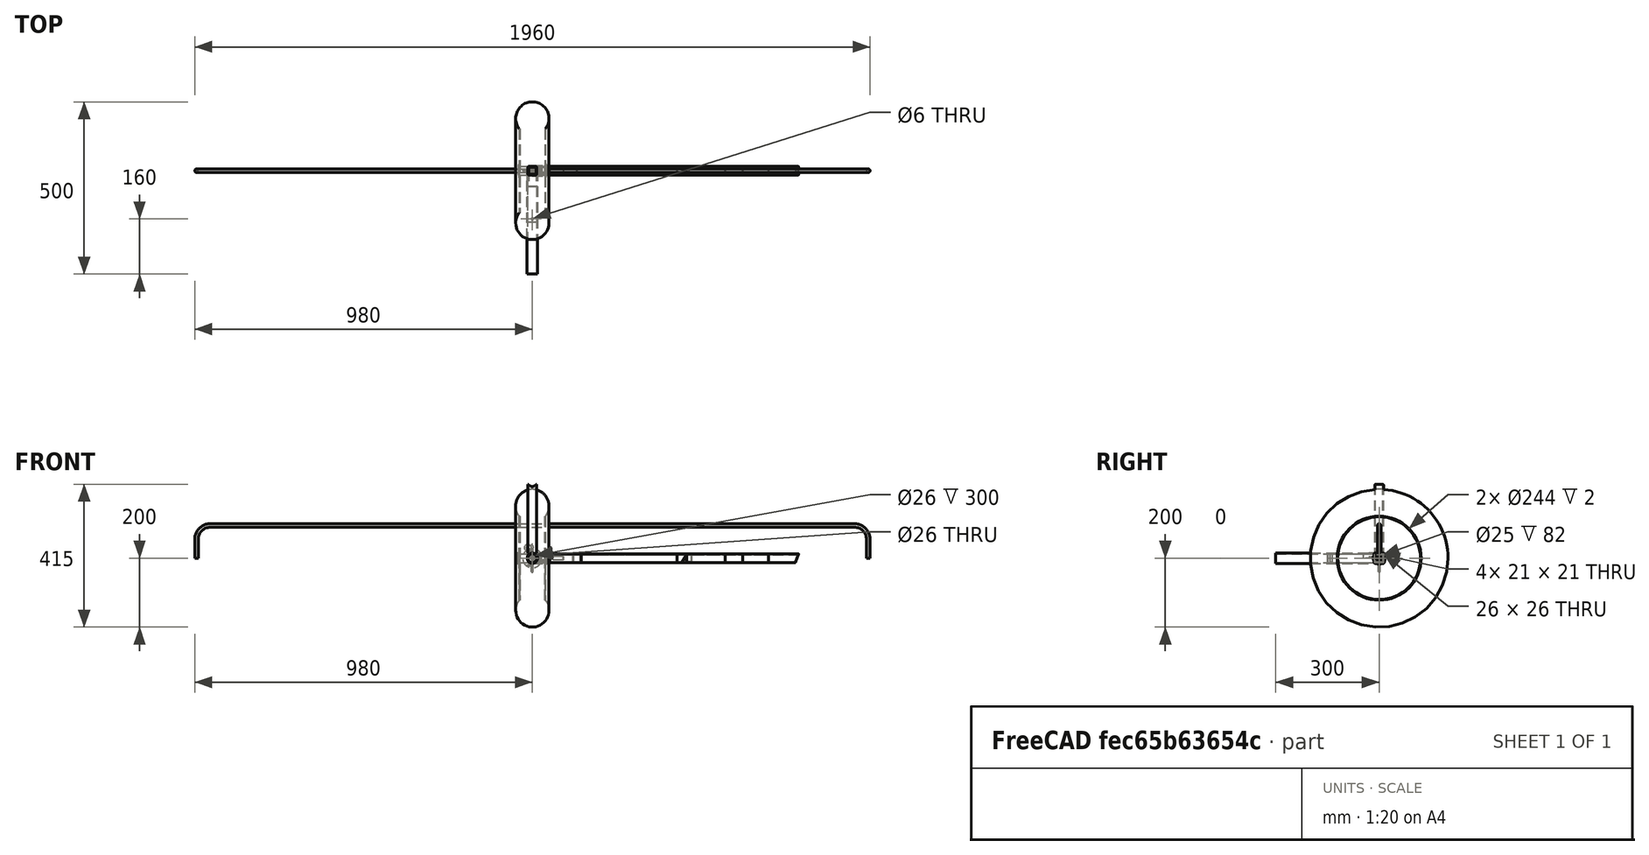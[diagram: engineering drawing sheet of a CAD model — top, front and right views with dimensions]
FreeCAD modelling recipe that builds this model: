
FCSTD DOCUMENT  (FreeCAD 1.0R39109 (Git))
Label: brouetteas4-am
License: Creative Commons Attribution-NonCommercial-ShareAlike
LicenseURL: http://creativecommons.org/licenses/by-nc-sa/4.0/
objects: TechDraw::DrawViewAnnotation×100, PartDesign::CoordinateSystem×62, App::Link×60, TechDraw::DrawProjGroupItem×58, TechDraw::DrawViewBalloon×56, TechDraw::DrawViewDimension×39, Sketcher::SketchObject×37, App::Part×25, PartDesign::Body×24, PartDesign::Pad×20, TechDraw::DrawSVGTemplate×16, TechDraw::DrawPage×16, TechDraw::DrawGeomHatch×14, TechDraw::DrawProjGroup×13, Spreadsheet::Sheet×12, TechDraw::DrawViewSpreadsheet×10, PartDesign::Groove×8, PartDesign::Plane×6, TechDraw::DrawViewDimExtent×3, TechDraw::DrawViewDetail×3, +7 more types
note: 342 computed .brp shape members not serialized (recipe doc carries the construction recipe); baked Part::Feature solids carry a one-line shape summary decoded from their .brp

FEATURE [PartDesign::CoordinateSystem] LCS_Origin
  AttacherType = Attacher::AttachEngine3D
  AttachmentSupport = -> [X_Axis]
  MapMode = 2
FEATURE [App::DocumentObjectGroup] Constraints
FEATURE [App::FeaturePython] Variables  # WARN: FeaturePython — macro-defined, semantics opaque (R4)
FEATURE [Sketcher::SketchObject] Sketch
  ArcFitTolerance = 0
  FullyConstrained = true
  MakeInternals = false
  MapMode = 5
  Placement = pos=(0,0,0) rot=(0.57735,0.57735,0.57735;2.0944rad)
  expr: Constraints[15] = .Constraints.hauteur * 0.1
  expr: Constraints[27] = .Constraints.epaisseur
  sketch-geometry (12):
    g0: LineSegment StartX=-10 StartY=12.5 StartZ=0 EndX=10 EndY=12.5 EndZ=0
    g1: LineSegment StartX=12.5 StartY=10 StartZ=0 EndX=12.5 EndY=-10 EndZ=0
    g2: LineSegment StartX=10 StartY=-12.5 StartZ=0 EndX=-10 EndY=-12.5 EndZ=0
    g3: LineSegment StartX=-12.5 StartY=-10 StartZ=0 EndX=-12.5 EndY=10 EndZ=0
    g4: ArcOfCircle CenterX=-10 CenterY=10 CenterZ=0 NormalX=0 NormalY=0 NormalZ=1 AngleXU=0 Radius=2.5 StartAngle=1.5708 EndAngle=3.14159
    g5: ArcOfCircle CenterX=10 CenterY=10 CenterZ=0 NormalX=0 NormalY=0 NormalZ=1 AngleXU=0 Radius=2.5 StartAngle=2e-16 EndAngle=1.5708
    g6: ArcOfCircle CenterX=10 CenterY=-10 CenterZ=0 NormalX=0 NormalY=0 NormalZ=1 AngleXU=0 Radius=2.5 StartAngle=4.71239 EndAngle=6.28319
    g7: ArcOfCircle CenterX=-10 CenterY=-10 CenterZ=0 NormalX=0 NormalY=0 NormalZ=1 AngleXU=0 Radius=2.5 StartAngle=3.14159 EndAngle=4.71239
    g8: LineSegment StartX=-10.5 StartY=10.5 StartZ=0 EndX=10.5 EndY=10.5 EndZ=0
    g9: LineSegment StartX=10.5 StartY=10.5 StartZ=0 EndX=10.5 EndY=-10.5 EndZ=0
    g10: LineSegment StartX=10.5 StartY=-10.5 StartZ=0 EndX=-10.5 EndY=-10.5 EndZ=0
    g11: LineSegment StartX=-10.5 StartY=-10.5 StartZ=0 EndX=-10.5 EndY=10.5 EndZ=0
  constraints (28):
    c: Horizontal(g2)
    c: Vertical(g3)
    c: Tangent(g0,g4) = 1.5708
    c: Tangent(g3,g4) = 1.5708
    c: Tangent(g0,g5) = 1.5708
    c: Tangent(g1,g5) = 1.5708
    c: Tangent(g1,g6) = 1.5708
    c: Tangent(g2,g6) = 1.5708
    c: Tangent(g2,g7) = 1.5708
    c: Tangent(g3,g7) = 1.5708
    c: Equal(g4,g5)
    c: DistanceY(g2,g0) = 25  'hauteur'
    c: DistanceX(g3,g1) = 25  'largeur'
    c: Equal(g5,g6)
    c: Equal(g6,g7)
    c: Radius(g7) = 2.5
    c: Symmetric(g1,g1,g-1)
    c: Symmetric(g0,g0,g-2)
    c: Coincident(g8,g9)
    c: Coincident(g9,g10)
    c: Coincident(g10,g11)
    c: Coincident(g11,g8)
    c: Horizontal(g10)
    c: Vertical(g11)
    c: Symmetric(g8,g9,g-1)
    c: Symmetric(g8,g8,g-2)
    c: DistanceX(g3,g8) = 2  'epaisseur'
    c: DistanceY(g2,g9) = 2
FEATURE [PartDesign::Pad] Pad
  Direction = (1,1e-16,-1e-16)
  Length = 2285
  Length2 = 100
  Placement = pos=(0,0,0) rot=(0.57735,0.57735,0.57735;2.0944rad)
  Profile = -> Sketch
  Suppressed = false
  Type = 0
  expr: Length = Spreadsheet.B4 - Spreadsheet.B2 + 300
FEATURE [PartDesign::CoordinateSystem] LCS_0  label="cote1"
  AttacherType = Attacher::AttachEngine3D
  AttachmentSupport = -> [X_Axis002]
  MapMode = 2
FEATURE [PartDesign::CoordinateSystem] LCS_0001  label="cote1A2"
  AttacherType = Attacher::AttachEngine3D
  AttachmentSupport = -> [X_Axis003]
  MapMode = 2
FEATURE [Sketcher::SketchObject] Sketch001
  ArcFitTolerance = 0
  FullyConstrained = true
  MakeInternals = false
  MapMode = 5
  Placement = pos=(0,0,0) rot=(0.57735,0.57735,0.57735;2.0944rad)
  expr: Constraints[15] = .Constraints.hauteur * 0.1
  expr: Constraints[27] = .Constraints.epaisseur
  sketch-geometry (12):
    g0: LineSegment StartX=-10 StartY=12.5 StartZ=0 EndX=10 EndY=12.5 EndZ=0
    g1: LineSegment StartX=12.5 StartY=10 StartZ=0 EndX=12.5 EndY=-10 EndZ=0
    g2: LineSegment StartX=10 StartY=-12.5 StartZ=0 EndX=-10 EndY=-12.5 EndZ=0
    g3: LineSegment StartX=-12.5 StartY=-10 StartZ=0 EndX=-12.5 EndY=10 EndZ=0
    g4: ArcOfCircle CenterX=-10 CenterY=10 CenterZ=0 NormalX=0 NormalY=0 NormalZ=1 AngleXU=0 Radius=2.5 StartAngle=1.5708 EndAngle=3.14159
    g5: ArcOfCircle CenterX=10 CenterY=10 CenterZ=0 NormalX=0 NormalY=0 NormalZ=1 AngleXU=0 Radius=2.5 StartAngle=2e-16 EndAngle=1.5708
    g6: ArcOfCircle CenterX=10 CenterY=-10 CenterZ=0 NormalX=0 NormalY=0 NormalZ=1 AngleXU=0 Radius=2.5 StartAngle=4.71239 EndAngle=6.28319
    g7: ArcOfCircle CenterX=-10 CenterY=-10 CenterZ=0 NormalX=0 NormalY=0 NormalZ=1 AngleXU=0 Radius=2.5 StartAngle=3.14159 EndAngle=4.71239
    g8: LineSegment StartX=-10.5 StartY=10.5 StartZ=0 EndX=10.5 EndY=10.5 EndZ=0
    g9: LineSegment StartX=10.5 StartY=10.5 StartZ=0 EndX=10.5 EndY=-10.5 EndZ=0
    g10: LineSegment StartX=10.5 StartY=-10.5 StartZ=0 EndX=-10.5 EndY=-10.5 EndZ=0
    g11: LineSegment StartX=-10.5 StartY=-10.5 StartZ=0 EndX=-10.5 EndY=10.5 EndZ=0
  constraints (28):
    c: Horizontal(g2)
    c: Vertical(g3)
    c: Tangent(g0,g4) = 1.5708
    c: Tangent(g3,g4) = 1.5708
    c: Tangent(g0,g5) = 1.5708
    c: Tangent(g1,g5) = 1.5708
    c: Tangent(g1,g6) = 1.5708
    c: Tangent(g2,g6) = 1.5708
    c: Tangent(g2,g7) = 1.5708
    c: Tangent(g3,g7) = 1.5708
    c: Equal(g4,g5)
    c: DistanceY(g2,g0) = 25  'hauteur'
    c: DistanceX(g3,g1) = 25  'largeur'
    c: Equal(g5,g6)
    c: Equal(g6,g7)
    c: Radius(g7) = 2.5
    c: Symmetric(g1,g1,g-1)
    c: Symmetric(g0,g0,g-2)
    c: Coincident(g8,g9)
    c: Coincident(g9,g10)
    c: Coincident(g10,g11)
    c: Coincident(g11,g8)
    c: Horizontal(g10)
    c: Vertical(g11)
    c: Symmetric(g8,g9,g-1)
    c: Symmetric(g8,g8,g-2)
    c: DistanceX(g3,g8) = 2  'epaisseur'
    c: DistanceY(g2,g9) = 2
FEATURE [PartDesign::Body] Body001
  AllowCompound = false
  Origin = -> Origin004
FEATURE [PartDesign::Pad] Pad001
  Direction = (1,1e-16,-1e-16)
  Length = 610
  Length2 = 100
  Placement = pos=(0,0,0) rot=(0.57735,0.57735,0.57735;2.0944rad)
  Profile = -> Sketch001
  Suppressed = false
  Type = 0
FEATURE [PartDesign::CoordinateSystem] LCS_0002
  AttacherType = Attacher::AttachEngine3D
  AttachmentOffset = pos=(0,5,0) rot=(0,0,1;0rad)
  AttachmentSupport = -> [X_Axis005]
  MapMode = 2
  Placement = pos=(0,5,0) rot=(0,0,1;0rad)
FEATURE [PartDesign::CoordinateSystem] LCS_0003
  AttacherType = Attacher::AttachEngine3D
  AttachmentOffset = pos=(0,5,0) rot=(0,0,1;0rad)
  AttachmentSupport = -> [X_Axis006]
  MapMode = 2
  Placement = pos=(0,5,0) rot=(0,0,1;0rad)
FEATURE [Sketcher::SketchObject] Sketch002
  ArcFitTolerance = 0
  AttachmentSupport = -> [XZ_Plane007]
  FullyConstrained = true
  MakeInternals = false
  MapMode = 5
  Placement = pos=(0,0,0) rot=(1,0,0;1.5708rad)
  expr: .Constraints.longueur = Spreadsheet.B4 - Spreadsheet.B2 * 2 - 10
  expr: Constraints[4] = Spreadsheet.B2
  sketch-geometry (7):
    g0: LineSegment StartX=-975 StartY=0 StartZ=0 EndX=-975 EndY=25 EndZ=0
    g1: LineSegment StartX=975 StartY=8e-16 StartZ=0 EndX=975 EndY=25 EndZ=0
    g2: LineSegment StartX=-975 StartY=25 StartZ=0 EndX=-975 EndY=55 EndZ=0
    g3: LineSegment StartX=-935 StartY=95 StartZ=0 EndX=935 EndY=95 EndZ=0
    g4: LineSegment StartX=975 StartY=55 StartZ=0 EndX=975 EndY=25 EndZ=0
    g5: ArcOfCircle CenterX=935 CenterY=55 CenterZ=0 NormalX=0 NormalY=0 NormalZ=1 AngleXU=0 Radius=40 StartAngle=0 EndAngle=1.5708
    g6: ArcOfCircle CenterX=-935 CenterY=55 CenterZ=0 NormalX=0 NormalY=0 NormalZ=1 AngleXU=0 Radius=40 StartAngle=1.5708 EndAngle=3.14159
  constraints (19):
    c: PointOnObject(g0,g-1)
    c: Vertical(g0)
    c: Vertical(g1)
    c: Symmetric(g0,g1,g-2)
    c: DistanceY(g0,g0) = 25
    c: DistanceX(g0,g1) = 1950  'longueur'
    c: Equal(g1,g0)
    c: Coincident(g0,g2)
    c: Vertical(g2)
    c: Horizontal(g3)
    c: Coincident(g4,g1)
    c: Vertical(g4)
    c: Tangent(g3,g5) = 1.5708
    c: Tangent(g4,g5) = 1.5708
    c: Tangent(g2,g6) = 1.5708
    c: Tangent(g3,g6) = 1.5708
    c: Equal(g6,g5)
    c: DistanceY(g0,g3) = 70
    c: Radius(g6) = 40
FEATURE [Sketcher::SketchObject] Sketch003
  ArcFitTolerance = 0
  AttachmentSupport = -> [XY_Plane007]
  ExternalGeometry = -> [Sketch002]
  FullyConstrained = true
  MakeInternals = false
  MapMode = 5
  sketch-geometry (1):
    g0: Circle CenterX=-975 CenterY=0 CenterZ=0 NormalX=0 NormalY=0 NormalZ=1 AngleXU=0 Radius=5
  constraints (2):
    c: Coincident(g0,g-3)
    c: Diameter(g0) = 10
FEATURE [PartDesign::AdditivePipe] AdditivePipe
  AuxilleryCurvelinear = true
  AuxillerySpineTangent = false
  Binormal = (0,0,0)
  Mode = 0
  Profile = -> Sketch003
  Spine = -> Sketch002
  SpineTangent = false
  Suppressed = false
  Transformation = 0
  Transition = 0
FEATURE [PartDesign::Body] Body002
  AllowCompound = false
  Group = -> [Sketch002,Sketch003,AdditivePipe]
  Origin = -> Origin007
  Tip = -> AdditivePipe
FEATURE [App::Part] A3
  Group = -> [LCS_0002,Body002]
  Nom_de_la_piece = A3
  Origin = -> Origin005
  Reference_AP = fer rond Ø10
  longueur = 2140
FEATURE [Sketcher::SketchObject] Sketch004
  ArcFitTolerance = 0
  AttachmentSupport = -> [YZ_Plane008]
  FullyConstrained = true
  MakeInternals = false
  MapMode = 5
  Placement = pos=(0,0,0) rot=(0.57735,0.57735,0.57735;2.0944rad)
  sketch-geometry (1):
    g0: Circle CenterX=0 CenterY=0 CenterZ=0 NormalX=0 NormalY=0 NormalZ=1 AngleXU=0 Radius=5
  constraints (2):
    c: Coincident(g0,g-1)
    c: Diameter(g0) = 10  'diametre'
FEATURE [PartDesign::Pad] Pad002
  Direction = (1,0,0)
  Length = 90
  Length2 = 100
  Placement = pos=(0,0,0) rot=(0.57735,0.57735,0.57735;2.0944rad)
  Profile = -> Sketch004
  Suppressed = false
  Type = 0
FEATURE [PartDesign::Body] Body003
  AllowCompound = false
  Group = -> [Sketch004,Pad002]
  Origin = -> Origin008
  Tip = -> Pad002
FEATURE [App::Part] A4
  Group = -> [LCS_0003,Body003]
  Nom_de_la_piece = 'A4
  Origin = -> Origin006
  Reference_AP = fer rond Ø10
  longueur = 90
FEATURE [PartDesign::CoordinateSystem] cote2A2
  AttacherType = Attacher::AttachEngine3D
  AttachmentSupport = -> [Pad001]
  MapMode = 5
  Placement = pos=(610,2.684e-13,0) rot=(0.57735,0.57735,0.57735;2.0944rad)
FEATURE [Spreadsheet::Sheet] Spreadsheet
  cells = A1='profile; A2='tube carré; B2=25; C2='mm; A4='taille utile du plateau; B4=2010; C4='X; D4=610; A5='hauteur plateau; B5=500; A6='hauteur de la roue; B6=400; A7='axe; B7=25; A8='epaisseur upn axe; B8=4; A9='espace des roues; B9=95; A10='ecart au sol; B10=75; A11='hauteur des mains; B11==D11 * 0.45; C11='taille de la personne; D11=1700; A12='hauteur du panneau finale; B12=610; A13='tube poigné; B13=30
FEATURE [PartDesign::CoordinateSystem] face1A2
  AttacherType = Attacher::AttachEngine3D
  AttachmentOffset = pos=(0,12.5,0) rot=(0,0,1;0rad)
  AttachmentSupport = -> [Pad001]
  MapMode = 5
  Placement = pos=(12.5,12.5,2.1e-15) rot=(0.57735,0.57735,0.57735;4.18879rad)
  expr: .AttachmentOffset.Base.y = Spreadsheet.B2 / 2
FEATURE [PartDesign::CoordinateSystem] face4A2
  AttacherType = Attacher::AttachEngine3D
  AttachmentOffset = pos=(0,597.5,0) rot=(0,0,1;0rad)
  AttachmentSupport = -> [Pad001]
  MapMode = 5
  Placement = pos=(597.5,12.5,2.1e-15) rot=(0.57735,0.57735,0.57735;4.18879rad)
  expr: .AttachmentOffset.Base.y = Spreadsheet.D4 - Spreadsheet.B2 / 2
FEATURE [PartDesign::CoordinateSystem] face2  label="face2A2"
  AttacherType = Attacher::AttachEngine3D
  AttachmentOffset = pos=(0,207.5,0) rot=(0,0,1;0rad)
  AttachmentSupport = -> [Pad001]
  MapMode = 5
  Placement = pos=(207.5,12.5,2.1e-15) rot=(0.57735,0.57735,0.57735;4.18879rad)
  expr: .AttachmentOffset.Base.y = (Spreadsheet.D4 - Spreadsheet.B2) * 1 / 3 + Spreadsheet.B2 / 2
FEATURE [PartDesign::CoordinateSystem] face3A2
  AttacherType = Attacher::AttachEngine3D
  AttachmentOffset = pos=(0,402.5,0) rot=(0,0,1;0rad)
  AttachmentSupport = -> [Pad001]
  MapMode = 5
  Placement = pos=(402.5,12.5,2.1e-15) rot=(0.57735,0.57735,0.57735;4.18879rad)
  expr: .AttachmentOffset.Base.y = (Spreadsheet.D4 - Spreadsheet.B2) * 2 / 3 + Spreadsheet.B2 / 2
FEATURE [PartDesign::CoordinateSystem] attach
  AttacherType = Attacher::AttachEngine3D
  AttachmentOffset = pos=(0,305,0) rot=(0,0,1;0rad)
  AttachmentSupport = -> [Pad001]
  MapMode = 5
  Placement = pos=(305,-12.5,-2.1e-15) rot=(0.57735,0.57735,-0.57735;2.0944rad)
  expr: .AttachmentOffset.Base.y = Spreadsheet.D4 / 2
FEATURE [App::Link] A2001
  AssemblyType = Asm4EE
  AttachedBy = #attach
  AttachedTo = Parent Assembly#LCS_Origin
  AttachmentOffset = pos=(0,0,0) rot=(0,-1,0;1.5708rad)
  LinkPlacement = pos=(12.5,-305,-2.84e-14) rot=(-0.707107,-0.707107,0;3.14159rad)
  LinkedObject = -> A2
  Placement = pos=(12.5,-305,-2.84e-14) rot=(-0.707107,-0.707107,0;3.14159rad)
  expr: Placement = LCS_Origin.Placement * AttachmentOffset * attach.Placement ^ -1
FEATURE [App::Link] A1001
  AssemblyType = Asm4EE
  AttachedBy = #LCS_0
  AttachedTo = A2001#face1A2
  AttachmentOffset = pos=(0,0,0) rot=(0,-1,0;1.5708rad)
  LinkPlacement = pos=(25,-292.5,-3.05e-14) rot=(0,0,1;0rad)
  LinkedObject = -> A1
  Placement = pos=(25,-292.5,-3.05e-14) rot=(0,0,1;0rad)
  expr: Placement = A2001.Placement * face1A2.Placement * AttachmentOffset * LCS_0.Placement ^ -1
FEATURE [App::Link] A1004
  AssemblyType = Asm4EE
  AttachedBy = #LCS_0
  AttachedTo = A2001#face4A2
  AttachmentOffset = pos=(0,0,0) rot=(0,-1,0;1.5708rad)
  LinkPlacement = pos=(25,292.5,1.54e-14) rot=(0,0,1;0rad)
  LinkedObject = -> A1
  Placement = pos=(25,292.5,1.54e-14) rot=(0,0,1;0rad)
  expr: Placement = A2001.Placement * face4A2.Placement * AttachmentOffset * LCS_0.Placement ^ -1
FEATURE [App::Link] A3001
  AssemblyType = Asm4EE
  AttachedBy = #LCS_0002
  AttachedTo = A1001#faceA1
  AttachmentOffset = pos=(0,0,0) rot=(0.57735,0.57735,-0.57735;4.18879rad)
  LinkPlacement = pos=(1005,-310,-12.5) rot=(0,0,1;0rad)
  LinkedObject = -> A3
  Placement = pos=(1005,-310,-12.5) rot=(0,0,1;0rad)
  expr: Placement = A1001.Placement * faceA1.Placement * AttachmentOffset * LCS_0002.Placement ^ -1
FEATURE [App::Link] A3002
  AssemblyType = Asm4EE
  AttachedBy = #LCS_0002
  AttachedTo = A1004#face2A1
  AttachmentOffset = pos=(0,0,0) rot=(-0.57735,0.57735,-0.57735;2.0944rad)
  LinkPlacement = pos=(1005,310,-12.5) rot=(0,0,1;3.14159rad)
  LinkedObject = -> A3
  Placement = pos=(1005,310,-12.5) rot=(0,0,1;3.14159rad)
  expr: Placement = A1004.Placement * face2A1.Placement * AttachmentOffset * LCS_0002.Placement ^ -1
FEATURE [App::Link] A4001
  AssemblyType = Asm4EE
  AttachedBy = #LCS_0003
  AttachedTo = A1001#faceA1
  AttachmentOffset = pos=(0,0,0) rot=(0,-0.707107,0.707107;3.14159rad)
  LinkPlacement = pos=(1005,-310,-12.5) rot=(0,-1,0;1.5708rad)
  LinkedObject = -> A4
  Placement = pos=(1005,-310,-12.5) rot=(0,-1,0;1.5708rad)
  expr: Placement = A1001.Placement * faceA1.Placement * AttachmentOffset * LCS_0003.Placement ^ -1
FEATURE [App::Link] A4002
  AssemblyType = Asm4EE
  AttachedBy = #LCS_0003
  AttachedTo = A1004#face2A1
  AttachmentOffset = pos=(0,0,0) rot=(1,0,0;4.71239rad)
  LinkPlacement = pos=(1005,310,-12.5) rot=(-0.707107,0,-0.707107;3.14159rad)
  LinkedObject = -> A4
  Placement = pos=(1005,310,-12.5) rot=(-0.707107,0,-0.707107;3.14159rad)
  expr: Placement = A1004.Placement * face2A1.Placement * AttachmentOffset * LCS_0003.Placement ^ -1
FEATURE [PartDesign::CoordinateSystem] basbord
  AttacherType = Attacher::AttachEngine3D
  AttachmentOffset = pos=(0,-12.5,0) rot=(0,0,1;0rad)
  AttachmentSupport = -> [Pad001]
  MapMode = 5
  Placement = pos=(610,2.684e-13,-12.5) rot=(0.57735,0.57735,0.57735;2.0944rad)
  expr: .AttachmentOffset.Base.y = -Spreadsheet.B2 / 2
FEATURE [App::Link] A2003
  AssemblyType = Asm4EE
  AttachedBy = #basbord
  AttachedTo = A1004#face2A1
  AttachmentOffset = pos=(0,0,0) rot=(0,0,1;1.5708rad)
  LinkPlacement = pos=(1005,-305,-25) rot=(0.707107,0.707107,0;3.14159rad)
  LinkedObject = -> A2
  Placement = pos=(1005,-305,-25) rot=(0.707107,0.707107,0;3.14159rad)
  expr: Placement = A1004.Placement * face2A1.Placement * AttachmentOffset * basbord.Placement ^ -1
FEATURE [PartDesign::CoordinateSystem] LCS_0004
  AttacherType = Attacher::AttachEngine3D
  AttachmentOffset = pos=(100,-12.5,0) rot=(0,0,1;0rad)
  AttachmentSupport = -> [X_Axis009]
  MapMode = 2
  Placement = pos=(100,-12.5,0) rot=(0,0,1;0rad)
FEATURE [Sketcher::SketchObject] Sketch005
  ArcFitTolerance = 0
  AttachmentSupport = -> [XY_Plane010]
  FullyConstrained = true
  MakeInternals = false
  MapMode = 5
  sketch-geometry (16):
    g0: LineSegment StartX=-41 StartY=12.5 StartZ=0 EndX=41 EndY=12.5 EndZ=0
    g1: LineSegment StartX=-41 StartY=12.5 StartZ=0 EndX=-41 EndY=17.5 EndZ=0
    g2: LineSegment StartX=-41 StartY=17.5 StartZ=0 EndX=-38 EndY=17.5 EndZ=0
    g3: LineSegment StartX=-38 StartY=17.5 StartZ=0 EndX=-38 EndY=120 EndZ=0
    g4: LineSegment StartX=-38 StartY=120 StartZ=0 EndX=-36 EndY=120 EndZ=0
    g5: LineSegment StartX=-36 StartY=120 StartZ=0 EndX=-36 EndY=122 EndZ=0
    g6: LineSegment StartX=-36 StartY=122 StartZ=0 EndX=-38 EndY=122 EndZ=0
    g7: LineSegment StartX=41 StartY=12.5 StartZ=0 EndX=41 EndY=17.5 EndZ=0
    g8: LineSegment StartX=41 StartY=17.5 StartZ=0 EndX=38 EndY=17.5 EndZ=0
    g9: LineSegment StartX=38 StartY=17.5 StartZ=0 EndX=38 EndY=120 EndZ=0
    g10: LineSegment StartX=38 StartY=120 StartZ=0 EndX=36 EndY=120 EndZ=0
    g11: LineSegment StartX=36 StartY=120 StartZ=0 EndX=36 EndY=122 EndZ=0
    g12: LineSegment StartX=36 StartY=122 StartZ=0 EndX=38 EndY=122 EndZ=0
    g13: GeomPoint [constr] X=-1e-15 Y=151.744 Z=0
    g14: GeomPoint [constr] X=0 Y=200 Z=0
    g15: ArcOfCircle CenterX=-1e-15 CenterY=151.744 CenterZ=0 NormalX=0 NormalY=0 NormalZ=1 AngleXU=0 Radius=48.2564 StartAngle=5.61907 EndAngle=10.0889
  constraints (42):
    c: Symmetric(g0,g0,g-2)
    c: Coincident(g0,g1)
    c: Vertical(g1)
    c: Coincident(g1,g2)
    c: Horizontal(g2)
    c: Coincident(g2,g3)
    c: Vertical(g3)
    c: Coincident(g3,g4)
    c: Horizontal(g4)
    c: Coincident(g4,g5)
    c: Coincident(g5,g6)
    c: Horizontal(g6)
    c: Vertical(g5)
    c: PointOnObject(g6,g3)
    c: DistanceX(g2,g2) = 3
    c: DistanceX(g4,g4) = 2
    c: DistanceY(g5,g5) = 2
    c: Vertical(g7)
    c: Coincident(g7,g8)
    c: Horizontal(g8)
    c: Coincident(g8,g9)
    c: Coincident(g9,g10)
    c: Horizontal(g10)
    c: Coincident(g10,g11)
    c: Coincident(g11,g12)
    c: Horizontal(g12)
    c: Vertical(g11)
    c: PointOnObject(g12,g9)
    c: Symmetric(g9,g3,g-2)
    c: Symmetric(g5,g11,g-2)
    c: DistanceX(g2,g8) = 76
    c: Coincident(g0,g7)
    c: DistanceY(g-1,g0) = 12.5
    c: DistanceY(g7,g7) = 5
    c: Symmetric(g2,g8,g-2)
    c: PointOnObject(g14,g-2)
    c: DistanceY(g-1,g9) = 120
    c: DistanceY(g-1,g14) = 200
    c: Coincident(g15,g13)
    c: Coincident(g15,g6)
    c: Coincident(g15,g12)
    c: PointOnObject(g14,g15)
FEATURE [PartDesign::Revolution] Revolution
  Angle = 360
  Angle2 = 60
  Axis = (1,0,0)
  Base = (0,0,0)
  Profile = -> Sketch005
  ReferenceAxis = -> Sketch005 [H_Axis]
  Suppressed = false
  Type = 0
FEATURE [PartDesign::Body] Body004
  AllowCompound = false
  Group = -> [Sketch005,Revolution]
  Origin = -> Origin010
  Tip = -> Revolution
FEATURE [App::Part] Roue_increvable___389___axe25_L_82
  Group = -> [LCS_0004,Body004]
  Nom_de_la_piece = roue
  Origin = -> Origin009
  Reference_AP = Roue increvable Ø389 Øaxe25 L 82
FEATURE [PartDesign::CoordinateSystem] LCS_0005
  AttacherType = Attacher::AttachEngine3D
  AttachmentSupport = -> [X_Axis011]
  MapMode = 2
FEATURE [PartDesign::Body] Body005
  AllowCompound = false
  Origin = -> Origin012
FEATURE [Sketcher::SketchObject] Sketch007
  ArcFitTolerance = 0
  FullyConstrained = true
  MakeInternals = false
  MapMode = 2
  Placement = pos=(0,0,0) rot=(0.57735,0.57735,0.57735;2.0944rad)
  expr: Constraints[15] = .Constraints.hauteur * 0.1
  expr: Constraints[27] = .Constraints.epaisseur
  sketch-geometry (12):
    g0: LineSegment StartX=-10 StartY=12.5 StartZ=0 EndX=10 EndY=12.5 EndZ=0
    g1: LineSegment StartX=12.5 StartY=10 StartZ=0 EndX=12.5 EndY=-10 EndZ=0
    g2: LineSegment StartX=10 StartY=-12.5 StartZ=0 EndX=-10 EndY=-12.5 EndZ=0
    g3: LineSegment StartX=-12.5 StartY=-10 StartZ=0 EndX=-12.5 EndY=10 EndZ=0
    g4: ArcOfCircle CenterX=-10 CenterY=10 CenterZ=0 NormalX=0 NormalY=0 NormalZ=1 AngleXU=0 Radius=2.5 StartAngle=1.5708 EndAngle=3.14159
    g5: ArcOfCircle CenterX=10 CenterY=10 CenterZ=0 NormalX=0 NormalY=0 NormalZ=1 AngleXU=0 Radius=2.5 StartAngle=2e-16 EndAngle=1.5708
    g6: ArcOfCircle CenterX=10 CenterY=-10 CenterZ=0 NormalX=0 NormalY=0 NormalZ=1 AngleXU=0 Radius=2.5 StartAngle=4.71239 EndAngle=6.28319
    g7: ArcOfCircle CenterX=-10 CenterY=-10 CenterZ=0 NormalX=0 NormalY=0 NormalZ=1 AngleXU=0 Radius=2.5 StartAngle=3.14159 EndAngle=4.71239
    g8: LineSegment StartX=-10.5 StartY=10.5 StartZ=0 EndX=10.5 EndY=10.5 EndZ=0
    g9: LineSegment StartX=10.5 StartY=10.5 StartZ=0 EndX=10.5 EndY=-10.5 EndZ=0
    g10: LineSegment StartX=10.5 StartY=-10.5 StartZ=0 EndX=-10.5 EndY=-10.5 EndZ=0
    g11: LineSegment StartX=-10.5 StartY=-10.5 StartZ=0 EndX=-10.5 EndY=10.5 EndZ=0
  constraints (28):
    c: Horizontal(g2)
    c: Vertical(g3)
    c: Tangent(g0,g4) = 1.5708
    c: Tangent(g3,g4) = 1.5708
    c: Tangent(g0,g5) = 1.5708
    c: Tangent(g1,g5) = 1.5708
    c: Tangent(g1,g6) = 1.5708
    c: Tangent(g2,g6) = 1.5708
    c: Tangent(g2,g7) = 1.5708
    c: Tangent(g3,g7) = 1.5708
    c: Equal(g4,g5)
    c: DistanceY(g2,g0) = 25  'hauteur'
    c: DistanceX(g3,g1) = 25  'largeur'
    c: Equal(g5,g6)
    c: Equal(g6,g7)
    c: Radius(g7) = 2.5
    c: Symmetric(g1,g1,g-1)
    c: Symmetric(g0,g0,g-2)
    c: Coincident(g8,g9)
    c: Coincident(g9,g10)
    c: Coincident(g10,g11)
    c: Coincident(g11,g8)
    c: Horizontal(g10)
    c: Vertical(g11)
    c: Symmetric(g8,g9,g-1)
    c: Symmetric(g8,g8,g-2)
    c: DistanceX(g3,g8) = 2  'epaisseur'
    c: DistanceY(g2,g9) = 2
FEATURE [PartDesign::Pad] Pad003
  Direction = (1,1e-16,-1e-16)
  Length = 258.5
  Length2 = 100
  Placement = pos=(0,0,0) rot=(0.57735,0.57735,0.57735;2.0944rad)
  Profile = -> Sketch007
  Suppressed = false
  Type = 0
  expr: Length = Spreadsheet.B5 - Spreadsheet.B6 / 2 - Spreadsheet.B7 / 2 - Spreadsheet.B8 - Spreadsheet.B2
FEATURE [PartDesign::CoordinateSystem] roue1
  AttacherType = Attacher::AttachEngine3D
  AttachmentOffset = pos=(0,82.5,0) rot=(0,0,1;0rad)
  AttachmentSupport = -> [Pad001]
  MapMode = 5
  Placement = pos=(82.5,1.56e-14,12.5) rot=(0,0,-1;1.5708rad)
  expr: .AttachmentOffset.Base.y = Spreadsheet.B9 - Spreadsheet.B2 / 2
FEATURE [PartDesign::CoordinateSystem] roue2
  AttacherType = Attacher::AttachEngine3D
  AttachmentOffset = pos=(0,527.5,0) rot=(0,0,1;0rad)
  AttachmentSupport = -> [Pad001]
  MapMode = 5
  Placement = pos=(527.5,1.144e-13,12.5) rot=(0,0,-1;1.5708rad)
  expr: .AttachmentOffset.Base.y = Spreadsheet.D4 - (Spreadsheet.B9 - Spreadsheet.B2 / 2)
FEATURE [App::Part] A2
  Group = -> [LCS_0001,Body001,Sketch001,Pad001,cote2A2,face1A2,face4A2,face2,face3A2,attach,basbord,roue1,roue2]
  Nom_de_la_piece = 'A2
  Origin = -> Origin003
  Reference_AP = Tube carré 25 x 2
  longueur = 610
FEATURE [App::Link] A5001
  AssemblyType = Asm4EE
  AttachedBy = #LCS_0005
  AttachedTo = A2003#roue1
  AttachmentOffset = pos=(0,0,0) rot=(-0.57735,-0.57735,-0.57735;2.0944rad)
  LinkPlacement = pos=(1005,-222.5,-37.5) rot=(-0.57735,0.57735,0.57735;2.0944rad)
  LinkedObject = -> A5
  Placement = pos=(1005,-222.5,-37.5) rot=(-0.57735,0.57735,0.57735;2.0944rad)
  expr: Placement = A2003.Placement * roue1.Placement * AttachmentOffset * LCS_0005.Placement ^ -1
FEATURE [App::Link] A5002
  AssemblyType = Asm4EE
  AttachedBy = #LCS_0005
  AttachedTo = A2003#roue2
  AttachmentOffset = pos=(0,0,0) rot=(0,1,0;4.71239rad)
  LinkPlacement = pos=(1005,222.5,-37.5) rot=(0,-1,0;4.71239rad)
  LinkedObject = -> A5
  Placement = pos=(1005,222.5,-37.5) rot=(0,-1,0;4.71239rad)
  expr: Placement = A2003.Placement * roue2.Placement * AttachmentOffset * LCS_0005.Placement ^ -1
FEATURE [PartDesign::CoordinateSystem] renfort
  AttacherType = Attacher::AttachEngine3D
  AttachmentOffset = pos=(0,246,0) rot=(0,0,1;0rad)
  AttachmentSupport = -> [Pad003]
  MapMode = 5
  Placement = pos=(246,5.19e-14,12.5) rot=(0,0,-1;1.5708rad)
  expr: .AttachmentOffset.Base.y = Pad003.Length - Spreadsheet.B2 * 1 mm / 2
FEATURE [PartDesign::CoordinateSystem] LCS_0006
  AttacherType = Attacher::AttachEngine3D
  AttachmentSupport = -> [X_Axis013]
  MapMode = 2
FEATURE [Sketcher::SketchObject] Sketch008
  ArcFitTolerance = 0
  FullyConstrained = true
  MakeInternals = false
  MapMode = 2
  Placement = pos=(0,0,0) rot=(0.57735,0.57735,0.57735;2.0944rad)
  expr: Constraints[15] = .Constraints.hauteur * 0.1
  expr: Constraints[27] = .Constraints.epaisseur
  sketch-geometry (12):
    g0: LineSegment StartX=-10 StartY=12.5 StartZ=0 EndX=10 EndY=12.5 EndZ=0
    g1: LineSegment StartX=12.5 StartY=10 StartZ=0 EndX=12.5 EndY=-10 EndZ=0
    g2: LineSegment StartX=10 StartY=-12.5 StartZ=0 EndX=-10 EndY=-12.5 EndZ=0
    g3: LineSegment StartX=-12.5 StartY=-10 StartZ=0 EndX=-12.5 EndY=10 EndZ=0
    g4: ArcOfCircle CenterX=-10 CenterY=10 CenterZ=0 NormalX=0 NormalY=0 NormalZ=1 AngleXU=0 Radius=2.5 StartAngle=1.5708 EndAngle=3.14159
    g5: ArcOfCircle CenterX=10 CenterY=10 CenterZ=0 NormalX=0 NormalY=0 NormalZ=1 AngleXU=0 Radius=2.5 StartAngle=2e-16 EndAngle=1.5708
    g6: ArcOfCircle CenterX=10 CenterY=-10 CenterZ=0 NormalX=0 NormalY=0 NormalZ=1 AngleXU=0 Radius=2.5 StartAngle=4.71239 EndAngle=6.28319
    g7: ArcOfCircle CenterX=-10 CenterY=-10 CenterZ=0 NormalX=0 NormalY=0 NormalZ=1 AngleXU=0 Radius=2.5 StartAngle=3.14159 EndAngle=4.71239
    g8: LineSegment StartX=-10.5 StartY=10.5 StartZ=0 EndX=10.5 EndY=10.5 EndZ=0
    g9: LineSegment StartX=10.5 StartY=10.5 StartZ=0 EndX=10.5 EndY=-10.5 EndZ=0
    g10: LineSegment StartX=10.5 StartY=-10.5 StartZ=0 EndX=-10.5 EndY=-10.5 EndZ=0
    g11: LineSegment StartX=-10.5 StartY=-10.5 StartZ=0 EndX=-10.5 EndY=10.5 EndZ=0
  constraints (28):
    c: Horizontal(g2)
    c: Vertical(g3)
    c: Tangent(g0,g4) = 1.5708
    c: Tangent(g3,g4) = 1.5708
    c: Tangent(g0,g5) = 1.5708
    c: Tangent(g1,g5) = 1.5708
    c: Tangent(g1,g6) = 1.5708
    c: Tangent(g2,g6) = 1.5708
    c: Tangent(g2,g7) = 1.5708
    c: Tangent(g3,g7) = 1.5708
    c: Equal(g4,g5)
    c: DistanceY(g2,g0) = 25  'hauteur'
    c: DistanceX(g3,g1) = 25  'largeur'
    c: Equal(g5,g6)
    c: Equal(g6,g7)
    c: Radius(g7) = 2.5
    c: Symmetric(g1,g1,g-1)
    c: Symmetric(g0,g0,g-2)
    c: Coincident(g8,g9)
    c: Coincident(g9,g10)
    c: Coincident(g10,g11)
    c: Coincident(g11,g8)
    c: Horizontal(g10)
    c: Vertical(g11)
    c: Symmetric(g8,g9,g-1)
    c: Symmetric(g8,g8,g-2)
    c: DistanceX(g3,g8) = 2  'epaisseur'
    c: DistanceY(g2,g9) = 2
FEATURE [PartDesign::Pad] Pad004
  Direction = (1,1e-16,-1e-16)
  Length = 420
  Length2 = 100
  Placement = pos=(0,0,0) rot=(0.57735,0.57735,0.57735;2.0944rad)
  Profile = -> Sketch008
  Suppressed = false
  Type = 0
  expr: Length = Spreadsheet.D4 - Spreadsheet.B9 * 2
FEATURE [PartDesign::Body] Body006
  AllowCompound = false
  Group = -> [Sketch008,Pad004]
  Origin = -> Origin014
  Tip = -> Pad004
FEATURE [App::Part] A6
  Group = -> [LCS_0006,Body006]
  Nom_de_la_piece = 'A6
  Origin = -> Origin013
  Reference_AP = Tube carré 25 x 2
  longueur = 420
FEATURE [App::Link] A6001
  AssemblyType = Asm4EE
  AttachedBy = #LCS_0006
  AttachedTo = A5001#renfort
  AttachmentOffset = pos=(0,0,0) rot=(0,1,0;4.71239rad)
  LinkPlacement = pos=(1005,-210,-283.5) rot=(0.57735,0.57735,-0.57735;4.18879rad)
  LinkedObject = -> A6
  Placement = pos=(1005,-210,-283.5) rot=(0.57735,0.57735,-0.57735;4.18879rad)
  expr: Placement = A5001.Placement * renfort.Placement * AttachmentOffset * LCS_0006.Placement ^ -1
FEATURE [PartDesign::Body] A1005
  AllowCompound = false
  Origin = -> Origin015
FEATURE [PartDesign::CoordinateSystem] LCS_0007
  AttacherType = Attacher::AttachEngine3D
  AttachmentSupport = -> [X_Axis002]
  MapMode = 2
FEATURE [PartDesign::CoordinateSystem] cote2
  AttacherType = Attacher::AttachEngine3D
  AttachmentSupport = -> [Pad]
  MapMode = 5
  Placement = pos=(2285,1.0054e-12,0) rot=(0.57735,0.57735,0.57735;2.0944rad)
FEATURE [PartDesign::CoordinateSystem] faceA1
  AttacherType = Attacher::AttachEngine3D
  AttachmentOffset = pos=(12.5,980,0) rot=(0,0,1;0rad)
  AttachmentSupport = -> [Pad]
  MapMode = 5
  Placement = pos=(980,-12.5,-12.5) rot=(0.57735,0.57735,-0.57735;2.0944rad)
  expr: .AttachmentOffset.Base.x = Spreadsheet.B2 / 2
  expr: .AttachmentOffset.Base.y = (Spreadsheet.B4 - Spreadsheet.B2 * 2) / 2
FEATURE [PartDesign::CoordinateSystem] face2A1
  AttacherType = Attacher::AttachEngine3D
  AttachmentOffset = pos=(-12.5,980,0) rot=(0,0,1;0rad)
  AttachmentSupport = -> [Pad]
  MapMode = 5
  Placement = pos=(980,12.5,-12.5) rot=(0.57735,0.57735,0.57735;4.18879rad)
  expr: .AttachmentOffset.Base.x = -Spreadsheet.B2 / 2
  expr: .AttachmentOffset.Base.y = (Spreadsheet.B4 - Spreadsheet.B2 * 2) / 2
FEATURE [App::Part] A1
  Group = -> [A1005,LCS_0007,faceA1,face2A1,Pad,Sketch,cote2,LCS_0]
  Nom_de_la_piece = 'A1
  Origin = -> Origin002
  Reference_AP = Tube carré 25 x 2
  longueur = 2285
FEATURE [PartDesign::CoordinateSystem] LCS_0008
  AttacherType = Attacher::AttachEngine3D
  AttachmentSupport = -> [X_Axis016]
  MapMode = 2
FEATURE [PartDesign::CoordinateSystem] LCS_0010
  AttacherType = Attacher::AttachEngine3D
  AttachmentSupport = -> [X_Axis018]
  MapMode = 2
FEATURE [PartDesign::Body] A7002
  AllowCompound = false
FEATURE [PartDesign::CoordinateSystem] LCS_0011  label="cote004"
  AttacherType = Attacher::AttachEngine3D
  AttachmentSupport = -> [X_Axis018]
  MapMode = 2
FEATURE [Sketcher::SketchObject] Sketch009
  ArcFitTolerance = 0
  FullyConstrained = true
  MakeInternals = false
  MapMode = 5
  Placement = pos=(0,0,0) rot=(0.57735,0.57735,0.57735;2.0944rad)
  expr: Constraints[15] = .Constraints.hauteur * 0.1
  expr: Constraints[27] = .Constraints.epaisseur
  sketch-geometry (12):
    g0: LineSegment StartX=-10 StartY=12.5 StartZ=0 EndX=10 EndY=12.5 EndZ=0
    g1: LineSegment StartX=12.5 StartY=10 StartZ=0 EndX=12.5 EndY=-10 EndZ=0
    g2: LineSegment StartX=10 StartY=-12.5 StartZ=0 EndX=-10 EndY=-12.5 EndZ=0
    g3: LineSegment StartX=-12.5 StartY=-10 StartZ=0 EndX=-12.5 EndY=10 EndZ=0
    g4: ArcOfCircle CenterX=-10 CenterY=10 CenterZ=0 NormalX=0 NormalY=0 NormalZ=1 AngleXU=0 Radius=2.5 StartAngle=1.5708 EndAngle=3.14159
    g5: ArcOfCircle CenterX=10 CenterY=10 CenterZ=0 NormalX=0 NormalY=0 NormalZ=1 AngleXU=0 Radius=2.5 StartAngle=2e-16 EndAngle=1.5708
    g6: ArcOfCircle CenterX=10 CenterY=-10 CenterZ=0 NormalX=0 NormalY=0 NormalZ=1 AngleXU=0 Radius=2.5 StartAngle=4.71239 EndAngle=6.28319
    g7: ArcOfCircle CenterX=-10 CenterY=-10 CenterZ=0 NormalX=0 NormalY=0 NormalZ=1 AngleXU=0 Radius=2.5 StartAngle=3.14159 EndAngle=4.71239
    g8: LineSegment StartX=-10.5 StartY=10.5 StartZ=0 EndX=10.5 EndY=10.5 EndZ=0
    g9: LineSegment StartX=10.5 StartY=10.5 StartZ=0 EndX=10.5 EndY=-10.5 EndZ=0
    g10: LineSegment StartX=10.5 StartY=-10.5 StartZ=0 EndX=-10.5 EndY=-10.5 EndZ=0
    g11: LineSegment StartX=-10.5 StartY=-10.5 StartZ=0 EndX=-10.5 EndY=10.5 EndZ=0
  constraints (28):
    c: Horizontal(g2)
    c: Vertical(g3)
    c: Tangent(g0,g4) = 1.5708
    c: Tangent(g3,g4) = 1.5708
    c: Tangent(g0,g5) = 1.5708
    c: Tangent(g1,g5) = 1.5708
    c: Tangent(g1,g6) = 1.5708
    c: Tangent(g2,g6) = 1.5708
    c: Tangent(g2,g7) = 1.5708
    c: Tangent(g3,g7) = 1.5708
    c: Equal(g4,g5)
    c: DistanceY(g2,g0) = 25  'hauteur'
    c: DistanceX(g3,g1) = 25  'largeur'
    c: Equal(g5,g6)
    c: Equal(g6,g7)
    c: Radius(g7) = 2.5
    c: Symmetric(g1,g1,g-1)
    c: Symmetric(g0,g0,g-2)
    c: Coincident(g8,g9)
    c: Coincident(g9,g10)
    c: Coincident(g10,g11)
    c: Coincident(g11,g8)
    c: Horizontal(g10)
    c: Vertical(g11)
    c: Symmetric(g8,g9,g-1)
    c: Symmetric(g8,g8,g-2)
    c: DistanceX(g3,g8) = 2  'epaisseur'
    c: DistanceY(g2,g9) = 2
FEATURE [PartDesign::Pad] Pad005
  Direction = (1,1e-16,-1e-16)
  Length = 1960
  Length2 = 100
  Placement = pos=(0,0,0) rot=(0.57735,0.57735,0.57735;2.0944rad)
  Profile = -> Sketch009
  Suppressed = false
  Type = 0
  expr: Length = Spreadsheet.B4 - Spreadsheet.B2 * 2
FEATURE [PartDesign::CoordinateSystem] cote003
  AttacherType = Attacher::AttachEngine3D
  AttachmentSupport = -> [Pad005]
  MapMode = 5
  Placement = pos=(1960,8.624e-13,0) rot=(0.57735,0.57735,0.57735;2.0944rad)
FEATURE [PartDesign::CoordinateSystem] faceA002
  AttacherType = Attacher::AttachEngine3D
  AttachmentOffset = pos=(12.5,980,0) rot=(0,0,1;0rad)
  AttachmentSupport = -> [Pad005]
  MapMode = 5
  Placement = pos=(980,-12.5,-12.5) rot=(0.57735,0.57735,-0.57735;2.0944rad)
  expr: .AttachmentOffset.Base.x = Spreadsheet.B2 / 2
  expr: .AttachmentOffset.Base.y = (Spreadsheet.B4 - Spreadsheet.B2 * 2) / 2
FEATURE [PartDesign::CoordinateSystem] face2A002
  AttacherType = Attacher::AttachEngine3D
  AttachmentOffset = pos=(-12.5,980,0) rot=(0,0,1;0rad)
  AttachmentSupport = -> [Pad005]
  MapMode = 5
  Placement = pos=(980,12.5,-12.5) rot=(0.57735,0.57735,0.57735;4.18879rad)
  expr: .AttachmentOffset.Base.x = -Spreadsheet.B2 / 2
  expr: .AttachmentOffset.Base.y = (Spreadsheet.B4 - Spreadsheet.B2 * 2) / 2
FEATURE [App::Part] A7
  Group = -> [LCS_0008,A7002,LCS_0011,LCS_0010,X_Axis018,faceA002,face2A002,Pad005,Sketch009,cote003]
  Nom_de_la_piece = 'A7
  Origin = -> Origin016
  Reference_AP = Tube carré 25 x 2
  longueur = 1960
FEATURE [App::Link] A7003
  AssemblyType = Asm4EE
  AttachedBy = #LCS_0011
  AttachedTo = A2001#face2
  AttachmentOffset = pos=(0,0,0) rot=(0,1,0;4.71239rad)
  LinkPlacement = pos=(25,-97.5,-1.52e-14) rot=(0,0,1;0rad)
  LinkedObject = -> A7
  Placement = pos=(25,-97.5,-1.52e-14) rot=(0,0,1;0rad)
  expr: Placement = A2001.Placement * face2.Placement * AttachmentOffset * LCS_0011.Placement ^ -1
FEATURE [App::Link] A7004
  AssemblyType = Asm4EE
  AttachedBy = #LCS_0011
  AttachedTo = A2001#face3A2
  AttachmentOffset = pos=(0,0,0) rot=(0,1,0;4.71239rad)
  LinkPlacement = pos=(25,97.5,1e-16) rot=(0,0,1;0rad)
  LinkedObject = -> A7
  Placement = pos=(25,97.5,1e-16) rot=(0,0,1;0rad)
  expr: Placement = A2001.Placement * face3A2.Placement * AttachmentOffset * LCS_0011.Placement ^ -1
FEATURE [PartDesign::CoordinateSystem] LCS_0012
  AttacherType = Attacher::AttachEngine3D
  AttachmentSupport = -> [X_Axis019]
  MapMode = 2
FEATURE [PartDesign::CoordinateSystem] LCS_0013
  AttacherType = Attacher::AttachEngine3D
  AttachmentSupport = -> [X_Axis020]
  MapMode = 2
FEATURE [PartDesign::Body] A8001
  AllowCompound = false
  Group = -> [LCS_0013]
  Origin = -> Origin018
FEATURE [Sketcher::SketchObject] Sketch010
  ArcFitTolerance = 0
  FullyConstrained = true
  MakeInternals = false
  MapMode = 5
  expr: Constraints[15] = .Constraints.hauteur * 0.1
  expr: Constraints[27] = .Constraints.epaisseur
  sketch-geometry (12):
    g0: LineSegment StartX=-10 StartY=12.5 StartZ=0 EndX=10 EndY=12.5 EndZ=0
    g1: LineSegment StartX=12.5 StartY=10 StartZ=0 EndX=12.5 EndY=-10 EndZ=0
    g2: LineSegment StartX=10 StartY=-12.5 StartZ=0 EndX=-10 EndY=-12.5 EndZ=0
    g3: LineSegment StartX=-12.5 StartY=-10 StartZ=0 EndX=-12.5 EndY=10 EndZ=0
    g4: ArcOfCircle CenterX=-10 CenterY=10 CenterZ=0 NormalX=0 NormalY=0 NormalZ=1 AngleXU=0 Radius=2.5 StartAngle=1.5708 EndAngle=3.14159
    g5: ArcOfCircle CenterX=10 CenterY=10 CenterZ=0 NormalX=0 NormalY=0 NormalZ=1 AngleXU=0 Radius=2.5 StartAngle=2e-16 EndAngle=1.5708
    g6: ArcOfCircle CenterX=10 CenterY=-10 CenterZ=0 NormalX=0 NormalY=0 NormalZ=1 AngleXU=0 Radius=2.5 StartAngle=4.71239 EndAngle=6.28319
    g7: ArcOfCircle CenterX=-10 CenterY=-10 CenterZ=0 NormalX=0 NormalY=0 NormalZ=1 AngleXU=0 Radius=2.5 StartAngle=3.14159 EndAngle=4.71239
    g8: LineSegment StartX=-10.5 StartY=10.5 StartZ=0 EndX=10.5 EndY=10.5 EndZ=0
    g9: LineSegment StartX=10.5 StartY=10.5 StartZ=0 EndX=10.5 EndY=-10.5 EndZ=0
    g10: LineSegment StartX=10.5 StartY=-10.5 StartZ=0 EndX=-10.5 EndY=-10.5 EndZ=0
    g11: LineSegment StartX=-10.5 StartY=-10.5 StartZ=0 EndX=-10.5 EndY=10.5 EndZ=0
  constraints (28):
    c: Horizontal(g2)
    c: Vertical(g3)
    c: Tangent(g0,g4) = 1.5708
    c: Tangent(g3,g4) = 1.5708
    c: Tangent(g0,g5) = 1.5708
    c: Tangent(g1,g5) = 1.5708
    c: Tangent(g1,g6) = 1.5708
    c: Tangent(g2,g6) = 1.5708
    c: Tangent(g2,g7) = 1.5708
    c: Tangent(g3,g7) = 1.5708
    c: Equal(g4,g5)
    c: DistanceY(g2,g0) = 25  'hauteur'
    c: DistanceX(g3,g1) = 25  'largeur'
    c: Equal(g5,g6)
    c: Equal(g6,g7)
    c: Radius(g7) = 2.5
    c: Symmetric(g1,g1,g-1)
    c: Symmetric(g0,g0,g-2)
    c: Coincident(g8,g9)
    c: Coincident(g9,g10)
    c: Coincident(g10,g11)
    c: Coincident(g11,g8)
    c: Horizontal(g10)
    c: Vertical(g11)
    c: Symmetric(g8,g9,g-1)
    c: Symmetric(g8,g8,g-2)
    c: DistanceX(g3,g8) = 2  'epaisseur'
    c: DistanceY(g2,g9) = 2
FEATURE [PartDesign::Pad] Pad006
  Direction = (0,0,1)
  Length = 560
  Length2 = 100
  Profile = -> Sketch010
  Suppressed = false
  Type = 0
  expr: Length = Spreadsheet.D4 - Spreadsheet.B2 * 2
FEATURE [PartDesign::CoordinateSystem] face2A8
  AttacherType = Attacher::AttachEngine3D
  AttachmentOffset = pos=(0,182.5,0) rot=(0,0,1;0rad)
  AttachmentSupport = -> [Pad006]
  MapMode = 5
  Placement = pos=(12.5,0,182.5) rot=(0.57735,0.57735,0.57735;2.0944rad)
  expr: .AttachmentOffset.Base.y = (Spreadsheet.D4 - Spreadsheet.B2) * 1 / 3 - Spreadsheet.B2 / 2
FEATURE [App::Link] A8002
  AssemblyType = Asm4EE
  AttachedBy = #face2A8
  AttachedTo = A7003#cote003
  AttachmentOffset = pos=(0,0,0) rot=(-0.707107,-0.707107,0;3.14159rad)
  LinkPlacement = pos=(1997.5,-280,4.322e-13) rot=(0,0.707107,0.707107;3.14159rad)
  LinkedObject = -> A8
  Placement = pos=(1997.5,-280,4.322e-13) rot=(0,0.707107,0.707107;3.14159rad)
  expr: Placement = A7003.Placement * cote003.Placement * AttachmentOffset * face2A8.Placement ^ -1
FEATURE [Sketcher::SketchObject] Sketch011
  ArcFitTolerance = 0
  FullyConstrained = true
  MakeInternals = false
  MapMode = 5
  expr: Constraints[15] = .Constraints.hauteur * 0.1
  expr: Constraints[27] = .Constraints.epaisseur
  sketch-geometry (12):
    g0: LineSegment StartX=-10 StartY=12.5 StartZ=0 EndX=10 EndY=12.5 EndZ=0
    g1: LineSegment StartX=12.5 StartY=10 StartZ=0 EndX=12.5 EndY=-10 EndZ=0
    g2: LineSegment StartX=10 StartY=-12.5 StartZ=0 EndX=-10 EndY=-12.5 EndZ=0
    g3: LineSegment StartX=-12.5 StartY=-10 StartZ=0 EndX=-12.5 EndY=10 EndZ=0
    g4: ArcOfCircle CenterX=-10 CenterY=10 CenterZ=0 NormalX=0 NormalY=0 NormalZ=1 AngleXU=0 Radius=2.5 StartAngle=1.5708 EndAngle=3.14159
    g5: ArcOfCircle CenterX=10 CenterY=10 CenterZ=0 NormalX=0 NormalY=0 NormalZ=1 AngleXU=0 Radius=2.5 StartAngle=2e-16 EndAngle=1.5708
    g6: ArcOfCircle CenterX=10 CenterY=-10 CenterZ=0 NormalX=0 NormalY=0 NormalZ=1 AngleXU=0 Radius=2.5 StartAngle=4.71239 EndAngle=6.28319
    g7: ArcOfCircle CenterX=-10 CenterY=-10 CenterZ=0 NormalX=0 NormalY=0 NormalZ=1 AngleXU=0 Radius=2.5 StartAngle=3.14159 EndAngle=4.71239
    g8: LineSegment StartX=-10.5 StartY=10.5 StartZ=0 EndX=10.5 EndY=10.5 EndZ=0
    g9: LineSegment StartX=10.5 StartY=10.5 StartZ=0 EndX=10.5 EndY=-10.5 EndZ=0
    g10: LineSegment StartX=10.5 StartY=-10.5 StartZ=0 EndX=-10.5 EndY=-10.5 EndZ=0
    g11: LineSegment StartX=-10.5 StartY=-10.5 StartZ=0 EndX=-10.5 EndY=10.5 EndZ=0
  constraints (28):
    c: Horizontal(g2)
    c: Vertical(g3)
    c: Tangent(g0,g4) = 1.5708
    c: Tangent(g3,g4) = 1.5708
    c: Tangent(g0,g5) = 1.5708
    c: Tangent(g1,g5) = 1.5708
    c: Tangent(g1,g6) = 1.5708
    c: Tangent(g2,g6) = 1.5708
    c: Tangent(g2,g7) = 1.5708
    c: Tangent(g3,g7) = 1.5708
    c: Equal(g4,g5)
    c: DistanceY(g2,g0) = 25  'hauteur'
    c: DistanceX(g3,g1) = 25  'largeur'
    c: Equal(g5,g6)
    c: Equal(g6,g7)
    c: Radius(g7) = 2.5
    c: Symmetric(g1,g1,g-1)
    c: Symmetric(g0,g0,g-2)
    c: Coincident(g8,g9)
    c: Coincident(g9,g10)
    c: Coincident(g10,g11)
    c: Coincident(g11,g8)
    c: Horizontal(g10)
    c: Vertical(g11)
    c: Symmetric(g8,g9,g-1)
    c: Symmetric(g8,g8,g-2)
    c: DistanceX(g3,g8) = 2  'epaisseur'
    c: DistanceY(g2,g9) = 2
FEATURE [PartDesign::Pad] Pad007
  Direction = (0,0,1)
  Length = 215
  Length2 = 100
  Profile = -> Sketch011
  Suppressed = false
  Type = 0
  expr: Length = Spreadsheet.B11 - Spreadsheet.B5 - Spreadsheet.B2 * 2
FEATURE [PartDesign::CoordinateSystem] LCS_0014
  AttacherType = Attacher::AttachEngine3D
  AttachmentSupport = -> [X_Axis021]
  MapMode = 2
FEATURE [PartDesign::CoordinateSystem] LCS_0015
  AttacherType = Attacher::AttachEngine3D
  AttachmentOffset = pos=(0,-12.5,0) rot=(0,0,1;0rad)
  AttachmentSupport = -> [X_Axis022]
  MapMode = 2
  Placement = pos=(0,-12.5,0) rot=(0,0,1;0rad)
  expr: .AttachmentOffset.Base.y = -Spreadsheet.B2 / 2
FEATURE [PartDesign::CoordinateSystem] cote2001
  AttacherType = Attacher::AttachEngine3D
  AttachmentOffset = pos=(0,12.5,8.29156) rot=(0,0,1;0rad)
  AttachmentSupport = -> [Pad007]
  MapMode = 5
  Placement = pos=(0,12.5,223.292) rot=(0,0,1;0rad)
  expr: .AttachmentOffset.Base.y = Spreadsheet.B2 / 2
  expr: .AttachmentOffset.Base.z = Sketch023.Constraints.deport
FEATURE [App::Link] A9  label="A8005"
  AssemblyType = Asm4EE
  AttachedBy = #LCS_0015
  AttachedTo = A1001#cote2
  AttachmentOffset = pos=(0,12.5,0) rot=(-1,0,0;1.5708rad)
  LinkPlacement = pos=(2297.5,-292.5,12.5) rot=(0,0,1;1.5708rad)
  LinkedObject = -> A8003
  Placement = pos=(2297.5,-292.5,12.5) rot=(0,0,1;1.5708rad)
  expr: .AttachmentOffset.Base.y = Spreadsheet.B2 / 2
  expr: Placement = A1001.Placement * cote2.Placement * AttachmentOffset * LCS_0015.Placement ^ -1
FEATURE [App::Link] A9001
  AssemblyType = Asm4EE
  AttachedBy = #LCS_0015
  AttachedTo = A1004#cote2
  AttachmentOffset = pos=(0,12.5,0) rot=(-1,0,0;1.5708rad)
  LinkPlacement = pos=(2297.5,292.5,12.5) rot=(0,0,1;1.5708rad)
  LinkedObject = -> A8003
  Placement = pos=(2297.5,292.5,12.5) rot=(0,0,1;1.5708rad)
  expr: .AttachmentOffset.Base.y = Spreadsheet.B2 / 2
  expr: Placement = A1004.Placement * cote2.Placement * AttachmentOffset * LCS_0015.Placement ^ -1
FEATURE [Sketcher::SketchObject] Sketch012
  ArcFitTolerance = 0
  AttachmentSupport = -> [XZ_Plane022]
  FullyConstrained = true
  MakeInternals = false
  MapMode = 5
  Placement = pos=(0,0,0) rot=(1,0,0;1.5708rad)
  sketch-geometry (1):
    g0: Circle CenterX=0 CenterY=0 CenterZ=0 NormalX=0 NormalY=0 NormalZ=1 AngleXU=0 Radius=12.5
  constraints (2):
    c: Coincident(g0,g-1)
    c: Diameter(g0) = 25  'diametre'
FEATURE [PartDesign::Pad] Pad008
  Direction = (0,-1,2e-16)
  Length = 150
  Length2 = 100
  Placement = pos=(0,0,0) rot=(1,0,0;1.5708rad)
  Profile = -> Sketch012
  Suppressed = false
  Type = 0
FEATURE [Sketcher::SketchObject] Sketch013
  ArcFitTolerance = 0
  AttachmentSupport = -> [XZ_Plane024]
  FullyConstrained = true
  MakeInternals = false
  MapMode = 5
  Placement = pos=(0,0,0) rot=(1,0,0;1.5708rad)
  expr: Constraints[22] = .Constraints.epaisseur
  expr: Constraints[24] = .Constraints.largeur * 20 / 100
  sketch-geometry (10):
    g0: LineSegment StartX=-15 StartY=15 StartZ=0 EndX=-15 EndY=0 EndZ=0
    g1: LineSegment StartX=-15 StartY=0 StartZ=0 EndX=15 EndY=0 EndZ=0
    g2: LineSegment StartX=15 StartY=0 StartZ=0 EndX=15 EndY=15 EndZ=0
    g3: LineSegment StartX=15 StartY=15 StartZ=0 EndX=14 EndY=15 EndZ=0
    g4: LineSegment StartX=11 StartY=12 StartZ=0 EndX=11 EndY=4 EndZ=0
    g5: LineSegment StartX=11 StartY=4 StartZ=0 EndX=-11 EndY=4 EndZ=0
    g6: LineSegment StartX=-11 StartY=4 StartZ=0 EndX=-11 EndY=12 EndZ=0
    g7: LineSegment StartX=-14 StartY=15 StartZ=0 EndX=-15 EndY=15 EndZ=0
    g8: ArcOfCircle CenterX=-14 CenterY=12 CenterZ=0 NormalX=0 NormalY=0 NormalZ=1 AngleXU=0 Radius=3 StartAngle=0 EndAngle=1.5708
    g9: ArcOfCircle CenterX=14 CenterY=12 CenterZ=0 NormalX=0 NormalY=0 NormalZ=1 AngleXU=0 Radius=3 StartAngle=1.5708 EndAngle=3.14159
  constraints (25):
    c: PointOnObject(g0,g-1)
    c: Vertical(g0)
    c: Coincident(g0,g1)
    c: Coincident(g1,g2)
    c: Coincident(g2,g3)
    c: Horizontal(g3)
    c: Vertical(g4)
    c: Coincident(g4,g5)
    c: Coincident(g5,g6)
    c: Coincident(g7,g0)
    c: Horizontal(g7)
    c: Symmetric(g1,g0,g-2)
    c: Symmetric(g5,g4,g-2)
    c: Tangent(g6,g8) = -1.5708
    c: Tangent(g7,g8) = -1.5708
    c: Tangent(g3,g9) = -1.5708
    c: Tangent(g4,g9) = -1.5708
    c: Equal(g8,g9)
    c: Symmetric(g0,g2,g-2)
    c: Vertical(g6)
    c: DistanceX(g1,g1) = 30  'largeur'
    c: DistanceY(g2,g2) = 15  'hauteur'
    c: DistanceY(g1,g4) = 4
    c: DistanceX(g4,g1) = 4  'epaisseur'
    c: Diameter(g8) = 6
FEATURE [PartDesign::Pad] Pad009
  Direction = (0,-1,2e-16)
  Length = 46
  Length2 = 100
  Placement = pos=(0,0,0) rot=(1,0,0;1.5708rad)
  Profile = -> Sketch013
  Suppressed = false
  Type = 0
FEATURE [PartDesign::Body] Body007
  AllowCompound = false
  Group = -> [Sketch013,Pad009]
  Origin = -> Origin024
  Tip = -> Pad009
FEATURE [Sketcher::SketchObject] Sketch014
  ArcFitTolerance = 0
  FullyConstrained = false
  MakeInternals = false
  Placement = pos=(0,-305,0) rot=(1,0,0;1.5708rad)
  expr: .Constraints.hpied = Spreadsheet.B5 - 100
  expr: Constraints[12] = .Constraints.lar / 2
  expr: Constraints[15] = Spreadsheet.B2
  expr: Constraints[33] = Pad003.Length
  expr: Constraints[5] = Spreadsheet.B2 / 2
  expr: Constraints[7] = Spreadsheet.B2
  sketch-geometry (14):
    g0: LineSegment StartX=25 StartY=-12.5 StartZ=0 EndX=25 EndY=-412.5 EndZ=0
    g1: LineSegment StartX=25 StartY=-412.5 StartZ=0 EndX=273.106 EndY=-37.5 EndZ=0
    g2: LineSegment StartX=1736.89 StartY=-37.5 StartZ=0 EndX=1985 EndY=-412.5 EndZ=0
    g3: LineSegment StartX=1985 StartY=-412.5 StartZ=0 EndX=1985 EndY=-12.5 EndZ=0
    g4: LineSegment [constr] StartX=-267.829 StartY=-37.5 StartZ=0 EndX=2303.14 EndY=-37.5 EndZ=0
    g5: LineSegment [constr] StartX=1005 StartY=302.788 StartZ=0 EndX=1005 EndY=-538.691 EndZ=0
    g6: LineSegment StartX=1017.5 StartY=-269.453 StartZ=0 EndX=1736.89 EndY=-12.5 EndZ=0
    g7: LineSegment StartX=992.5 StartY=-269.453 StartZ=0 EndX=273.106 EndY=-12.5 EndZ=0
    g8: LineSegment StartX=1985 StartY=-412.5 StartZ=0 EndX=2216.18 EndY=-12.5 EndZ=0
    g9: LineSegment [constr] StartX=1736.89 StartY=-37.5 StartZ=0 EndX=1736.89 EndY=33.5143 EndZ=0
    g10: LineSegment [constr] StartX=1017.5 StartY=-296 StartZ=0 EndX=1200.58 EndY=-230.607 EndZ=0
    g11: LineSegment [constr] StartX=1017.5 StartY=-269.453 StartZ=0 EndX=1017.5 EndY=-296 EndZ=0
    g12: GeomPoint [constr] X=248.106 Y=-12.5 Z=0
    g13: LineSegment [constr] StartX=1017.5 StartY=-269.453 StartZ=0 EndX=1025.91 EndY=-292.996 EndZ=0
  constraints (40):
    c: Vertical(g0)
    c: Coincident(g0,g1)
    c: Coincident(g2,g3)
    c: Vertical(g3)
    c: Equal(g0,g3)
    c: DistanceY(g0,g-1) = 12.5
    c: DistanceX(g0,g2) = 1960  'lar'
    c: DistanceX(g-1,g0) = 25
    c: DistanceY(g0,g0) = 400  'hpied'
    c: Horizontal(g4)
    c: PointOnObject(g1,g4)
    c: PointOnObject(g2,g4)
    c: DistanceX(g0,g5) = 980
    c: Symmetric(g1,g2,g5)
    c: Symmetric(g7,g6,g5)
    c: DistanceX(g7,g6) = 25
    c: Distance(g1) = 449.646  'lpied'
    c: Distance(g6) = 763.906  'ldiag'
    c: Angle(g3,g2) = 0.584499  'angle'
    c: Angle(g5,g7) = 1.22774  'anglerou'
    c: DistanceX(g-1,g2) = 1736.89  'b2'
    c: Coincident(g8,g2)
    c: Angle(g8,g3) = 0.524048  'angle2'
    c: Distance(g8) = 462  'l2pied'
    c: Symmetric(g7,g6,g5)
    c: Vertical(g9)
    c: PointOnObject(g6,g9)
    c: Coincident(g9,g2)
    c: Parallel(g6,g10)
    c: Distance(g10,g6) = 25
    c: Coincident(g11,g6)
    c: Coincident(g11,g10)
    c: Vertical(g11)
    c: Distance(g10,g4) = 258.5
    c: Distance(g12,g7) = 25
    c: Distance(g12,g-2) = 248.106  'b1'
    c: Coincident(g13,g6)
    c: PointOnObject(g13,g10)
    c: Perpendicular(g13,g10)
    c: Distance(g10,g13) = 8.92951  'rajoueroue'
FEATURE [PartDesign::Body] Body008
  AllowCompound = false
  Origin = -> Origin028
FEATURE [Sketcher::SketchObject] Sketch015
  ArcFitTolerance = 0
  FullyConstrained = true
  MakeInternals = false
  MapMode = 5
  Placement = pos=(0,0,0) rot=(0.57735,0.57735,0.57735;2.0944rad)
  expr: Constraints[15] = .Constraints.hauteur * 0.1
  expr: Constraints[27] = .Constraints.epaisseur
  sketch-geometry (12):
    g0: LineSegment StartX=-10 StartY=12.5 StartZ=0 EndX=10 EndY=12.5 EndZ=0
    g1: LineSegment StartX=12.5 StartY=10 StartZ=0 EndX=12.5 EndY=-10 EndZ=0
    g2: LineSegment StartX=10 StartY=-12.5 StartZ=0 EndX=-10 EndY=-12.5 EndZ=0
    g3: LineSegment StartX=-12.5 StartY=-10 StartZ=0 EndX=-12.5 EndY=10 EndZ=0
    g4: ArcOfCircle CenterX=-10 CenterY=10 CenterZ=0 NormalX=0 NormalY=0 NormalZ=1 AngleXU=0 Radius=2.5 StartAngle=1.5708 EndAngle=3.14159
    g5: ArcOfCircle CenterX=10 CenterY=10 CenterZ=0 NormalX=0 NormalY=0 NormalZ=1 AngleXU=0 Radius=2.5 StartAngle=2e-16 EndAngle=1.5708
    g6: ArcOfCircle CenterX=10 CenterY=-10 CenterZ=0 NormalX=0 NormalY=0 NormalZ=1 AngleXU=0 Radius=2.5 StartAngle=4.71239 EndAngle=6.28319
    g7: ArcOfCircle CenterX=-10 CenterY=-10 CenterZ=0 NormalX=0 NormalY=0 NormalZ=1 AngleXU=0 Radius=2.5 StartAngle=3.14159 EndAngle=4.71239
    g8: LineSegment StartX=-10.5 StartY=10.5 StartZ=0 EndX=10.5 EndY=10.5 EndZ=0
    g9: LineSegment StartX=10.5 StartY=10.5 StartZ=0 EndX=10.5 EndY=-10.5 EndZ=0
    g10: LineSegment StartX=10.5 StartY=-10.5 StartZ=0 EndX=-10.5 EndY=-10.5 EndZ=0
    g11: LineSegment StartX=-10.5 StartY=-10.5 StartZ=0 EndX=-10.5 EndY=10.5 EndZ=0
  constraints (28):
    c: Horizontal(g2)
    c: Vertical(g3)
    c: Tangent(g0,g4) = 1.5708
    c: Tangent(g3,g4) = 1.5708
    c: Tangent(g0,g5) = 1.5708
    c: Tangent(g1,g5) = 1.5708
    c: Tangent(g1,g6) = 1.5708
    c: Tangent(g2,g6) = 1.5708
    c: Tangent(g2,g7) = 1.5708
    c: Tangent(g3,g7) = 1.5708
    c: Equal(g4,g5)
    c: DistanceY(g2,g0) = 25  'hauteur'
    c: DistanceX(g3,g1) = 25  'largeur'
    c: Equal(g5,g6)
    c: Equal(g6,g7)
    c: Radius(g7) = 2.5
    c: Symmetric(g1,g1,g-1)
    c: Symmetric(g0,g0,g-2)
    c: Coincident(g8,g9)
    c: Coincident(g9,g10)
    c: Coincident(g10,g11)
    c: Coincident(g11,g8)
    c: Horizontal(g10)
    c: Vertical(g11)
    c: Symmetric(g8,g9,g-1)
    c: Symmetric(g8,g8,g-2)
    c: DistanceX(g3,g8) = 2  'epaisseur'
    c: DistanceY(g2,g9) = 2
FEATURE [PartDesign::Pad] Pad010
  Direction = (1,1e-16,-1e-16)
  Length = 400
  Length2 = 100
  Placement = pos=(0,0,0) rot=(0.57735,0.57735,0.57735;2.0944rad)
  Profile = -> Sketch015
  Suppressed = false
  Type = 0
  expr: Length = Sketch014.Constraints.hpied
FEATURE [Sketcher::SketchObject] Sketch016
  ArcFitTolerance = 0
  FullyConstrained = true
  MakeInternals = false
  MapMode = 5
  Placement = pos=(0,0,0) rot=(0.57735,0.57735,0.57735;2.0944rad)
  expr: Constraints[15] = .Constraints.hauteur * 0.1
  expr: Constraints[27] = .Constraints.epaisseur
  sketch-geometry (12):
    g0: LineSegment StartX=-10 StartY=12.5 StartZ=0 EndX=10 EndY=12.5 EndZ=0
    g1: LineSegment StartX=12.5 StartY=10 StartZ=0 EndX=12.5 EndY=-10 EndZ=0
    g2: LineSegment StartX=10 StartY=-12.5 StartZ=0 EndX=-10 EndY=-12.5 EndZ=0
    g3: LineSegment StartX=-12.5 StartY=-10 StartZ=0 EndX=-12.5 EndY=10 EndZ=0
    g4: ArcOfCircle CenterX=-10 CenterY=10 CenterZ=0 NormalX=0 NormalY=0 NormalZ=1 AngleXU=0 Radius=2.5 StartAngle=1.5708 EndAngle=3.14159
    g5: ArcOfCircle CenterX=10 CenterY=10 CenterZ=0 NormalX=0 NormalY=0 NormalZ=1 AngleXU=0 Radius=2.5 StartAngle=2e-16 EndAngle=1.5708
    g6: ArcOfCircle CenterX=10 CenterY=-10 CenterZ=0 NormalX=0 NormalY=0 NormalZ=1 AngleXU=0 Radius=2.5 StartAngle=4.71239 EndAngle=6.28319
    g7: ArcOfCircle CenterX=-10 CenterY=-10 CenterZ=0 NormalX=0 NormalY=0 NormalZ=1 AngleXU=0 Radius=2.5 StartAngle=3.14159 EndAngle=4.71239
    g8: LineSegment StartX=-10.5 StartY=10.5 StartZ=0 EndX=10.5 EndY=10.5 EndZ=0
    g9: LineSegment StartX=10.5 StartY=10.5 StartZ=0 EndX=10.5 EndY=-10.5 EndZ=0
    g10: LineSegment StartX=10.5 StartY=-10.5 StartZ=0 EndX=-10.5 EndY=-10.5 EndZ=0
    g11: LineSegment StartX=-10.5 StartY=-10.5 StartZ=0 EndX=-10.5 EndY=10.5 EndZ=0
  constraints (28):
    c: Horizontal(g2)
    c: Vertical(g3)
    c: Tangent(g0,g4) = 1.5708
    c: Tangent(g3,g4) = 1.5708
    c: Tangent(g0,g5) = 1.5708
    c: Tangent(g1,g5) = 1.5708
    c: Tangent(g1,g6) = 1.5708
    c: Tangent(g2,g6) = 1.5708
    c: Tangent(g2,g7) = 1.5708
    c: Tangent(g3,g7) = 1.5708
    c: Equal(g4,g5)
    c: DistanceY(g2,g0) = 25  'hauteur'
    c: DistanceX(g3,g1) = 25  'largeur'
    c: Equal(g5,g6)
    c: Equal(g6,g7)
    c: Radius(g7) = 2.5
    c: Symmetric(g1,g1,g-1)
    c: Symmetric(g0,g0,g-2)
    c: Coincident(g8,g9)
    c: Coincident(g9,g10)
    c: Coincident(g10,g11)
    c: Coincident(g11,g8)
    c: Horizontal(g10)
    c: Vertical(g11)
    c: Symmetric(g8,g9,g-1)
    c: Symmetric(g8,g8,g-2)
    c: DistanceX(g3,g8) = 2  'epaisseur'
    c: DistanceY(g2,g9) = 2
FEATURE [PartDesign::Pad] Pad011
  Direction = (1,1e-16,-1e-16)
  Length = 449.646
  Length2 = 100
  Placement = pos=(0,0,0) rot=(0.57735,0.57735,0.57735;2.0944rad)
  Profile = -> Sketch016
  Suppressed = false
  Type = 0
  expr: Length = Sketch014.Constraints.lpied
FEATURE [Sketcher::SketchObject] Sketch017
  ArcFitTolerance = 0
  FullyConstrained = true
  MakeInternals = false
  MapMode = 5
  Placement = pos=(0,0,0) rot=(0.57735,0.57735,0.57735;2.0944rad)
  expr: Constraints[15] = .Constraints.hauteur * 0.1
  expr: Constraints[27] = .Constraints.epaisseur
  sketch-geometry (12):
    g0: LineSegment StartX=-10 StartY=12.5 StartZ=0 EndX=10 EndY=12.5 EndZ=0
    g1: LineSegment StartX=12.5 StartY=10 StartZ=0 EndX=12.5 EndY=-10 EndZ=0
    g2: LineSegment StartX=10 StartY=-12.5 StartZ=0 EndX=-10 EndY=-12.5 EndZ=0
    g3: LineSegment StartX=-12.5 StartY=-10 StartZ=0 EndX=-12.5 EndY=10 EndZ=0
    g4: ArcOfCircle CenterX=-10 CenterY=10 CenterZ=0 NormalX=0 NormalY=0 NormalZ=1 AngleXU=0 Radius=2.5 StartAngle=1.5708 EndAngle=3.14159
    g5: ArcOfCircle CenterX=10 CenterY=10 CenterZ=0 NormalX=0 NormalY=0 NormalZ=1 AngleXU=0 Radius=2.5 StartAngle=2e-16 EndAngle=1.5708
    g6: ArcOfCircle CenterX=10 CenterY=-10 CenterZ=0 NormalX=0 NormalY=0 NormalZ=1 AngleXU=0 Radius=2.5 StartAngle=4.71239 EndAngle=6.28319
    g7: ArcOfCircle CenterX=-10 CenterY=-10 CenterZ=0 NormalX=0 NormalY=0 NormalZ=1 AngleXU=0 Radius=2.5 StartAngle=3.14159 EndAngle=4.71239
    g8: LineSegment StartX=-10.5 StartY=10.5 StartZ=0 EndX=10.5 EndY=10.5 EndZ=0
    g9: LineSegment StartX=10.5 StartY=10.5 StartZ=0 EndX=10.5 EndY=-10.5 EndZ=0
    g10: LineSegment StartX=10.5 StartY=-10.5 StartZ=0 EndX=-10.5 EndY=-10.5 EndZ=0
    g11: LineSegment StartX=-10.5 StartY=-10.5 StartZ=0 EndX=-10.5 EndY=10.5 EndZ=0
  constraints (28):
    c: Horizontal(g2)
    c: Vertical(g3)
    c: Tangent(g0,g4) = 1.5708
    c: Tangent(g3,g4) = 1.5708
    c: Tangent(g0,g5) = 1.5708
    c: Tangent(g1,g5) = 1.5708
    c: Tangent(g1,g6) = 1.5708
    c: Tangent(g2,g6) = 1.5708
    c: Tangent(g2,g7) = 1.5708
    c: Tangent(g3,g7) = 1.5708
    c: Equal(g4,g5)
    c: DistanceY(g2,g0) = 25  'hauteur'
    c: DistanceX(g3,g1) = 25  'largeur'
    c: Equal(g5,g6)
    c: Equal(g6,g7)
    c: Radius(g7) = 2.5
    c: Symmetric(g1,g1,g-1)
    c: Symmetric(g0,g0,g-2)
    c: Coincident(g8,g9)
    c: Coincident(g9,g10)
    c: Coincident(g10,g11)
    c: Coincident(g11,g8)
    c: Horizontal(g10)
    c: Vertical(g11)
    c: Symmetric(g8,g9,g-1)
    c: Symmetric(g8,g8,g-2)
    c: DistanceX(g3,g8) = 2  'epaisseur'
    c: DistanceY(g2,g9) = 2
FEATURE [PartDesign::Pad] Pad012
  Direction = (1,1e-16,-1e-16)
  Length = 772.835
  Length2 = 100
  Placement = pos=(0,0,0) rot=(0.57735,0.57735,0.57735;2.0944rad)
  Profile = -> Sketch017
  ReferenceAxis = -> Sketch017 [N_Axis]
  Suppressed = false
  Type = 0
  expr: Length = Sketch014.Constraints.ldiag + Sketch014.Constraints.rajoueroue
FEATURE [PartDesign::CoordinateSystem] B1
  AttacherType = Attacher::AttachEngine3D
  AttachmentSupport = -> [Pad010]
  MapMode = 5
  Placement = pos=(400,1.76e-13,0) rot=(0.57735,0.57735,0.57735;2.0944rad)
FEATURE [PartDesign::CoordinateSystem] B2
  AttacherType = Attacher::AttachEngine3D
  AttachmentSupport = -> [Pad010]
  MapMode = 5
  Placement = pos=(0,0,0) rot=(0.57735,0.57735,-0.57735;4.18879rad)
FEATURE [PartDesign::CoordinateSystem] B1001
  AttacherType = Attacher::AttachEngine3D
  AttachmentOffset = pos=(0,-12.5,0) rot=(0,0,1;0rad)
  AttachmentSupport = -> [Pad011]
  MapMode = 5
  Placement = pos=(0,0,12.5) rot=(0.57735,0.57735,-0.57735;4.18879rad)
  expr: .AttachmentOffset.Base.y = -12.5
FEATURE [PartDesign::CoordinateSystem] B2001
  AttacherType = Attacher::AttachEngine3D
  AttachmentOffset = pos=(0,12.5,0) rot=(0,0,1;0rad)
  AttachmentSupport = -> [Pad011]
  MapMode = 5
  Placement = pos=(449.646,1.978e-13,12.5) rot=(0.57735,0.57735,0.57735;2.0944rad)
FEATURE [PartDesign::CoordinateSystem] B1002
  AttacherType = Attacher::AttachEngine3D
  AttachmentSupport = -> [Pad012]
  MapMode = 5
  Placement = pos=(0,0,0) rot=(0.57735,0.57735,-0.57735;4.18879rad)
FEATURE [PartDesign::CoordinateSystem] B2002
  AttacherType = Attacher::AttachEngine3D
  AttachmentSupport = -> [Pad012]
  MapMode = 5
  Placement = pos=(772.835,3.4e-13,0) rot=(0.57735,0.57735,0.57735;2.0944rad)
FEATURE [App::Link] A12  label="A9002"
  AssemblyType = Asm4EE
  AttachedBy = #B1
  AttachedTo = A2001#LCS_0001
  AttachmentOffset = pos=(12.5,0,12.5) rot=(0,1,0;3.14159rad)
  LinkPlacement = pos=(12.5,-292.5,-412.5) rot=(-0.707107,0,-0.707107;3.14159rad)
  LinkedObject = -> Part002
  Placement = pos=(12.5,-292.5,-412.5) rot=(-0.707107,0,-0.707107;3.14159rad)
  expr: .AttachmentOffset.Base.x = Spreadsheet.B2 / 2
  expr: .AttachmentOffset.Base.z = Spreadsheet.B2 / 2
  expr: Placement = A2001.Placement * LCS_0001.Placement * AttachmentOffset * B1.Placement ^ -1
FEATURE [App::Link] A12001
  AssemblyType = Asm4EE
  AttachedBy = #B1
  AttachedTo = A2001#cote2A2
  AttachmentOffset = pos=(0,12.5,-12.5) rot=(-0.57735,-0.57735,0.57735;4.18879rad)
  LinkPlacement = pos=(12.5,292.5,-412.5) rot=(0.707107,0,0.707107;3.14159rad)
  LinkedObject = -> Part002
  Placement = pos=(12.5,292.5,-412.5) rot=(0.707107,0,0.707107;3.14159rad)
  expr: .AttachmentOffset.Base.y = Spreadsheet.B2 / 2
  expr: .AttachmentOffset.Base.z = -Spreadsheet.B2 / 2
  expr: Placement = A2001.Placement * cote2A2.Placement * AttachmentOffset * B1.Placement ^ -1
FEATURE [App::Link] A12002  label="A12004"
  AssemblyType = Asm4EE
  AttachedBy = #B1
  AttachedTo = A8002#LCS_0012
  AttachmentOffset = pos=(0,-12.5,-12.5) rot=(-1,0,0;1.5708rad)
  LinkPlacement = pos=(1997.5,-292.5,-412.5) rot=(0.57735,-0.57735,0.57735;2.0944rad)
  LinkedObject = -> Part002
  Placement = pos=(1997.5,-292.5,-412.5) rot=(0.57735,-0.57735,0.57735;2.0944rad)
  expr: .AttachmentOffset.Base.y = -Spreadsheet.B2 / 2
  expr: .AttachmentOffset.Base.z = -Spreadsheet.B2 / 2
  expr: Placement = A8002.Placement * LCS_0012.Placement * AttachmentOffset * B1.Placement ^ -1
FEATURE [PartDesign::CoordinateSystem] cote2002
  AttacherType = Attacher::AttachEngine3D
  AttachmentSupport = -> [Pad006]
  MapMode = 5
  Placement = pos=(0,0,560) rot=(0,0,1;0rad)
FEATURE [App::Part] A8
  Group = -> [LCS_0012,A8001,Pad006,cote2002,Sketch010,face2A8]
  Nom_de_la_piece = 'A8
  Origin = -> Origin017
  Reference_AP = Tube carré 25 x 2
  longueur = 560
FEATURE [App::Link] A12003  label="A12005"
  AssemblyType = Asm4EE
  AttachedBy = #B1
  AttachedTo = A8002#cote2002
  AttachmentOffset = pos=(0,-12.5,12.5) rot=(-1,0,0;1.5708rad)
  LinkPlacement = pos=(1997.5,292.5,-412.5) rot=(0.57735,-0.57735,0.57735;2.0944rad)
  LinkedObject = -> Part002
  Placement = pos=(1997.5,292.5,-412.5) rot=(0.57735,-0.57735,0.57735;2.0944rad)
  expr: .AttachmentOffset.Base.y = -Spreadsheet.B2 / 2
  expr: .AttachmentOffset.Base.z = Spreadsheet.B2 / 2
  expr: Placement = A8002.Placement * cote2002.Placement * AttachmentOffset * B1.Placement ^ -1
FEATURE [App::Link] A13001
  AssemblyType = Asm4EE
  AttachedBy = #B1001
  AttachedTo = A12002#B2
  AttachmentOffset = pos=(12.5,0,0) rot=(-0.276846,-0.276846,0.92017;1.6539rad)
  LinkPlacement = pos=(1995.42,-292.5,-405.603) rot=(0,1,0;4.12789rad)
  LinkedObject = -> Part003
  Placement = pos=(1995.42,-292.5,-405.603) rot=(0,1,0;4.12789rad)
  expr: .AttachmentOffset.Rotation.Roll = -Sketch014.Constraints.angle
  expr: Placement = A12002.Placement * B2.Placement * AttachmentOffset * B1001.Placement ^ -1
FEATURE [App::Link] A14001
  AssemblyType = Asm4EE
  AttachedBy = #B1002
  AttachedTo = A6001#LCS_0006
  AttachmentOffset = pos=(-12.5,0.72,-8.3) rot=(-1,0,0;0.343057rad)
  LinkPlacement = pos=(1013.3,-222.5,-284.22) rot=(0,1,0;5.94013rad)
  LinkedObject = -> Part004
  Placement = pos=(1013.3,-222.5,-284.22) rot=(0,1,0;5.94013rad)
  expr: .AttachmentOffset.Base.x = -Spreadsheet.B2 / 2
  expr: .AttachmentOffset.Rotation.Roll = -(90 ° - Sketch014.Constraints.anglerou)
  expr: Placement = A6001.Placement * LCS_0006.Placement * AttachmentOffset * B1002.Placement ^ -1
FEATURE [App::Link] A2004
  AssemblyType = Asm4EE
  AttachedBy = #LCS_0001
  AttachedTo = A1001#LCS_0
  AttachmentOffset = pos=(235.606,-12.5,-25) rot=(0,0,1;1.5708rad)
  LinkPlacement = pos=(260.606,-305,-25) rot=(0,0,1;1.5708rad)
  LinkedObject = -> A2
  Placement = pos=(260.606,-305,-25) rot=(0,0,1;1.5708rad)
  expr: .AttachmentOffset.Base.x = Sketch014.Constraints.b1 - 1 mm * Spreadsheet.B2 / 2
  expr: .AttachmentOffset.Base.y = -Spreadsheet.B2 / 2
  expr: .AttachmentOffset.Base.z = -Spreadsheet.B2
  expr: Placement = A1001.Placement * LCS_0.Placement * AttachmentOffset * LCS_0001.Placement ^ -1
FEATURE [App::Link] A2005
  AssemblyType = Asm4EE
  AttachedBy = #LCS_0001
  AttachedTo = A2001#LCS_0001
  AttachmentOffset = pos=(0,1736.89,25) rot=(0,0,1;0rad)
  LinkPlacement = pos=(1749.39,-305,-25) rot=(-0.707107,-0.707107,0;3.14159rad)
  LinkedObject = -> A2
  Placement = pos=(1749.39,-305,-25) rot=(-0.707107,-0.707107,0;3.14159rad)
  expr: .AttachmentOffset.Base.y = Sketch014.Constraints.b2
  expr: .AttachmentOffset.Base.z = Spreadsheet.B2
  expr: Placement = A2001.Placement * LCS_0001.Placement * AttachmentOffset * LCS_0001.Placement ^ -1
FEATURE [PartDesign::CoordinateSystem] cote2003
  AttacherType = Attacher::AttachEngine3D
  AttachmentSupport = -> [Pad003]
  MapMode = 5
  Placement = pos=(258.5,1.137e-13,0) rot=(0.57735,0.57735,0.57735;2.0944rad)
FEATURE [App::Part] A5
  Group = -> [LCS_0005,Body005,renfort,Pad003,Sketch007,cote2003]
  Nom_de_la_piece = 'A5
  Origin = -> Origin011
  Reference_AP = Tube carré 25 x 2
  longueur = 258.5
FEATURE [App::Link] A14002  label="A14003"
  AssemblyType = Asm4EE
  AttachedBy = #B1002
  AttachedTo = A5001#cote2003
  AttachmentOffset = pos=(8.295,0,-11.77) rot=(0.499145,-0.499145,-0.708314;1.90902rad)
  LinkPlacement = pos=(996.705,-222.5,-284.23) rot=(-0.170689,0,-0.985325;3.14159rad)
  LinkedObject = -> Part004
  Placement = pos=(996.705,-222.5,-284.23) rot=(-0.170689,0,-0.985325;3.14159rad)
  expr: .AttachmentOffset.Rotation.Roll = Sketch014.Constraints.anglerou
  expr: Placement = A5001.Placement * cote2003.Placement * AttachmentOffset * B1002.Placement ^ -1
FEATURE [App::Link] A14003  label="A14004"
  AssemblyType = Asm4EE
  AttachedBy = #B1002
  AttachedTo = A5002#cote2003
  AttachmentOffset = pos=(0,8.29,-11.77) rot=(1,0,0;1.22774rad)
  LinkPlacement = pos=(1013.29,222.5,-284.23) rot=(0,-1,0;0.343057rad)
  LinkedObject = -> Part004
  Placement = pos=(1013.29,222.5,-284.23) rot=(0,-1,0;0.343057rad)
  expr: .AttachmentOffset.Rotation.Roll = Sketch014.Constraints.anglerou
  expr: Placement = A5002.Placement * cote2003.Placement * AttachmentOffset * B1002.Placement ^ -1
FEATURE [App::Link] A14004  label="A14005"
  AssemblyType = Asm4EE
  AttachedBy = #B2002
  AttachedTo = A5002#cote2003
  AttachmentOffset = pos=(0,-8.3,-11.77) rot=(0,0.576035,0.817425;3.14159rad)
  LinkPlacement = pos=(268.897,222.5,-24.2733) rot=(-0.985325,0,0.170689;3.14159rad)
  LinkedObject = -> Part004
  Placement = pos=(268.897,222.5,-24.2733) rot=(-0.985325,0,0.170689;3.14159rad)
  expr: .AttachmentOffset.Rotation.Roll = Sketch014.Constraints.anglerou
  expr: Placement = A5002.Placement * cote2003.Placement * AttachmentOffset * B2002.Placement ^ -1
FEATURE [PartDesign::CoordinateSystem] dessus
  AttacherType = Attacher::AttachEngine3D
  AttachmentOffset = pos=(0,-10.5,0) rot=(0,0,1;0rad)
  AttachmentSupport = -> [Pad009]
  MapMode = 45
  Placement = pos=(-3e-16,-33.5,1.01e-14) rot=(0,1,0;3.14159rad)
FEATURE [PartDesign::CoordinateSystem] dessous
  AttacherType = Attacher::AttachEngine3D
  AttachmentSupport = -> [Pad009]
  MapMode = 5
  Placement = pos=(0,1.8e-15,4) rot=(0,0,1;3.14159rad)
FEATURE [App::Part] Part001  label="A11"
  Group = -> [Body007,dessus,dessous]
  Nom_de_la_piece = 'A11
  Origin = -> Origin023
  Reference_AP = fer U 30 x 15 x 4
  longueur = 46
FEATURE [PartDesign::CoordinateSystem] axe
  AttacherType = Attacher::AttachEngine3D
  AttachmentOffset = pos=(0,-12.5,0) rot=(0,0,1;0rad)
  AttachmentSupport = -> [Pad008]
  MapMode = 5
  Placement = pos=(0,-2.8e-15,12.5) rot=(0,0.707107,-0.707107;3.14159rad)
FEATURE [App::Link] A11  label="A14006"
  AssemblyType = Asm4EE
  AttachedBy = #dessus
  AttachedTo = A5002#cote2003
  AttachmentOffset = pos=(0,0,0) rot=(0.707107,-0.707107,0;3.14159rad)
  LinkPlacement = pos=(1005,189,-296) rot=(1,0,0;3.14159rad)
  LinkedObject = -> Part001
  Placement = pos=(1005,189,-296) rot=(1,0,0;3.14159rad)
  expr: Placement = A5002.Placement * cote2003.Placement * AttachmentOffset * dessus.Placement ^ -1
FEATURE [App::Link] A11001
  AssemblyType = Asm4EE
  AttachedBy = #dessus
  AttachedTo = A5001#cote2003
  AttachmentOffset = pos=(0,0,0) rot=(0,-1,0;3.14159rad)
  LinkPlacement = pos=(1005,-189,-296) rot=(0,-1,0;3.14159rad)
  LinkedObject = -> Part001
  Placement = pos=(1005,-189,-296) rot=(0,-1,0;3.14159rad)
  expr: Placement = A5001.Placement * cote2003.Placement * AttachmentOffset * dessus.Placement ^ -1
FEATURE [App::Link] A10  label="A14007"
  AssemblyType = Asm4EE
  AttachedBy = #axe
  AttachedTo = A11001#dessous
  AttachmentOffset = pos=(0,5,0) rot=(0,0.707107,0.707107;3.14159rad)
  LinkPlacement = pos=(1005,-194,-312.5) rot=(0,0,1;0rad)
  LinkedObject = -> Part
  Placement = pos=(1005,-194,-312.5) rot=(0,0,1;0rad)
  expr: Placement = A11001.Placement * dessous.Placement * AttachmentOffset * axe.Placement ^ -1
FEATURE [App::Link] A10006
  AssemblyType = Asm4EE
  AttachedBy = #axe
  AttachedTo = A11#dessous
  AttachmentOffset = pos=(0,5,0) rot=(0,0.707107,0.707107;3.14159rad)
  LinkPlacement = pos=(1005,194,-312.5) rot=(0,0,1;3.14159rad)
  LinkedObject = -> Part
  Placement = pos=(1005,194,-312.5) rot=(0,0,1;3.14159rad)
  expr: Placement = A11.Placement * dessous.Placement * AttachmentOffset * axe.Placement ^ -1
FEATURE [App::Link] Roue_increvable___389___axe25_L_82001
  AssemblyType = Asm4EE
  AttachedBy = #LCS_0004
  AttachedTo = A10006#axe
  AttachmentOffset = pos=(0,0,-6) rot=(0,1,0;1.5708rad)
  LinkPlacement = pos=(1005,288,-312.5) rot=(-0.57735,0.57735,-0.57735;2.0944rad)
  LinkedObject = -> Roue_increvable___389___axe25_L_82
  Placement = pos=(1005,288,-312.5) rot=(-0.57735,0.57735,-0.57735;2.0944rad)
  expr: Placement = A10006.Placement * axe.Placement * AttachmentOffset * LCS_0004.Placement ^ -1
FEATURE [App::Link] Roue_increvable___389___axe25_L_82002
  AssemblyType = Asm4EE
  AttachedBy = #LCS_0004
  AttachedTo = A10#axe
  AttachmentOffset = pos=(0,0,-6) rot=(0,-1,0;4.71239rad)
  LinkPlacement = pos=(1005,-288,-312.5) rot=(-0.57735,-0.57735,0.57735;2.0944rad)
  LinkedObject = -> Roue_increvable___389___axe25_L_82
  Placement = pos=(1005,-288,-312.5) rot=(-0.57735,-0.57735,0.57735;2.0944rad)
  expr: Placement = A10.Placement * axe.Placement * AttachmentOffset * LCS_0004.Placement ^ -1
FEATURE [Sketcher::SketchObject] Sketch018
  ArcFitTolerance = 0
  FullyConstrained = true
  MakeInternals = false
  MapMode = 5
  Placement = pos=(0,0,0) rot=(0.57735,0.57735,0.57735;2.0944rad)
  expr: Constraints[15] = .Constraints.hauteur * 0.1
  expr: Constraints[27] = .Constraints.epaisseur
  sketch-geometry (12):
    g0: LineSegment StartX=-10 StartY=12.5 StartZ=0 EndX=10 EndY=12.5 EndZ=0
    g1: LineSegment StartX=12.5 StartY=10 StartZ=0 EndX=12.5 EndY=-10 EndZ=0
    g2: LineSegment StartX=10 StartY=-12.5 StartZ=0 EndX=-10 EndY=-12.5 EndZ=0
    g3: LineSegment StartX=-12.5 StartY=-10 StartZ=0 EndX=-12.5 EndY=10 EndZ=0
    g4: ArcOfCircle CenterX=-10 CenterY=10 CenterZ=0 NormalX=0 NormalY=0 NormalZ=1 AngleXU=0 Radius=2.5 StartAngle=1.5708 EndAngle=3.14159
    g5: ArcOfCircle CenterX=10 CenterY=10 CenterZ=0 NormalX=0 NormalY=0 NormalZ=1 AngleXU=0 Radius=2.5 StartAngle=2e-16 EndAngle=1.5708
    g6: ArcOfCircle CenterX=10 CenterY=-10 CenterZ=0 NormalX=0 NormalY=0 NormalZ=1 AngleXU=0 Radius=2.5 StartAngle=4.71239 EndAngle=6.28319
    g7: ArcOfCircle CenterX=-10 CenterY=-10 CenterZ=0 NormalX=0 NormalY=0 NormalZ=1 AngleXU=0 Radius=2.5 StartAngle=3.14159 EndAngle=4.71239
    g8: LineSegment StartX=-10.5 StartY=10.5 StartZ=0 EndX=10.5 EndY=10.5 EndZ=0
    g9: LineSegment StartX=10.5 StartY=10.5 StartZ=0 EndX=10.5 EndY=-10.5 EndZ=0
    g10: LineSegment StartX=10.5 StartY=-10.5 StartZ=0 EndX=-10.5 EndY=-10.5 EndZ=0
    g11: LineSegment StartX=-10.5 StartY=-10.5 StartZ=0 EndX=-10.5 EndY=10.5 EndZ=0
  constraints (28):
    c: Horizontal(g2)
    c: Vertical(g3)
    c: Tangent(g0,g4) = 1.5708
    c: Tangent(g3,g4) = 1.5708
    c: Tangent(g0,g5) = 1.5708
    c: Tangent(g1,g5) = 1.5708
    c: Tangent(g1,g6) = 1.5708
    c: Tangent(g2,g6) = 1.5708
    c: Tangent(g2,g7) = 1.5708
    c: Tangent(g3,g7) = 1.5708
    c: Equal(g4,g5)
    c: DistanceY(g2,g0) = 25  'hauteur'
    c: DistanceX(g3,g1) = 25  'largeur'
    c: Equal(g5,g6)
    c: Equal(g6,g7)
    c: Radius(g7) = 2.5
    c: Symmetric(g1,g1,g-1)
    c: Symmetric(g0,g0,g-2)
    c: Coincident(g8,g9)
    c: Coincident(g9,g10)
    c: Coincident(g10,g11)
    c: Coincident(g11,g8)
    c: Horizontal(g10)
    c: Vertical(g11)
    c: Symmetric(g8,g9,g-1)
    c: Symmetric(g8,g8,g-2)
    c: DistanceX(g3,g8) = 2  'epaisseur'
    c: DistanceY(g2,g9) = 2
FEATURE [PartDesign::Pad] Pad013
  Direction = (1,1e-16,-1e-16)
  Length = 462
  Length2 = 100
  Placement = pos=(0,0,0) rot=(0.57735,0.57735,0.57735;2.0944rad)
  Profile = -> Sketch018
  Suppressed = false
  Type = 0
  expr: Length = Sketch014.Constraints.l2pied
FEATURE [PartDesign::CoordinateSystem] cote1  label="cote2004"
  AttacherType = Attacher::AttachEngine3D
  AttachmentSupport = -> [Pad013]
  MapMode = 5
  Placement = pos=(0,0,0) rot=(0.57735,0.57735,-0.57735;4.18879rad)
FEATURE [App::Link] A15  label="A14008"
  AssemblyType = Asm4EE
  AttachedBy = #cote1
  AttachedTo = A12001#B2
  AttachmentOffset = pos=(1.67796,0,-6.25567) rot=(0,-1,0;0.524048rad)
  LinkPlacement = pos=(12.5,290.822,-406.244) rot=(-0.694725,0.186318,-0.694725;2.77318rad)
  LinkedObject = -> Part005
  Placement = pos=(12.5,290.822,-406.244) rot=(-0.694725,0.186318,-0.694725;2.77318rad)
  expr: .AttachmentOffset.Rotation.Pitch = -Sketch014.Constraints.angle2
  expr: Placement = A12001.Placement * B2.Placement * AttachmentOffset * cote1.Placement ^ -1
FEATURE [App::Link] A14008  label="A14009"
  AssemblyType = Asm4EE
  AttachedBy = #cote1
  AttachedTo = A12#B2
  AttachmentOffset = pos=(-1.68,0,-6.25) rot=(0.259036,0,0.965868;3.14159rad)
  LinkPlacement = pos=(12.5,-290.82,-406.25) rot=(-0.250759,-0.935008,0.250759;1.63795rad)
  LinkedObject = -> Part005
  Placement = pos=(12.5,-290.82,-406.25) rot=(-0.250759,-0.935008,0.250759;1.63795rad)
  expr: .AttachmentOffset.Rotation.Pitch = -Sketch014.Constraints.angle2
  expr: Placement = A12.Placement * B2.Placement * AttachmentOffset * cote1.Placement ^ -1
FEATURE [App::Link] A15001
  AssemblyType = Asm4EE
  AttachedBy = #cote1
  AttachedTo = A12002#B2
  AttachmentOffset = pos=(0,1.68,-6.25) rot=(0.250759,-0.250759,0.935008;1.63795rad)
  LinkPlacement = pos=(1997.5,-290.82,-406.25) rot=(0.250759,0.935008,-0.250759;4.64524rad)
  LinkedObject = -> Part005
  Placement = pos=(1997.5,-290.82,-406.25) rot=(0.250759,0.935008,-0.250759;4.64524rad)
  expr: .AttachmentOffset.Rotation.Pitch = -Sketch014.Constraints.angle2
  expr: Placement = A12002.Placement * B2.Placement * AttachmentOffset * cote1.Placement ^ -1
FEATURE [App::Link] A15002
  AssemblyType = Asm4EE
  AttachedBy = #cote1
  AttachedTo = A12003#B2
  AttachmentOffset = pos=(0,-1.68,-6.25) rot=(-0.250759,-0.250759,-0.935008;1.63795rad)
  LinkPlacement = pos=(1997.5,290.82,-406.25) rot=(-0.694725,0.186318,-0.694725;2.77318rad)
  LinkedObject = -> Part005
  Placement = pos=(1997.5,290.82,-406.25) rot=(-0.694725,0.186318,-0.694725;2.77318rad)
  expr: .AttachmentOffset.Rotation.Pitch = -Sketch014.Constraints.angle2
  expr: Placement = A12003.Placement * B2.Placement * AttachmentOffset * cote1.Placement ^ -1
FEATURE [Sketcher::SketchObject] Sketch019
  ArcFitTolerance = 0
  FullyConstrained = true
  MakeInternals = false
  MapMode = 5
  Placement = pos=(0,0,0) rot=(0.57735,0.57735,0.57735;2.0944rad)
  expr: Constraints[15] = .Constraints.hauteur * 0.1
  expr: Constraints[27] = .Constraints.epaisseur
  sketch-geometry (12):
    g0: LineSegment StartX=-10 StartY=12.5 StartZ=0 EndX=10 EndY=12.5 EndZ=0
    g1: LineSegment StartX=12.5 StartY=10 StartZ=0 EndX=12.5 EndY=-10 EndZ=0
    g2: LineSegment StartX=10 StartY=-12.5 StartZ=0 EndX=-10 EndY=-12.5 EndZ=0
    g3: LineSegment StartX=-12.5 StartY=-10 StartZ=0 EndX=-12.5 EndY=10 EndZ=0
    g4: ArcOfCircle CenterX=-10 CenterY=10 CenterZ=0 NormalX=0 NormalY=0 NormalZ=1 AngleXU=0 Radius=2.5 StartAngle=1.5708 EndAngle=3.14159
    g5: ArcOfCircle CenterX=10 CenterY=10 CenterZ=0 NormalX=0 NormalY=0 NormalZ=1 AngleXU=0 Radius=2.5 StartAngle=2e-16 EndAngle=1.5708
    g6: ArcOfCircle CenterX=10 CenterY=-10 CenterZ=0 NormalX=0 NormalY=0 NormalZ=1 AngleXU=0 Radius=2.5 StartAngle=4.71239 EndAngle=6.28319
    g7: ArcOfCircle CenterX=-10 CenterY=-10 CenterZ=0 NormalX=0 NormalY=0 NormalZ=1 AngleXU=0 Radius=2.5 StartAngle=3.14159 EndAngle=4.71239
    g8: LineSegment StartX=-10.5 StartY=10.5 StartZ=0 EndX=10.5 EndY=10.5 EndZ=0
    g9: LineSegment StartX=10.5 StartY=10.5 StartZ=0 EndX=10.5 EndY=-10.5 EndZ=0
    g10: LineSegment StartX=10.5 StartY=-10.5 StartZ=0 EndX=-10.5 EndY=-10.5 EndZ=0
    g11: LineSegment StartX=-10.5 StartY=-10.5 StartZ=0 EndX=-10.5 EndY=10.5 EndZ=0
  constraints (28):
    c: Horizontal(g2)
    c: Vertical(g3)
    c: Tangent(g0,g4) = 1.5708
    c: Tangent(g3,g4) = 1.5708
    c: Tangent(g0,g5) = 1.5708
    c: Tangent(g1,g5) = 1.5708
    c: Tangent(g1,g6) = 1.5708
    c: Tangent(g2,g6) = 1.5708
    c: Tangent(g2,g7) = 1.5708
    c: Tangent(g3,g7) = 1.5708
    c: Equal(g4,g5)
    c: DistanceY(g2,g0) = 25  'hauteur'
    c: DistanceX(g3,g1) = 25  'largeur'
    c: Equal(g5,g6)
    c: Equal(g6,g7)
    c: Radius(g7) = 2.5
    c: Symmetric(g1,g1,g-1)
    c: Symmetric(g0,g0,g-2)
    c: Coincident(g8,g9)
    c: Coincident(g9,g10)
    c: Coincident(g10,g11)
    c: Coincident(g11,g8)
    c: Horizontal(g10)
    c: Vertical(g11)
    c: Symmetric(g8,g9,g-1)
    c: Symmetric(g8,g8,g-2)
    c: DistanceX(g3,g8) = 2  'epaisseur'
    c: DistanceY(g2,g9) = 2
FEATURE [PartDesign::Pad] Pad014
  Direction = (1,1e-16,-1e-16)
  Length = 685
  Length2 = 100
  Placement = pos=(0,0,0) rot=(0.57735,0.57735,0.57735;2.0944rad)
  Profile = -> Sketch019
  Suppressed = false
  Type = 0
  expr: Length = Spreadsheet.B12 + Spreadsheet.B2 * 3
FEATURE [PartDesign::Body] Body012
  AllowCompound = false
  Group = -> [Sketch019,Pad014]
  Origin = -> Origin034
  Tip = -> Pad014
FEATURE [Sketcher::SketchObject] Sketch020
  ArcFitTolerance = 0
  FullyConstrained = true
  MakeInternals = false
  MapMode = 5
  Placement = pos=(0,0,0) rot=(0.57735,0.57735,0.57735;2.0944rad)
  expr: Constraints[15] = .Constraints.hauteur * 0.1
  expr: Constraints[27] = .Constraints.epaisseur
  sketch-geometry (12):
    g0: LineSegment StartX=-10 StartY=12.5 StartZ=0 EndX=10 EndY=12.5 EndZ=0
    g1: LineSegment StartX=12.5 StartY=10 StartZ=0 EndX=12.5 EndY=-10 EndZ=0
    g2: LineSegment StartX=10 StartY=-12.5 StartZ=0 EndX=-10 EndY=-12.5 EndZ=0
    g3: LineSegment StartX=-12.5 StartY=-10 StartZ=0 EndX=-12.5 EndY=10 EndZ=0
    g4: ArcOfCircle CenterX=-10 CenterY=10 CenterZ=0 NormalX=0 NormalY=0 NormalZ=1 AngleXU=0 Radius=2.5 StartAngle=1.5708 EndAngle=3.14159
    g5: ArcOfCircle CenterX=10 CenterY=10 CenterZ=0 NormalX=0 NormalY=0 NormalZ=1 AngleXU=0 Radius=2.5 StartAngle=2e-16 EndAngle=1.5708
    g6: ArcOfCircle CenterX=10 CenterY=-10 CenterZ=0 NormalX=0 NormalY=0 NormalZ=1 AngleXU=0 Radius=2.5 StartAngle=4.71239 EndAngle=6.28319
    g7: ArcOfCircle CenterX=-10 CenterY=-10 CenterZ=0 NormalX=0 NormalY=0 NormalZ=1 AngleXU=0 Radius=2.5 StartAngle=3.14159 EndAngle=4.71239
    g8: LineSegment StartX=-10.5 StartY=10.5 StartZ=0 EndX=10.5 EndY=10.5 EndZ=0
    g9: LineSegment StartX=10.5 StartY=10.5 StartZ=0 EndX=10.5 EndY=-10.5 EndZ=0
    g10: LineSegment StartX=10.5 StartY=-10.5 StartZ=0 EndX=-10.5 EndY=-10.5 EndZ=0
    g11: LineSegment StartX=-10.5 StartY=-10.5 StartZ=0 EndX=-10.5 EndY=10.5 EndZ=0
  constraints (28):
    c: Horizontal(g2)
    c: Vertical(g3)
    c: Tangent(g0,g4) = 1.5708
    c: Tangent(g3,g4) = 1.5708
    c: Tangent(g0,g5) = 1.5708
    c: Tangent(g1,g5) = 1.5708
    c: Tangent(g1,g6) = 1.5708
    c: Tangent(g2,g6) = 1.5708
    c: Tangent(g2,g7) = 1.5708
    c: Tangent(g3,g7) = 1.5708
    c: Equal(g4,g5)
    c: DistanceY(g2,g0) = 25  'hauteur'
    c: DistanceX(g3,g1) = 25  'largeur'
    c: Equal(g5,g6)
    c: Equal(g6,g7)
    c: Radius(g7) = 2.5
    c: Symmetric(g1,g1,g-1)
    c: Symmetric(g0,g0,g-2)
    c: Coincident(g8,g9)
    c: Coincident(g9,g10)
    c: Coincident(g10,g11)
    c: Coincident(g11,g8)
    c: Horizontal(g10)
    c: Vertical(g11)
    c: Symmetric(g8,g9,g-1)
    c: Symmetric(g8,g8,g-2)
    c: DistanceX(g3,g8) = 2  'epaisseur'
    c: DistanceY(g2,g9) = 2
FEATURE [PartDesign::Pad] Pad015
  Direction = (1,1e-16,-1e-16)
  Length = 560
  Length2 = 100
  Placement = pos=(0,0,0) rot=(0.57735,0.57735,0.57735;2.0944rad)
  Profile = -> Sketch020
  Suppressed = false
  Type = 0
  expr: Length = Spreadsheet.B12 - Spreadsheet.B2 * 2
FEATURE [PartDesign::Body] Body013
  AllowCompound = false
  Group = -> [Sketch020,Pad015]
  Origin = -> Origin036
  Tip = -> Pad015
FEATURE [Sketcher::SketchObject] Sketch021
  ArcFitTolerance = 0
  FullyConstrained = true
  MakeInternals = false
  MapMode = 5
  Placement = pos=(0,0,0) rot=(0.57735,0.57735,0.57735;2.0944rad)
  expr: Constraints[15] = .Constraints.hauteur * 0.1
  expr: Constraints[27] = .Constraints.epaisseur
  sketch-geometry (12):
    g0: LineSegment StartX=-10 StartY=12.5 StartZ=0 EndX=10 EndY=12.5 EndZ=0
    g1: LineSegment StartX=12.5 StartY=10 StartZ=0 EndX=12.5 EndY=-10 EndZ=0
    g2: LineSegment StartX=10 StartY=-12.5 StartZ=0 EndX=-10 EndY=-12.5 EndZ=0
    g3: LineSegment StartX=-12.5 StartY=-10 StartZ=0 EndX=-12.5 EndY=10 EndZ=0
    g4: ArcOfCircle CenterX=-10 CenterY=10 CenterZ=0 NormalX=0 NormalY=0 NormalZ=1 AngleXU=0 Radius=2.5 StartAngle=1.5708 EndAngle=3.14159
    g5: ArcOfCircle CenterX=10 CenterY=10 CenterZ=0 NormalX=0 NormalY=0 NormalZ=1 AngleXU=0 Radius=2.5 StartAngle=2e-16 EndAngle=1.5708
    g6: ArcOfCircle CenterX=10 CenterY=-10 CenterZ=0 NormalX=0 NormalY=0 NormalZ=1 AngleXU=0 Radius=2.5 StartAngle=4.71239 EndAngle=6.28319
    g7: ArcOfCircle CenterX=-10 CenterY=-10 CenterZ=0 NormalX=0 NormalY=0 NormalZ=1 AngleXU=0 Radius=2.5 StartAngle=3.14159 EndAngle=4.71239
    g8: LineSegment StartX=-10.5 StartY=10.5 StartZ=0 EndX=10.5 EndY=10.5 EndZ=0
    g9: LineSegment StartX=10.5 StartY=10.5 StartZ=0 EndX=10.5 EndY=-10.5 EndZ=0
    g10: LineSegment StartX=10.5 StartY=-10.5 StartZ=0 EndX=-10.5 EndY=-10.5 EndZ=0
    g11: LineSegment StartX=-10.5 StartY=-10.5 StartZ=0 EndX=-10.5 EndY=10.5 EndZ=0
  constraints (28):
    c: Horizontal(g2)
    c: Vertical(g3)
    c: Tangent(g0,g4) = 1.5708
    c: Tangent(g3,g4) = 1.5708
    c: Tangent(g0,g5) = 1.5708
    c: Tangent(g1,g5) = 1.5708
    c: Tangent(g1,g6) = 1.5708
    c: Tangent(g2,g6) = 1.5708
    c: Tangent(g2,g7) = 1.5708
    c: Tangent(g3,g7) = 1.5708
    c: Equal(g4,g5)
    c: DistanceY(g2,g0) = 25  'hauteur'
    c: DistanceX(g3,g1) = 25  'largeur'
    c: Equal(g5,g6)
    c: Equal(g6,g7)
    c: Radius(g7) = 2.5
    c: Symmetric(g1,g1,g-1)
    c: Symmetric(g0,g0,g-2)
    c: Coincident(g8,g9)
    c: Coincident(g9,g10)
    c: Coincident(g10,g11)
    c: Coincident(g11,g8)
    c: Horizontal(g10)
    c: Vertical(g11)
    c: Symmetric(g8,g9,g-1)
    c: Symmetric(g8,g8,g-2)
    c: DistanceX(g3,g8) = 2  'epaisseur'
    c: DistanceY(g2,g9) = 2
FEATURE [PartDesign::Pad] Pad016
  Direction = (1,1e-16,-1e-16)
  Length = 610
  Length2 = 100
  Placement = pos=(0,0,0) rot=(0.57735,0.57735,0.57735;2.0944rad)
  Profile = -> Sketch021
  Suppressed = false
  Type = 0
  expr: Length = Spreadsheet.D4
FEATURE [PartDesign::Body] Body014
  AllowCompound = false
  Group = -> [Sketch021,Pad016]
  Origin = -> Origin038
  Tip = -> Pad016
FEATURE [Sketcher::SketchObject] Sketch022
  ArcFitTolerance = 0
  FullyConstrained = true
  MakeInternals = false
  MapMode = 5
  Placement = pos=(0,0,0) rot=(0.57735,0.57735,0.57735;2.0944rad)
  expr: Constraints[15] = .Constraints.hauteur * 0.1
  expr: Constraints[27] = .Constraints.epaisseur
  sketch-geometry (12):
    g0: LineSegment StartX=-12 StartY=15 StartZ=0 EndX=12 EndY=15 EndZ=0
    g1: LineSegment StartX=15 StartY=12 StartZ=0 EndX=15 EndY=-12 EndZ=0
    g2: LineSegment StartX=12 StartY=-15 StartZ=0 EndX=-12 EndY=-15 EndZ=0
    g3: LineSegment StartX=-15 StartY=-12 StartZ=0 EndX=-15 EndY=12 EndZ=0
    g4: ArcOfCircle CenterX=-12 CenterY=12 CenterZ=0 NormalX=0 NormalY=0 NormalZ=1 AngleXU=0 Radius=3 StartAngle=1.5708 EndAngle=3.14159
    g5: ArcOfCircle CenterX=12 CenterY=12 CenterZ=0 NormalX=0 NormalY=0 NormalZ=1 AngleXU=0 Radius=3 StartAngle=1e-16 EndAngle=1.5708
    g6: ArcOfCircle CenterX=12 CenterY=-12 CenterZ=0 NormalX=0 NormalY=0 NormalZ=1 AngleXU=0 Radius=3 StartAngle=4.71239 EndAngle=6.28319
    g7: ArcOfCircle CenterX=-12 CenterY=-12 CenterZ=0 NormalX=0 NormalY=0 NormalZ=1 AngleXU=0 Radius=3 StartAngle=3.14159 EndAngle=4.71239
    g8: LineSegment StartX=-13 StartY=13 StartZ=0 EndX=13 EndY=13 EndZ=0
    g9: LineSegment StartX=13 StartY=13 StartZ=0 EndX=13 EndY=-13 EndZ=0
    g10: LineSegment StartX=13 StartY=-13 StartZ=0 EndX=-13 EndY=-13 EndZ=0
    g11: LineSegment StartX=-13 StartY=-13 StartZ=0 EndX=-13 EndY=13 EndZ=0
  constraints (28):
    c: Horizontal(g2)
    c: Vertical(g3)
    c: Tangent(g0,g4) = 1.5708
    c: Tangent(g3,g4) = 1.5708
    c: Tangent(g0,g5) = 1.5708
    c: Tangent(g1,g5) = 1.5708
    c: Tangent(g1,g6) = 1.5708
    c: Tangent(g2,g6) = 1.5708
    c: Tangent(g2,g7) = 1.5708
    c: Tangent(g3,g7) = 1.5708
    c: Equal(g4,g5)
    c: DistanceY(g2,g0) = 30  'hauteur'
    c: DistanceX(g3,g1) = 30  'largeur'
    c: Equal(g5,g6)
    c: Equal(g6,g7)
    c: Radius(g7) = 3
    c: Symmetric(g1,g1,g-1)
    c: Symmetric(g0,g0,g-2)
    c: Coincident(g8,g9)
    c: Coincident(g9,g10)
    c: Coincident(g10,g11)
    c: Coincident(g11,g8)
    c: Horizontal(g10)
    c: Vertical(g11)
    c: Symmetric(g8,g9,g-1)
    c: Symmetric(g8,g8,g-2)
    c: DistanceX(g3,g8) = 2  'epaisseur'
    c: DistanceY(g2,g9) = 2
FEATURE [PartDesign::Pad] Pad017
  Direction = (1,1e-16,-1e-16)
  Length = 50
  Length2 = 100
  Placement = pos=(0,0,0) rot=(0.57735,0.57735,0.57735;2.0944rad)
  Profile = -> Sketch022
  Suppressed = false
  Type = 0
  expr: Length = 2 * Spreadsheet.B2
FEATURE [PartDesign::Body] Body015
  AllowCompound = false
  Group = -> [Sketch022,Pad017]
  Origin = -> Origin040
  Tip = -> Pad017
FEATURE [PartDesign::CoordinateSystem] face1
  AttacherType = Attacher::AttachEngine3D
  AttachmentSupport = -> [Pad017]
  MapMode = 5
  Placement = pos=(-1.7e-15,15,-9e-16) rot=(0.57735,0.57735,0.57735;4.18879rad)
FEATURE [PartDesign::CoordinateSystem] cote2004  label="cote2005"
  AttacherType = Attacher::AttachEngine3D
  AttachmentSupport = -> [Pad015]
  MapMode = 5
  Placement = pos=(560,2.464e-13,0) rot=(0.57735,0.57735,0.57735;2.0944rad)
FEATURE [PartDesign::CoordinateSystem] cote1001
  AttacherType = Attacher::AttachEngine3D
  AttachmentSupport = -> [Pad015]
  MapMode = 5
  Placement = pos=(0,0,0) rot=(0.57735,0.57735,-0.57735;4.18879rad)
FEATURE [App::Part] Part007  label="BB2"
  Group = -> [Body013,cote2004,cote1001]
  Nom_de_la_piece = 'BB2
  Origin = -> Origin035
  Reference_AP = Tube carré 25 x 2
  longueur = 560
FEATURE [PartDesign::CoordinateSystem] cote1002
  AttacherType = Attacher::AttachEngine3D
  AttachmentSupport = -> [Pad014]
  MapMode = 5
  Placement = pos=(0,0,0) rot=(0.57735,0.57735,-0.57735;4.18879rad)
FEATURE [PartDesign::CoordinateSystem] cote2005  label="cote2006"
  AttacherType = Attacher::AttachEngine3D
  AttachmentSupport = -> [Pad014]
  MapMode = 5
  Placement = pos=(685,3.014e-13,0) rot=(0.57735,0.57735,0.57735;2.0944rad)
FEATURE [App::Part] Part006  label="BB1"
  Group = -> [Body012,cote1002,cote2005]
  Nom_de_la_piece = 'BB1
  Origin = -> Origin033
  Reference_AP = Tube carré 25 x 2
  longueur = 685
FEATURE [PartDesign::CoordinateSystem] cote1003
  AttacherType = Attacher::AttachEngine3D
  AttachmentSupport = -> [Pad016]
  MapMode = 5
  Placement = pos=(610,2.684e-13,0) rot=(0.57735,0.57735,0.57735;2.0944rad)
FEATURE [PartDesign::CoordinateSystem] cote2006  label="cote2007"
  AttacherType = Attacher::AttachEngine3D
  AttachmentSupport = -> [Pad016]
  MapMode = 5
  Placement = pos=(0,0,0) rot=(0.57735,0.57735,-0.57735;4.18879rad)
FEATURE [App::Part] Part008  label="BB3"
  Group = -> [Body014,cote1003,cote2006]
  Nom_de_la_piece = 'BB3
  Origin = -> Origin037
  Reference_AP = Tube carré 25 x 2
  longueur = 610
FEATURE [PartDesign::CoordinateSystem] centre
  AttacherType = Attacher::AttachEngine3D
  AttachmentSupport = -> [Pad017]
  MapMode = 5
  Placement = pos=(0,0,0) rot=(0.57735,0.57735,-0.57735;4.18879rad)
FEATURE [App::Part] Part009  label="A16"
  Group = -> [Body015,face1,centre]
  Nom_de_la_piece = 'A16
  Origin = -> Origin039
  Reference_AP = Tube carré 30 x 2
  longueur = 50
FEATURE [App::Link] A16  label="A15003"
  AssemblyType = Asm4EE
  AttachedBy = #face1
  AttachedTo = A2001#cote2A2
  AttachmentOffset = pos=(-12.5,-12.5,-12.5) rot=(0,1,0;1.5708rad)
  LinkPlacement = pos=(-15,292.5,12.5) rot=(0.57735,0.57735,-0.57735;2.0944rad)
  LinkedObject = -> Part009
  Placement = pos=(-15,292.5,12.5) rot=(0.57735,0.57735,-0.57735;2.0944rad)
  expr: .AttachmentOffset.Base.x = -Spreadsheet.B2 / 2
  expr: .AttachmentOffset.Base.y = -Spreadsheet.B2 / 2
  expr: .AttachmentOffset.Base.z = -Spreadsheet.B2 / 2
  expr: Placement = A2001.Placement * cote2A2.Placement * AttachmentOffset * face1.Placement ^ -1
FEATURE [App::Link] A16001
  AssemblyType = Asm4EE
  AttachedBy = #face1
  AttachedTo = A2001#LCS_0001
  AttachmentOffset = pos=(12.5,-12.5,-12.5) rot=(0,-0.707107,-0.707107;3.14159rad)
  LinkPlacement = pos=(-15,-292.5,12.5) rot=(-0.57735,-0.57735,0.57735;4.18879rad)
  LinkedObject = -> Part009
  Placement = pos=(-15,-292.5,12.5) rot=(-0.57735,-0.57735,0.57735;4.18879rad)
  expr: .AttachmentOffset.Base.x = Spreadsheet.B2 / 2
  expr: .AttachmentOffset.Base.y = -Spreadsheet.B2 / 2
  expr: .AttachmentOffset.Base.z = -Spreadsheet.B2 / 2
  expr: Placement = A2001.Placement * LCS_0001.Placement * AttachmentOffset * face1.Placement ^ -1
FEATURE [App::Link] BB1  label="BB004"
  AssemblyType = Asm4EE
  AttachedBy = #cote1002
  AttachedTo = A16001#centre
  AttachmentOffset = pos=(0,0,-75) rot=(0,1,0;3.14159rad)
  LinkPlacement = pos=(-15,-292.5,-62.5) rot=(-0.57735,0.57735,-0.57735;4.18879rad)
  LinkedObject = -> Part006
  Placement = pos=(-15,-292.5,-62.5) rot=(-0.57735,0.57735,-0.57735;4.18879rad)
  expr: .AttachmentOffset.Base.z = -Spreadsheet.B2 * 3
  expr: Placement = A16001.Placement * centre.Placement * AttachmentOffset * cote1002.Placement ^ -1
FEATURE [App::Link] BB1001
  AssemblyType = Asm4EE
  AttachedBy = #cote1002
  AttachedTo = A16#centre
  AttachmentOffset = pos=(0,0,-75) rot=(1,0,0;3.14159rad)
  LinkPlacement = pos=(-15,292.5,-62.5) rot=(-0.57735,-0.57735,-0.57735;2.0944rad)
  LinkedObject = -> Part006
  Placement = pos=(-15,292.5,-62.5) rot=(-0.57735,-0.57735,-0.57735;2.0944rad)
  expr: .AttachmentOffset.Base.z = -Spreadsheet.B2 * 3
  expr: Placement = A16.Placement * centre.Placement * AttachmentOffset * cote1002.Placement ^ -1
FEATURE [App::Link] BB3  label="BB1002"
  AssemblyType = Asm4EE
  AttachedBy = #cote1003
  AttachedTo = BB1001#cote2005
  AttachmentOffset = pos=(0,37.5,-12.5) rot=(-1,0,0;1.5708rad)
  LinkPlacement = pos=(-15,-280,610) rot=(-0.707107,-0.707107,0;3.14159rad)
  LinkedObject = -> Part007
  Placement = pos=(-15,-280,610) rot=(-0.707107,-0.707107,0;3.14159rad)
  expr: .AttachmentOffset.Base.y = Spreadsheet.B2 * 1.5
  expr: .AttachmentOffset.Base.z = -Spreadsheet.B2 / 2
  expr: Placement = BB1001.Placement * cote2005.Placement * AttachmentOffset * cote1003.Placement ^ -1
FEATURE [App::Link] BB2  label="BB1003"
  AssemblyType = Asm4EE
  AttachedBy = #cote1001
  AttachedTo = BB1001#cote1002
  AttachmentOffset = pos=(0,12.5,-87.5) rot=(1,0,0;1.5708rad)
  LinkPlacement = pos=(-15,280,25) rot=(0,0,1;4.71239rad)
  LinkedObject = -> Part007
  Placement = pos=(-15,280,25) rot=(0,0,1;4.71239rad)
  expr: .AttachmentOffset.Base.y = Spreadsheet.B2 / 2
  expr: .AttachmentOffset.Base.z = -Spreadsheet.B2 * 3.5
  expr: Placement = BB1001.Placement * cote1002.Placement * AttachmentOffset * cote1001.Placement ^ -1
FEATURE [App::Link] BB1003  label="BB1004"
  AssemblyType = Asm4EE
  AttachedBy = #cote2004
  AttachedTo = BB3#cote1003
  AttachmentOffset = pos=(0,12.5,-232.5) rot=(1,0,0;1.5708rad)
  LinkPlacement = pos=(-15,97.5,37.5) rot=(-0.57735,-0.57735,-0.57735;2.0944rad)
  LinkedObject = -> Part007
  Placement = pos=(-15,97.5,37.5) rot=(-0.57735,-0.57735,-0.57735;2.0944rad)
  expr: .AttachmentOffset.Base.y = Spreadsheet.B2 / 2
  expr: .AttachmentOffset.Base.z = -(Spreadsheet.D4 - Spreadsheet.B2) / 3 - Spreadsheet.B2 * 1.5
  expr: Placement = BB3.Placement * cote1003.Placement * AttachmentOffset * cote2004.Placement ^ -1
FEATURE [App::Link] BB1004  label="BB1005"
  AssemblyType = Asm4EE
  AttachedBy = #cote1001
  AttachedTo = BB3#cote2006
  AttachmentOffset = pos=(0,-12.5,-182.5) rot=(-1,0,0;1.5708rad)
  LinkPlacement = pos=(-15,-97.5,597.5) rot=(0.57735,0.57735,-0.57735;2.0944rad)
  LinkedObject = -> Part007
  Placement = pos=(-15,-97.5,597.5) rot=(0.57735,0.57735,-0.57735;2.0944rad)
  expr: .AttachmentOffset.Base.y = -Spreadsheet.B2 / 2
  expr: .AttachmentOffset.Base.z = -(Spreadsheet.D4 - Spreadsheet.B2) / 3 + Spreadsheet.B2 / 2
  expr: Placement = BB3.Placement * cote2006.Placement * AttachmentOffset * cote1001.Placement ^ -1
FEATURE [Sketcher::SketchObject] Sketch023
  ArcFitTolerance = 0
  AttachmentSupport = -> [Pad007]
  ExternalGeometry = -> [Pad007]
  FullyConstrained = true
  MakeInternals = false
  MapMode = 5
  Placement = pos=(0,-12.5,0) rot=(1,0,0;1.5708rad)
  expr: Constraints[0] = Spreadsheet.B13
  sketch-geometry (1):
    g0: Circle CenterX=0 CenterY=223.292 CenterZ=0 NormalX=0 NormalY=0 NormalZ=1 AngleXU=0 Radius=15
  constraints (4):
    c: Diameter(g0) = 30
    c: PointOnObject(g0,g-2)
    c: PointOnObject(g-4,g0)
    c: DistanceY(g-4,g0) = 8.29156  'deport'
FEATURE [PartDesign::Pocket] Pocket
  BaseFeature = -> Pad007
  Direction = (0,1,-2e-16)
  Length = 5
  Length2 = 100
  Profile = -> Sketch023
  Suppressed = false
  Type = 1
FEATURE [PartDesign::Body] A8004
  AllowCompound = false
  Group = -> [LCS_0014,Pad007,Sketch011,Sketch023,Pocket]
  Origin = -> Origin020
  Tip = -> Pocket
FEATURE [Sketcher::SketchObject] Sketch024
  ArcFitTolerance = 0
  AttachmentSupport = -> [XZ_Plane042]
  FullyConstrained = true
  MakeInternals = false
  MapMode = 5
  Placement = pos=(0,0,0) rot=(1,0,0;1.5708rad)
  expr: .Constraints.diametre = Spreadsheet.B13
  sketch-geometry (4):
    g0: Circle CenterX=0 CenterY=0 CenterZ=0 NormalX=0 NormalY=0 NormalZ=1 AngleXU=0 Radius=13
    g1: Circle CenterX=0 CenterY=0 CenterZ=0 NormalX=0 NormalY=0 NormalZ=1 AngleXU=0 Radius=15
    g2: GeomPoint [constr] X=-15 Y=0 Z=0
    g3: GeomPoint [constr] X=-13 Y=0 Z=0
  constraints (8):
    c: Coincident(g1,g0)
    c: PointOnObject(g2,g1)
    c: PointOnObject(g3,g0)
    c: Coincident(g0,g-1)
    c: PointOnObject(g3,g-1)
    c: PointOnObject(g2,g-1)
    c: DistanceX(g2,g3) = 2  'epaisseur'
    c: Diameter(g1) = 30  'diametre'
FEATURE [PartDesign::Pad] Pad018
  Direction = (0,-1,2e-16)
  Length = 300
  Length2 = 100
  Placement = pos=(0,0,0) rot=(1,0,0;1.5708rad)
  Profile = -> Sketch024
  Suppressed = false
  Type = 0
FEATURE [PartDesign::Body] Body016
  AllowCompound = false
  Group = -> [Sketch024,Pad018]
  Origin = -> Origin042
  Tip = -> Pad018
FEATURE [PartDesign::CoordinateSystem] centre001
  AttacherType = Attacher::AttachEngine3D
  AttachmentSupport = -> [Pad018]
  MapMode = 5
  Placement = pos=(0,-300,0) rot=(1,0,0;1.5708rad)
FEATURE [App::Part] Part010  label="A17"
  Group = -> [Body016,centre001]
  Nom_de_la_piece = 'A17
  Origin = -> Origin041
  Reference_AP = Tube rond 30 x 2
  longueur = 300
FEATURE [App::Link] A17  label="A16002"
  AssemblyType = Asm4EE
  AttachedBy = #centre001
  AttachedTo = A9#cote2001
  AttachmentOffset = pos=(0,0,0) rot=(1,0,0;4.71239rad)
  LinkPlacement = pos=(2585,-292.5,235.792) rot=(0.707107,0.707107,0;3.14159rad)
  LinkedObject = -> Part010
  Placement = pos=(2585,-292.5,235.792) rot=(0.707107,0.707107,0;3.14159rad)
  expr: Placement = A9.Placement * cote2001.Placement * AttachmentOffset * centre001.Placement ^ -1
FEATURE [App::Link] A17001
  AssemblyType = Asm4EE
  AttachedBy = #centre001
  AttachedTo = A9001#cote2001
  AttachmentOffset = pos=(0,0,0) rot=(1,0,0;4.71239rad)
  LinkPlacement = pos=(2585,292.5,235.792) rot=(0.707107,0.707107,0;3.14159rad)
  LinkedObject = -> Part010
  Placement = pos=(2585,292.5,235.792) rot=(0.707107,0.707107,0;3.14159rad)
  expr: Placement = A9001.Placement * cote2001.Placement * AttachmentOffset * centre001.Placement ^ -1
FEATURE [Sketcher::SketchObject] Sketch025
  ArcFitTolerance = 0
  FullyConstrained = true
  MakeInternals = false
  MapMode = 5
  Placement = pos=(0,0,0) rot=(0.57735,0.57735,0.57735;2.0944rad)
  expr: Constraints[15] = .Constraints.hauteur * 0.1
  expr: Constraints[27] = .Constraints.epaisseur
  sketch-geometry (12):
    g0: LineSegment StartX=-10 StartY=12.5 StartZ=0 EndX=10 EndY=12.5 EndZ=0
    g1: LineSegment StartX=12.5 StartY=10 StartZ=0 EndX=12.5 EndY=-10 EndZ=0
    g2: LineSegment StartX=10 StartY=-12.5 StartZ=0 EndX=-10 EndY=-12.5 EndZ=0
    g3: LineSegment StartX=-12.5 StartY=-10 StartZ=0 EndX=-12.5 EndY=10 EndZ=0
    g4: ArcOfCircle CenterX=-10 CenterY=10 CenterZ=0 NormalX=0 NormalY=0 NormalZ=1 AngleXU=0 Radius=2.5 StartAngle=1.5708 EndAngle=3.14159
    g5: ArcOfCircle CenterX=10 CenterY=10 CenterZ=0 NormalX=0 NormalY=0 NormalZ=1 AngleXU=0 Radius=2.5 StartAngle=2e-16 EndAngle=1.5708
    g6: ArcOfCircle CenterX=10 CenterY=-10 CenterZ=0 NormalX=0 NormalY=0 NormalZ=1 AngleXU=0 Radius=2.5 StartAngle=4.71239 EndAngle=6.28319
    g7: ArcOfCircle CenterX=-10 CenterY=-10 CenterZ=0 NormalX=0 NormalY=0 NormalZ=1 AngleXU=0 Radius=2.5 StartAngle=3.14159 EndAngle=4.71239
    g8: LineSegment StartX=-10.5 StartY=10.5 StartZ=0 EndX=10.5 EndY=10.5 EndZ=0
    g9: LineSegment StartX=10.5 StartY=10.5 StartZ=0 EndX=10.5 EndY=-10.5 EndZ=0
    g10: LineSegment StartX=10.5 StartY=-10.5 StartZ=0 EndX=-10.5 EndY=-10.5 EndZ=0
    g11: LineSegment StartX=-10.5 StartY=-10.5 StartZ=0 EndX=-10.5 EndY=10.5 EndZ=0
  constraints (28):
    c: Horizontal(g2)
    c: Vertical(g3)
    c: Tangent(g0,g4) = 1.5708
    c: Tangent(g3,g4) = 1.5708
    c: Tangent(g0,g5) = 1.5708
    c: Tangent(g1,g5) = 1.5708
    c: Tangent(g1,g6) = 1.5708
    c: Tangent(g2,g6) = 1.5708
    c: Tangent(g2,g7) = 1.5708
    c: Tangent(g3,g7) = 1.5708
    c: Equal(g4,g5)
    c: DistanceY(g2,g0) = 25  'hauteur'
    c: DistanceX(g3,g1) = 25  'largeur'
    c: Equal(g5,g6)
    c: Equal(g6,g7)
    c: Radius(g7) = 2.5
    c: Symmetric(g1,g1,g-1)
    c: Symmetric(g0,g0,g-2)
    c: Coincident(g8,g9)
    c: Coincident(g9,g10)
    c: Coincident(g10,g11)
    c: Coincident(g11,g8)
    c: Horizontal(g10)
    c: Vertical(g11)
    c: Symmetric(g8,g9,g-1)
    c: Symmetric(g8,g8,g-2)
    c: DistanceX(g3,g8) = 2  'epaisseur'
    c: DistanceY(g2,g9) = 2
FEATURE [PartDesign::Pad] Pad019
  Direction = (1,1e-16,-1e-16)
  Length = 142
  Length2 = 100
  Placement = pos=(0,0,0) rot=(0.57735,0.57735,0.57735;2.0944rad)
  Profile = -> Sketch025
  Suppressed = false
  Type = 0
FEATURE [PartDesign::CoordinateSystem] b1
  AttacherType = Attacher::AttachEngine3D
  AttachmentSupport = -> [Pad019]
  MapMode = 5
  Placement = pos=(1.4e-15,-12.5,-2.1e-15) rot=(0.57735,0.57735,-0.57735;2.0944rad)
FEATURE [PartDesign::CoordinateSystem] renf
  AttacherType = Attacher::AttachEngine3D
  AttachmentOffset = pos=(0,100.409,-25) rot=(0,0,1;0rad)
  AttachmentSupport = -> [Pocket]
  MapMode = 5
  Placement = pos=(0,12.5,100.409) rot=(1,0,0;1.5708rad)
  expr: .AttachmentOffset.Base.y = 142 / sqrt(2)
  expr: .AttachmentOffset.Base.z = -Spreadsheet.B2
FEATURE [App::Part] A8003  label="A9"
  Group = -> [LCS_0015,A8004,cote2001,renf]
  Nom_de_la_piece = 'A9
  Origin = -> Origin019
  Reference_AP = Tube carré 25 x 2
  longueur = 215
FEATURE [PartDesign::CoordinateSystem] renf001
  AttacherType = Attacher::AttachEngine3D
  AttachmentOffset = pos=(0,299.591,0) rot=(0,0,1;0rad)
  AttachmentSupport = -> [Pad010]
  MapMode = 5
  Placement = pos=(299.591,-12.5,-2.1e-15) rot=(0.57735,0.57735,-0.57735;2.0944rad)
  expr: .AttachmentOffset.Base.y = Pad010.Length - 142 mm / sqrt(2)
FEATURE [App::Part] Part002  label="A12"
  Group = -> [Body008,Sketch015,Pad010,B1,B2,renf001]
  Nom_de_la_piece = 'A12
  Origin = -> Origin025
  Reference_AP = Tube carré 25 x 2
  longueur = 400
FEATURE [App::Link] A18  label="A17002"
  AssemblyType = Asm4EE
  AttachedBy = #b1
  AttachedTo = A9#renf
  AttachmentOffset = pos=(0,0,0) rot=(-1,0,0;2.35619rad)
  LinkPlacement = pos=(2293.84,-292.5,104.07) rot=(-0.281085,-0.678598,0.678598;3.68962rad)
  LinkedObject = -> Part011
  Placement = pos=(2293.84,-292.5,104.07) rot=(-0.281085,-0.678598,0.678598;3.68962rad)
  expr: Placement = A9.Placement * renf.Placement * AttachmentOffset * b1.Placement ^ -1
FEATURE [App::Link] A18001
  AssemblyType = Asm4EE
  AttachedBy = #b1
  AttachedTo = A9001#renf
  AttachmentOffset = pos=(0,0,0) rot=(-1,0,0;2.35619rad)
  LinkPlacement = pos=(2293.84,292.5,104.07) rot=(-0.281085,-0.678598,0.678598;3.68962rad)
  LinkedObject = -> Part011
  Placement = pos=(2293.84,292.5,104.07) rot=(-0.281085,-0.678598,0.678598;3.68962rad)
  expr: Placement = A9001.Placement * renf.Placement * AttachmentOffset * b1.Placement ^ -1
FEATURE [App::Link] A18002
  AssemblyType = Asm4EE
  AttachedBy = #b1
  AttachedTo = A12002#renf001
  AttachmentOffset = pos=(0,0,0) rot=(1,0,0;0.785398rad)
  LinkPlacement = pos=(2001.16,-292.5,-104.07) rot=(0.862856,-0.357407,0.357407;1.71777rad)
  LinkedObject = -> Part011
  Placement = pos=(2001.16,-292.5,-104.07) rot=(0.862856,-0.357407,0.357407;1.71777rad)
  expr: Placement = A12002.Placement * renf001.Placement * AttachmentOffset * b1.Placement ^ -1
FEATURE [App::Link] A18003
  AssemblyType = Asm4EE
  AttachedBy = #b1
  AttachedTo = A12003#renf001
  AttachmentOffset = pos=(0,0,0) rot=(1,0,0;0.785398rad)
  LinkPlacement = pos=(2001.16,292.5,-104.07) rot=(0.862856,-0.357407,0.357407;1.71777rad)
  LinkedObject = -> Part011
  Placement = pos=(2001.16,292.5,-104.07) rot=(0.862856,-0.357407,0.357407;1.71777rad)
  expr: Placement = A12003.Placement * renf001.Placement * AttachmentOffset * b1.Placement ^ -1
FEATURE [Spreadsheet::Sheet] BOM
  cells = A1='Qté; B1='Nom_de_la_piece; C1='Reference_AP; D1='Angle1; E1='Angle2; F1='percage; G1='longueur; A2=4; B2='A2; C2='Tube carré 25 x 2; G2=610; A3=2; B3='A1; C3='Tube carré 25 x 2; G3=2285; A4=2; B4='A3; C4='fer rond Ø10; G4=2140; A5=2; B5='A4; C5='fer rond Ø10; G5=90; A6=2; B6='A5; C6='Tube carré 25 x 2; G6=258.5; A7=1; B7='A6; C7='Tube carré 25 x 2; G7=420; A8=2; B8='A7; C8='Tube carré 25 x 2; G8=1960; A9=1; B9='A8; C9='Tube carré 25 x 2; G9=560; A10=2; B10='A9; C10='Tube carré 25 x 2; G10=215; A11=4; B11='A12; C11='Tube carré 25 x 2; G11=400; A12=4; B12='A13; C12='Tube carré 25 x 2; D12=33.49; E12=56.51; G12=449.646319854351; A13=4; B13='A14; C13='Tube carré 25 x 2; D13=19.66; E13=19.66; G13=772.835249419013; A14=2; B14='A11; C14='UPN 30 x 15; G14=46; A15=2; B15='A10; C15='étiré rond Ø25; F15='Ø6; G15=150; A16=2; B16='roue; C16='Roue increvable Ø389 Øaxe25 L 82; A17=4; B17='A15; C17='Tube carré 25 x 2; D17=30.03; E17=59.97; G17=462; A18=2; B18='A16; C18='Tube carré 30 x 2; G18=50; A19=2; B19='BB1; C19='Tube carré 25 x 2; G19=685; A20=4; B20='BB2; C20='Tube carré 25 x 2; G20=560; A21=2; B21='A17; C21='Tube rond 30 x 2; G21=300; A22=4; B22='A18; C22='Tube carré 25 x 2; D22=45; E22=45; G22=142; A23=4; B23='rondelle int 25; C23='rondelle int 25; A24=2; B24='goupille; C24='goupille elastique 5 x 80
FEATURE [TechDraw::DrawSVGTemplate] Template  label="Modèle"
  Height = 210
  Orientation = 1
  Template = C:/Program Files/FreeCAD_0.19/data/Mod/TechDraw/Templates/A4_LandscapeTDteste.svg
  Width = 297
FEATURE [TechDraw::DrawSVGTemplate] Template001  label="Modèle001"
  Height = 210
  Orientation = 1
  Template = C:/Program Files/FreeCAD_0.19/data/Mod/TechDraw/Templates/A4_LandscapeTDteste.svg
  Width = 297
FEATURE [Sketcher::SketchObject] Sketch026
  ArcFitTolerance = 1e-06
  AttachmentSupport = -> [YZ_Plane044]
  ExternalGeometry = -> [Pad019]
  FullyConstrained = false
  MakeInternals = false
  MapMode = 5
  Placement = pos=(0,0,0) rot=(0.57735,0.57735,0.57735;2.0944rad)
  sketch-geometry (5):
    g0: LineSegment [constr] StartX=-12.5 StartY=34.6544 StartZ=0 EndX=-12.5 EndY=-40.7923 EndZ=0
    g1: LineSegment StartX=-12.5 StartY=-17.5 StartZ=0 EndX=57.5 EndY=-17.5 EndZ=0
    g2: LineSegment StartX=57.5 StartY=-17.5 StartZ=0 EndX=57.5 EndY=17.5 EndZ=0
    g3: LineSegment StartX=57.5 StartY=17.5 StartZ=0 EndX=-12.5 EndY=17.5 EndZ=0
    g4: LineSegment StartX=-12.5 StartY=17.5 StartZ=0 EndX=-12.5 EndY=-17.5 EndZ=0
  constraints (13):
    c: Coincident(g1,g2)
    c: Coincident(g2,g3)
    c: Coincident(g3,g4)
    c: Coincident(g4,g1)
    c: Horizontal(g3)
    c: Vertical(g2)
    c: Distance(g2,g4) = 70
    c: Distance(g1,g3) = 35
    c: Vertical(g0)
    c: PointOnObject(g-3,g0)
    c: Symmetric(g3,g1,g-1)
    c: PointOnObject(g3,g0)
    c: Horizontal(g1)
FEATURE [PartDesign::Plane] DatumPlane
  AttachmentSupport = -> [Pad019]
  Length = 60
  MapMode = 5
  Placement = pos=(142,6.25e-14,0) rot=(0.57735,0.57735,0.57735;2.0944rad)
  ResizeMode = 0
  Width = 60
FEATURE [Sketcher::SketchObject] Sketch027
  ArcFitTolerance = 1e-06
  AttachmentSupport = -> [DatumPlane]
  ExternalGeometry = -> [Pad019]
  FullyConstrained = false
  MakeInternals = false
  MapMode = 5
  Placement = pos=(142,6.25e-14,0) rot=(0.57735,0.57735,0.57735;2.0944rad)
  sketch-geometry (5):
    g0: LineSegment [constr] StartX=-12.5 StartY=-38.9997 StartZ=0 EndX=-12.5 EndY=36.6406 EndZ=0
    g1: LineSegment StartX=-12.5 StartY=-17.5 StartZ=0 EndX=57.5 EndY=-17.5 EndZ=0
    g2: LineSegment StartX=57.5 StartY=-17.5 StartZ=0 EndX=57.5 EndY=17.5 EndZ=0
    g3: LineSegment StartX=57.5 StartY=17.5 StartZ=0 EndX=-12.5 EndY=17.5 EndZ=0
    g4: LineSegment StartX=-12.5 StartY=17.5 StartZ=0 EndX=-12.5 EndY=-17.5 EndZ=0
  constraints (13):
    c: Coincident(g1,g2)
    c: Coincident(g2,g3)
    c: Coincident(g3,g4)
    c: Coincident(g4,g1)
    c: Horizontal(g3)
    c: Vertical(g2)
    c: Distance(g2,g4) = 70
    c: Distance(g1,g3) = 35
    c: PointOnObject(g0,g-4)
    c: Vertical(g0)
    c: Symmetric(g3,g1,g-1)
    c: Horizontal(g1)
    c: PointOnObject(g1,g0)
FEATURE [PartDesign::Groove] Groove
  Angle = 45
  Angle2 = 60
  Axis = (0,0,-75.4468)
  Base = (0,-12.5,34.6544)
  BaseFeature = -> Pad019
  Placement = pos=(0,0,0) rot=(0.57735,0.57735,0.57735;2.0944rad)
  Profile = -> Sketch026
  ReferenceAxis = -> Sketch026 [Axis]
  Suppressed = false
  Type = 0
FEATURE [PartDesign::Groove] Groove001
  Angle = 45
  Angle2 = 60
  Axis = (0,0,75.6403)
  Base = (142,-12.5,-38.9997)
  BaseFeature = -> Groove
  Placement = pos=(0,0,0) rot=(0.57735,0.57735,0.57735;2.0944rad)
  Profile = -> Sketch027
  ReferenceAxis = -> Sketch027 [Axis]
  Suppressed = false
  Type = 0
FEATURE [PartDesign::Body] Body017
  AllowCompound = false
  Group = -> [Sketch025,Pad019,Sketch026,DatumPlane,Sketch027,Groove,Groove001]
  Origin = -> Origin044
  Tip = -> Groove001
FEATURE [App::Part] Part011  label="A18"
  Group = -> [Body017,b1]
  Nom_de_la_piece = 'A18
  Origin = -> Origin043
  Placement = pos=(0,0,0) rot=(1,0,0;1.5708rad)
  Reference_AP = Tube carré 25 x 2
  longueur = 142
FEATURE [Sketcher::SketchObject] Sketch028
  ArcFitTolerance = 1e-06
  AttachmentSupport = -> [YZ_Plane029]
  ExternalGeometry = -> [Pad011]
  FullyConstrained = false
  MakeInternals = false
  MapMode = 5
  Placement = pos=(0,0,0) rot=(0.57735,0.57735,0.57735;2.0944rad)
  sketch-geometry (5):
    g0: LineSegment StartX=-17.5 StartY=12.5 StartZ=0 EndX=-17.5 EndY=-57.5 EndZ=0
    g1: LineSegment StartX=-17.5 StartY=-57.5 StartZ=0 EndX=17.5 EndY=-57.5 EndZ=0
    g2: LineSegment StartX=17.5 StartY=-57.5 StartZ=0 EndX=17.5 EndY=12.5 EndZ=0
    g3: LineSegment StartX=17.5 StartY=12.5 StartZ=0 EndX=-17.5 EndY=12.5 EndZ=0
    g4: LineSegment [constr] StartX=-59.8857 StartY=12.5 StartZ=0 EndX=133.957 EndY=12.5 EndZ=0
  constraints (13):
    c: Coincident(g0,g1)
    c: Coincident(g1,g2)
    c: Coincident(g2,g3)
    c: Coincident(g3,g0)
    c: Vertical(g0)
    c: Vertical(g2)
    c: Horizontal(g1)
    c: Horizontal(g4)
    c: PointOnObject(g2,g4)
    c: DistanceX(g1,g1) = 35
    c: DistanceY(g2,g2) = 70
    c: Symmetric(g0,g2,g-2)
    c: PointOnObject(g-3,g4)
FEATURE [PartDesign::Groove] Groove002
  Angle = 56.5107
  Angle2 = 60
  Axis = (0,193.843,0)
  Base = (0,-59.8857,12.5)
  BaseFeature = -> Pad011
  Placement = pos=(0,0,0) rot=(0.57735,0.57735,0.57735;2.0944rad)
  Profile = -> Sketch028
  ReferenceAxis = -> Sketch028 [Axis]
  Reversed = true
  Suppressed = false
  Type = 0
  expr: Angle = 90 ° - Sketch014.Constraints.angle
FEATURE [PartDesign::Plane] DatumPlane001
  AttachmentSupport = -> [Groove002]
  Length = 60
  MapMode = 5
  Placement = pos=(449.646,1.978e-13,0) rot=(0.57735,0.57735,0.57735;2.0944rad)
  ResizeMode = 0
  Width = 60
FEATURE [Sketcher::SketchObject] Sketch029
  ArcFitTolerance = 1e-06
  AttachmentSupport = -> [DatumPlane001]
  ExternalGeometry = -> [Groove002]
  FullyConstrained = false
  MakeInternals = false
  MapMode = 5
  Placement = pos=(449.646,1.978e-13,0) rot=(0.57735,0.57735,0.57735;2.0944rad)
  sketch-geometry (5):
    g0: LineSegment [constr] StartX=-50.285 StartY=12.5 StartZ=0 EndX=61.7161 EndY=12.5 EndZ=0
    g1: LineSegment StartX=-17.5 StartY=12.5 StartZ=0 EndX=-17.5 EndY=-57.5 EndZ=0
    g2: LineSegment StartX=-17.5 StartY=-57.5 StartZ=0 EndX=17.5 EndY=-57.5 EndZ=0
    g3: LineSegment StartX=17.5 StartY=-57.5 StartZ=0 EndX=17.5 EndY=12.5 EndZ=0
    g4: LineSegment StartX=17.5 StartY=12.5 StartZ=0 EndX=-17.5 EndY=12.5 EndZ=0
  constraints (13):
    c: Horizontal(g0)
    c: PointOnObject(g-3,g0)
    c: Coincident(g1,g2)
    c: Coincident(g2,g3)
    c: Coincident(g3,g4)
    c: Coincident(g4,g1)
    c: Vertical(g1)
    c: Vertical(g3)
    c: Horizontal(g2)
    c: Distance(g1,g3) = 35
    c: Distance(g2,g4) = 70
    c: PointOnObject(g1,g0)
    c: Symmetric(g3,g1,g-2)
FEATURE [App::Link] A18004
  AttachedBy = #B1001
  AttachedTo = A12#B2
  AttachmentOffset = pos=(0,-12.5,0) rot=(1,0,0;-0.584499rad)
  LinkPlacement = pos=(14.5751,-292.5,-405.603) rot=(-0.880847,0,-0.473402;3.14159rad)
  LinkedObject = -> Part003
  Placement = pos=(14.5751,-292.5,-405.603) rot=(-0.880847,0,-0.473402;3.14159rad)
  SolverId = Asm4EE
  expr: .AttachmentOffset.Rotation.Angle = -Sketch014.Constraints.angle
  expr: Placement = A12.Placement * B2.Placement * AttachmentOffset * B1001.Placement ^ -1
FEATURE [App::Link] A13  label="A18005"
  AttachedBy = #B1001
  AttachedTo = A12001#B2
  AttachmentOffset = pos=(0,-12.5,0) rot=(1,0,0;-0.584499rad)
  LinkPlacement = pos=(14.5751,292.5,-405.603) rot=(0.880847,0,0.473402;3.14159rad)
  LinkedObject = -> Part003
  Placement = pos=(14.5751,292.5,-405.603) rot=(0.880847,0,0.473402;3.14159rad)
  SolverId = Asm4EE
  expr: .AttachmentOffset.Rotation.Angle = -Sketch014.Constraints.angle
  expr: Placement = A12001.Placement * B2.Placement * AttachmentOffset * B1001.Placement ^ -1
FEATURE [App::Link] A18005  label="A18006"
  AttachedBy = #B1001
  AttachedTo = A12003#B2
  AttachmentOffset = pos=(12.5,0,0) rot=(-0.276846,-0.276846,0.92017;1.6539rad)
  LinkPlacement = pos=(1995.42,292.5,-405.603) rot=(0,1,0;4.12789rad)
  LinkedObject = -> Part003
  Placement = pos=(1995.42,292.5,-405.603) rot=(0,1,0;4.12789rad)
  SolverId = Asm4EE
  expr: .AttachmentOffset.Rotation.Roll = -Sketch014.Constraints.angle
  expr: Placement = A12003.Placement * B2.Placement * AttachmentOffset * B1001.Placement ^ -1
FEATURE [PartDesign::Groove] Groove003
  Angle = 33.4893
  Angle2 = 60
  Axis = (-1.492e-13,112.001,0)
  Base = (449.646,-50.285,12.5)
  BaseFeature = -> Groove002
  Placement = pos=(0,0,0) rot=(0.57735,0.57735,0.57735;2.0944rad)
  Profile = -> Sketch029
  ReferenceAxis = -> Sketch029 [Axis]
  Suppressed = false
  Type = 0
  expr: Angle = Sketch014.Constraints.angle
FEATURE [PartDesign::Body] Body009
  AllowCompound = false
  Group = -> [Sketch016,Pad011,Sketch028,Groove002,DatumPlane001,Sketch029,Groove003]
  Origin = -> Origin029
  Tip = -> Groove003
FEATURE [App::Part] Part003  label="A13"
  Group = -> [Body009,B1001,B2001]
  Nom_de_la_piece = 'A13
  Origin = -> Origin026
  Reference_AP = Tube carré 25 x 2
  longueur = 450
FEATURE [Sketcher::SketchObject] Sketch030
  ArcFitTolerance = 1e-06
  AttachmentSupport = -> [YZ_Plane032]
  ExternalGeometry = -> [Pad013]
  FullyConstrained = false
  MakeInternals = false
  MapMode = 5
  Placement = pos=(0,0,0) rot=(0.57735,0.57735,0.57735;2.0944rad)
  sketch-geometry (5):
    g0: LineSegment StartX=12.5 StartY=17.5 StartZ=0 EndX=-57.5 EndY=17.5 EndZ=0
    g1: LineSegment StartX=-57.5 StartY=17.5 StartZ=0 EndX=-57.5 EndY=-17.5 EndZ=0
    g2: LineSegment StartX=-57.5 StartY=-17.5 StartZ=0 EndX=12.5 EndY=-17.5 EndZ=0
    g3: LineSegment StartX=12.5 StartY=-17.5 StartZ=0 EndX=12.5 EndY=17.5 EndZ=0
    g4: LineSegment [constr] StartX=12.5 StartY=37.849 StartZ=0 EndX=12.5 EndY=-63.3268 EndZ=0
  constraints (13):
    c: Coincident(g0,g1)
    c: Coincident(g1,g2)
    c: Coincident(g2,g3)
    c: Coincident(g3,g0)
    c: Horizontal(g0)
    c: Vertical(g3)
    c: Distance(g1,g3) = 70
    c: Distance(g0,g2) = 35
    c: Horizontal(g2)
    c: Symmetric(g0,g1,g-1)
    c: Vertical(g4)
    c: PointOnObject(g-3,g4)
    c: PointOnObject(g2,g4)
FEATURE [PartDesign::Groove] Groove004
  Angle = 59.9743
  Angle2 = 60
  Axis = (0,0,-101.176)
  Base = (0,12.5,37.849)
  BaseFeature = -> Pad013
  Placement = pos=(0,0,0) rot=(0.57735,0.57735,0.57735;2.0944rad)
  Profile = -> Sketch030
  ReferenceAxis = -> Sketch030 [Axis]
  Reversed = true
  Suppressed = false
  Type = 0
  expr: Angle = 90 ° - Sketch014.Constraints.angle2
FEATURE [PartDesign::Plane] DatumPlane002
  AttachmentSupport = -> [Groove004]
  Length = 60
  MapMode = 5
  Placement = pos=(462,2.033e-13,0) rot=(0.57735,0.57735,0.57735;2.0944rad)
  ResizeMode = 0
  Width = 60
FEATURE [Sketcher::SketchObject] Sketch031
  ArcFitTolerance = 1e-06
  AttachmentSupport = -> [DatumPlane002]
  ExternalGeometry = -> [Groove004]
  FullyConstrained = false
  MakeInternals = false
  MapMode = 5
  Placement = pos=(462,2.033e-13,0) rot=(0.57735,0.57735,0.57735;2.0944rad)
  sketch-geometry (5):
    g0: LineSegment [constr] StartX=12.5 StartY=67.6644 StartZ=0 EndX=12.5 EndY=-52.0571 EndZ=0
    g1: LineSegment StartX=-57.5 StartY=17.5 StartZ=0 EndX=-57.5 EndY=-17.5 EndZ=0
    g2: LineSegment StartX=-57.5 StartY=-17.5 StartZ=0 EndX=12.5 EndY=-17.5 EndZ=0
    g3: LineSegment StartX=12.5 StartY=-17.5 StartZ=0 EndX=12.5 EndY=17.5 EndZ=0
    g4: LineSegment StartX=12.5 StartY=17.5 StartZ=0 EndX=-57.5 EndY=17.5 EndZ=0
  constraints (13):
    c: Vertical(g0)
    c: Coincident(g1,g2)
    c: Coincident(g2,g3)
    c: Coincident(g3,g4)
    c: Coincident(g4,g1)
    c: Vertical(g3)
    c: Horizontal(g2)
    c: Horizontal(g4)
    c: Distance(g1,g3) = 70
    c: Distance(g2,g4) = 35
    c: PointOnObject(g3,g-3)
    c: PointOnObject(g0,g-3)
    c: Symmetric(g1,g1,g-1)
FEATURE [PartDesign::Groove] Groove005
  Angle = 30.0257
  Angle2 = 60
  Axis = (0,0,-119.722)
  Base = (462,12.5,67.6644)
  BaseFeature = -> Groove004
  Placement = pos=(0,0,0) rot=(0.57735,0.57735,0.57735;2.0944rad)
  Profile = -> Sketch031
  ReferenceAxis = -> Sketch031 [Axis]
  Suppressed = false
  Type = 0
  expr: Angle = Sketch014.Constraints.angle2
FEATURE [PartDesign::Body] Body011
  AllowCompound = false
  Group = -> [Pad013,Sketch018,Sketch030,Groove004,DatumPlane002,Sketch031,Groove005]
  Origin = -> Origin032
  Tip = -> Groove005
FEATURE [App::Part] Part005  label="A15"
  Group = -> [Body011,cote1]
  Nom_de_la_piece = 'A15
  Origin = -> Origin031
  Reference_AP = Tube carré 25 x 2
  longueur = 462
FEATURE [Sketcher::SketchObject] Sketch032
  ArcFitTolerance = 1e-06
  AttachmentSupport = -> [YZ_Plane030]
  ExternalGeometry = -> [Pad012]
  FullyConstrained = false
  MakeInternals = false
  MapMode = 5
  Placement = pos=(0,0,0) rot=(0.57735,0.57735,0.57735;2.0944rad)
  sketch-geometry (5):
    g0: LineSegment StartX=17.5 StartY=57.5 StartZ=0 EndX=-17.5 EndY=57.5 EndZ=0
    g1: LineSegment StartX=-17.5 StartY=57.5 StartZ=0 EndX=-17.5 EndY=-12.5 EndZ=0
    g2: LineSegment StartX=-17.5 StartY=-12.5 StartZ=0 EndX=17.5 EndY=-12.5 EndZ=0
    g3: LineSegment StartX=17.5 StartY=-12.5 StartZ=0 EndX=17.5 EndY=57.5 EndZ=0
    g4: LineSegment [constr] StartX=69.7742 StartY=-12.5 StartZ=0 EndX=-82.9271 EndY=-12.5 EndZ=0
  constraints (13):
    c: Coincident(g0,g1)
    c: Coincident(g1,g2)
    c: Coincident(g2,g3)
    c: Coincident(g3,g0)
    c: Horizontal(g0)
    c: Vertical(g1)
    c: Vertical(g3)
    c: Distance(g1,g3) = 35
    c: Distance(g0,g2) = 70
    c: Symmetric(g1,g2,g-2)
    c: PointOnObject(g1,g-3)
    c: Horizontal(g4)
    c: PointOnObject(g2,g4)
FEATURE [PartDesign::Groove] Groove006
  Angle = 19.6557
  Angle2 = 60
  Axis = (0,-152.701,0)
  Base = (0,69.7742,-12.5)
  BaseFeature = -> Pad012
  Placement = pos=(0,0,0) rot=(0.57735,0.57735,0.57735;2.0944rad)
  Profile = -> Sketch032
  ReferenceAxis = -> Sketch032 [Axis]
  Reversed = true
  Suppressed = false
  Type = 0
  expr: Angle = 90 ° - Sketch014.Constraints.anglerou
FEATURE [PartDesign::Plane] DatumPlane003
  AttachmentSupport = -> [Groove006]
  Length = 60
  MapMode = 5
  Placement = pos=(772.835,3.4e-13,0) rot=(0.57735,0.57735,0.57735;2.0944rad)
  ResizeMode = 0
  Width = 60
FEATURE [Sketcher::SketchObject] Sketch033
  ArcFitTolerance = 1e-06
  AttachmentSupport = -> [DatumPlane003]
  ExternalGeometry = -> [Groove006]
  FullyConstrained = false
  MakeInternals = false
  MapMode = 5
  Placement = pos=(772.835,3.4e-13,0) rot=(0.57735,0.57735,0.57735;2.0944rad)
  sketch-geometry (5):
    g0: LineSegment [constr] StartX=-118.894 StartY=12.5 StartZ=0 EndX=112.379 EndY=12.5 EndZ=0
    g1: LineSegment StartX=-17.5 StartY=12.5 StartZ=0 EndX=-17.5 EndY=-57.5 EndZ=0
    g2: LineSegment StartX=-17.5 StartY=-57.5 StartZ=0 EndX=17.5 EndY=-57.5 EndZ=0
    g3: LineSegment StartX=17.5 StartY=-57.5 StartZ=0 EndX=17.5 EndY=12.5 EndZ=0
    g4: LineSegment StartX=17.5 StartY=12.5 StartZ=0 EndX=-17.5 EndY=12.5 EndZ=0
  constraints (13):
    c: Horizontal(g0)
    c: Coincident(g1,g2)
    c: Coincident(g2,g3)
    c: Coincident(g3,g4)
    c: Coincident(g4,g1)
    c: Vertical(g1)
    c: Vertical(g3)
    c: Horizontal(g2)
    c: Distance(g1,g3) = 35
    c: Distance(g2,g4) = 70
    c: PointOnObject(g1,g0)
    c: Symmetric(g3,g1,g-2)
    c: PointOnObject(g-3,g0)
FEATURE [PartDesign::Groove] Groove007
  Angle = 19.66
  Angle2 = 60
  Axis = (-3.081e-13,231.273,0)
  Base = (772.835,-118.894,12.5)
  BaseFeature = -> Groove006
  Placement = pos=(0,0,0) rot=(0.57735,0.57735,0.57735;2.0944rad)
  Profile = -> Sketch033
  ReferenceAxis = -> Sketch033 [Axis]
  Suppressed = false
  Type = 0
FEATURE [PartDesign::Body] Body010
  AllowCompound = false
  Group = -> [Sketch017,Pad012,Sketch032,Groove006,DatumPlane003,Sketch033,Groove007]
  Origin = -> Origin030
  Tip = -> Groove007
FEATURE [App::Part] Part004  label="A14"
  Group = -> [Body010,B1002,B2002]
  Nom_de_la_piece = 'A14
  Origin = -> Origin027
  Reference_AP = Tube carré 25 x 2
  longueur = 788
FEATURE [TechDraw::DrawProjGroupItem] View003
  CoarseView = false
  Direction = (0.57735,-0.57735,0.57735)
  Focus = 100
  HardHidden = false
  IsoCount = 0
  IsoHidden = false
  IsoVisible = false
  LockPosition = false
  Perspective = false
  Rotation = 0
  RotationVector = (1,0,0)
  Scale = 0.066667
  ScaleType = 2
  ScrubCount = 1
  SeamHidden = false
  SeamVisible = false
  SmoothHidden = false
  SmoothVisible = true
  Type = 0
  X = 117.09
  XDirection = (0.707107,0.707107,0)
  XSource = -> [Roue_increvable___389___axe25_L_82002]
  Y = 35
FEATURE [TechDraw::DrawProjGroupItem] View004
  CoarseView = false
  Direction = (0.57735,-0.57735,0.57735)
  Focus = 100
  HardHidden = false
  IsoCount = 0
  IsoHidden = false
  IsoVisible = false
  LockPosition = false
  Perspective = false
  Rotation = 0
  RotationVector = (1,0,0)
  Scale = 0.066667
  ScaleType = 2
  ScrubCount = 1
  SeamHidden = false
  SeamVisible = false
  SmoothHidden = false
  SmoothVisible = true
  Type = 0
  X = 196.962
  XDirection = (0.707107,0.707107,0)
  XSource = -> [Roue_increvable___389___axe25_L_82001]
  Y = 89.7436
FEATURE [TechDraw::DrawProjGroupItem] View005
  CoarseView = false
  Direction = (0.57735,-0.57735,0.57735)
  Focus = 100
  HardHidden = false
  IsoCount = 0
  IsoHidden = false
  IsoVisible = false
  LockPosition = false
  Perspective = false
  Rotation = 0
  RotationVector = (1,0,0)
  Scale = 0.066667
  ScaleType = 2
  ScrubCount = 1
  SeamHidden = false
  SeamVisible = false
  SmoothHidden = false
  SmoothVisible = true
  Type = 0
  X = 163.308
  XDirection = (0.707107,0.707107,0)
  XSource = -> [A2001,A1001,A1004,A3001,A3002,A4001,A4002,A2003,A5001,A5002,A6001,A7003,A7004,A8002,A9,A9001,A12,A12001,A12002,A12003,A13001,A14001,A2004,A2005,A14002,A14003,A14004,A11,A11001,A10,A10006,A15,A14008,A15001,A15002,A16,A16001,A17,A17001,A18,A18001,A18002,A18003,A18004,A13,A18005,rondelle_028,rondelle_029]
  Y = 64.6154
FEATURE [TechDraw::DrawSVGTemplate] Template002  label="Modèle002"
  Height = 210
  Orientation = 1
  Template = C:/Program Files/FreeCAD_0.19/data/Mod/TechDraw/Templates/A4_LandscapeTDteste.svg
  Width = 297
FEATURE [TechDraw::DrawProjGroupItem] View006
  CoarseView = false
  Direction = (0.57735,-0.57735,0.57735)
  Focus = 100
  HardHidden = false
  IsoCount = 0
  IsoHidden = false
  IsoVisible = false
  LockPosition = false
  Perspective = false
  Rotation = 0
  RotationVector = (1,0,0)
  Scale = 0.066667
  ScaleType = 2
  ScrubCount = 1
  SeamHidden = false
  SeamVisible = false
  SmoothHidden = false
  SmoothVisible = true
  Type = 0
  X = 81.1923
  XDirection = (0.707107,0.707107,0)
  XSource = -> [BB1,BB1001,BB3,BB2,BB1003,BB1004]
  Y = 133.718
FEATURE [TechDraw::DrawProjGroupItem] View007  label="Front001"
  CoarseView = false
  Direction = (0,-1,0)
  Focus = 100
  HardHidden = false
  IsoCount = 0
  IsoHidden = false
  IsoVisible = false
  LockPosition = true
  Perspective = false
  Rotation = 0
  RotationVector = (1,0,0)
  Scale = 0.066667
  ScaleType = 2
  ScrubCount = 1
  SeamHidden = false
  SeamVisible = false
  SmoothHidden = false
  SmoothVisible = true
  Type = 0
  X = 0
  XDirection = (1,0,0)
  XSource = <same value as first occurrence — deduplicated (x8 in doc)>
  Y = 0
FEATURE [TechDraw::DrawProjGroupItem] ProjItem002  label="Dessous"
  CoarseView = false
  Direction = (0,0,-1)
  Focus = 100
  HardHidden = false
  IsoCount = 0
  IsoHidden = false
  IsoVisible = false
  LockPosition = true
  Perspective = false
  Rotation = 0
  RotationVector = (1,0,0)
  ScaleType = 0
  ScrubCount = 1
  SeamHidden = false
  SeamVisible = false
  SmoothHidden = false
  SmoothVisible = true
  Type = 5
  X = 0
  XDirection = (1,0,0)
  XSource = <same value as first occurrence — deduplicated (x8 in doc)>
  Y = 77.9588
FEATURE [TechDraw::DrawProjGroupItem] ProjItem003  label="Gauche"
  CoarseView = false
  Direction = (-1,-1e-16,0)
  Focus = 100
  HardHidden = false
  IsoCount = 0
  IsoHidden = false
  IsoVisible = false
  LockPosition = true
  Perspective = false
  Rotation = 0
  RotationVector = (1,0,0)
  ScaleType = 0
  ScrubCount = 1
  SeamHidden = false
  SeamVisible = false
  SmoothHidden = false
  SmoothVisible = true
  Type = 1
  X = 125.101
  XDirection = (1e-16,-1,0)
  XSource = <same value as first occurrence — deduplicated (x8 in doc)>
  Y = 0
FEATURE [TechDraw::DrawProjGroup] ProjGroup001
  Anchor = -> View007
  AutoDistribute = true
  LockPosition = false
  ProjectionType = 0
  Rotation = 0
  Scale = 0.066667
  ScaleType = 2
  Views = -> [View007,ProjItem002,ProjItem003]
  X = 119.416
  XSource = -> [A2001,A1001,A1004,A3001,A3002,A4001,A4002,A2003,A5001,A5002,A6001,A7003,A7004,A8002,A9,A9001,A12,A12001,A12002,A12003,A13001,A14001,A2004,A2005,A14002,A14003,A14004,A11,A11001,A10,A10006,A15,A14008,A15001,A15002,A16,A16001,A17,A17001,A18,A18001,A18002,A18003,A18004,A13,A18005]
  Y = 47.5018
  spacingX = 15
  spacingY = 15
FEATURE [TechDraw::DrawProjGroupItem] View009  label="Front002"
  CoarseView = false
  Direction = (0,-1,0)
  Focus = 100
  HardHidden = false
  IsoCount = 0
  IsoHidden = false
  IsoVisible = false
  LockPosition = true
  Perspective = false
  Rotation = 0
  RotationVector = (1,0,0)
  Scale = 0.2
  ScaleType = 2
  ScrubCount = 1
  SeamHidden = false
  SeamVisible = false
  SmoothHidden = false
  SmoothVisible = true
  Type = 0
  X = 0
  XDirection = (1,0,0)
  XSource = -> [BB1,BB1001,BB3,BB2,BB1003,BB1004]
  Y = 0
FEATURE [TechDraw::DrawProjGroupItem] ProjItem004  label="Gauche001"
  CoarseView = false
  Direction = (-1,-1e-16,0)
  Focus = 100
  HardHidden = false
  IsoCount = 0
  IsoHidden = false
  IsoVisible = false
  LockPosition = false
  Perspective = false
  Rotation = 0
  RotationVector = (1,0,0)
  Scale = 0.2
  ScaleType = 2
  ScrubCount = 1
  SeamHidden = false
  SeamVisible = false
  SmoothHidden = false
  SmoothVisible = true
  Type = 1
  X = 78.5
  XDirection = (1e-16,-1,0)
  XSource = -> [BB1,BB1001,BB3,BB2,BB1003,BB1004]
  Y = 0
FEATURE [TechDraw::DrawProjGroup] ProjGroup002
  Anchor = -> View009
  AutoDistribute = true
  LockPosition = false
  ProjectionType = 0
  Rotation = 0
  Scale = 0.2
  ScaleType = 2
  Views = -> [View009,ProjItem004]
  X = 34.9744
  XSource = -> [BB1,BB1001,BB3,BB2,BB1003,BB1004]
  Y = 90.1923
  spacingX = 15
  spacingY = 15
FEATURE [TechDraw::DrawViewDimension] Dimension003  label="Cote003"
  AngleOverride = false
  Arbitrary = false
  ArbitraryTolerances = false
  BoxCorners = (2) [(-61,-68.5,-1e-07),(61,68.5,1e-07)]
  EqualTolerance = true
  ExtensionAngle = 0
  FormatSpec = %.2w
  FormatSpecOverTolerance = %+.2w
  FormatSpecUnderTolerance = %+.2w
  Inverted = false
  LineAngle = 0
  LockPosition = false
  MeasureType = 1
  OverTolerance = 0
  References2D = -> [ProjItem004]
  Rotation = 0
  ScaleType = 0
  TheoreticalExact = false
  Type = 2
  UnderTolerance = 0
  X = -45.2561
  Y = -67.38
FEATURE [TechDraw::DrawViewDimension] Dimension004  label="Cote004"
  AngleOverride = false
  Arbitrary = false
  ArbitraryTolerances = false
  BoxCorners = (2) [(-61,-68.5,-1e-07),(61,68.5,1e-07)]
  EqualTolerance = true
  ExtensionAngle = 0
  FormatSpec = %.2w
  FormatSpecOverTolerance = %+.2w
  FormatSpecUnderTolerance = %+.2w
  Inverted = false
  LineAngle = 0
  LockPosition = false
  MeasureType = 1
  OverTolerance = 0
  References2D = -> [ProjItem004]
  Rotation = 0
  ScaleType = 0
  TheoreticalExact = false
  Type = 0
  UnderTolerance = 0
  X = -39
  Y = 56.027
FEATURE [TechDraw::DrawViewDimension] Dimension005  label="Cote005"
  AngleOverride = false
  Arbitrary = false
  ArbitraryTolerances = false
  BoxCorners = (2) [(-61,-68.5,-1e-07),(61,68.5,1e-07)]
  EqualTolerance = true
  ExtensionAngle = 0
  FormatSpec = %.2w
  FormatSpecOverTolerance = %+.2w
  FormatSpecUnderTolerance = %+.2w
  Inverted = false
  LineAngle = 0
  LockPosition = false
  MeasureType = 1
  OverTolerance = 0
  References2D = -> [ProjItem004]
  Rotation = 0
  ScaleType = 0
  TheoreticalExact = false
  Type = 0
  UnderTolerance = 0
  X = 0
  Y = 56.027
FEATURE [TechDraw::DrawViewDimension] Dimension006  label="Cote006"
  AngleOverride = false
  Arbitrary = false
  ArbitraryTolerances = false
  BoxCorners = (2) [(-61,-68.5,-1e-07),(61,68.5,1e-07)]
  EqualTolerance = true
  ExtensionAngle = 0
  FormatSpec = %.2w
  FormatSpecOverTolerance = %+.2w
  FormatSpecUnderTolerance = %+.2w
  Inverted = false
  LineAngle = 0
  LockPosition = false
  MeasureType = 1
  OverTolerance = 0
  References2D = -> [ProjItem004]
  Rotation = 0
  ScaleType = 0
  TheoreticalExact = false
  Type = 0
  UnderTolerance = 0
  X = 39
  Y = 56.027
FEATURE [TechDraw::DrawViewDimension] Dimension007  label="Cote007"
  AngleOverride = false
  Arbitrary = false
  ArbitraryTolerances = false
  BoxCorners = (2) [(-61,-68.5,-1e-07),(61,68.5,1e-07)]
  EqualTolerance = true
  ExtensionAngle = 0
  FormatSpec = %.2w
  FormatSpecOverTolerance = %+.2w
  FormatSpecUnderTolerance = %+.2w
  Inverted = false
  LineAngle = 0
  LockPosition = false
  MeasureType = 1
  OverTolerance = 0
  References2D = -> [ProjItem004]
  Rotation = 0
  ScaleType = 0
  TheoreticalExact = false
  Type = 0
  UnderTolerance = 0
  X = -41.5
  Y = 76.7582
FEATURE [TechDraw::DrawLeaderLine] LeaderLine  label="Ligne de repère"
  AutoHorizontal = false
  EndSymbol = 0
  LockPosition = true
  RotatesWithParent = false
  Rotation = 0
  Scalable = false
  ScaleType = 0
  StartSymbol = 7
  WayPoints = (2) [(0,0,0),(-8.65063,39.088,0)]
  X = 13.4421
  Y = 40.5001
FEATURE [TechDraw::DrawViewBalloon] Balloon  label="Infobulle"
  BubbleShape = 3
  EndType = 0
  EndTypeScale = 1
  KinkLength = 5
  LockPosition = false
  OriginX = -1122.04
  OriginY = -115.259
  Rotation = 0
  ScaleType = 0
  ShapeScale = 1
  SourceView = -> View007
  Text = A13
  TextWrapLen = -1
  X = -982.08
  Y = -371.67
FEATURE [TechDraw::DrawViewBalloon] Balloon002  label="Infobulle002"
  BubbleShape = 3
  EndType = 0
  EndTypeScale = 1
  KinkLength = 5
  LockPosition = false
  OriginX = -1293.39
  OriginY = 66.7976
  Rotation = 0
  ScaleType = 0
  ShapeScale = 1
  SourceView = -> View007
  Text = A16
  TextWrapLen = -1
  X = -1563.24
  Y = 70.2859
FEATURE [TechDraw::DrawViewBalloon] Balloon003  label="Infobulle003"
  BubbleShape = 3
  EndType = 0
  EndTypeScale = 1
  KinkLength = 5
  LockPosition = false
  OriginX = -269.591
  OriginY = -100.266
  Rotation = 0
  ScaleType = 0
  ShapeScale = 1
  SourceView = -> View007
  Text = A5
  TextWrapLen = -1
  X = 60.3933
  Y = -258.621
FEATURE [TechDraw::DrawViewBalloon] Balloon004  label="Infobulle004"
  BubbleShape = 3
  EndType = 0
  EndTypeScale = 1
  KinkLength = 5
  LockPosition = false
  OriginX = 231.599
  OriginY = 79.6486
  Rotation = 0
  ScaleType = 0
  ShapeScale = 1
  SourceView = -> View007
  Text = A1
  TextWrapLen = -1
  X = 364.534
  Y = -187.94
FEATURE [TechDraw::DrawViewBalloon] Balloon005  label="Infobulle005"
  BubbleShape = 3
  EndType = 0
  EndTypeScale = 1
  KinkLength = 5
  LockPosition = false
  OriginX = 964.108
  OriginY = 135.336
  Rotation = 0
  ScaleType = 0
  ShapeScale = 1
  SourceView = -> View007
  Text = A18
  TextWrapLen = -1
  X = 476.914
  Y = 269.945
FEATURE [TechDraw::DrawViewBalloon] Balloon006  label="Infobulle006"
  BubbleShape = 3
  EndType = 0
  EndTypeScale = 1
  KinkLength = 5
  LockPosition = false
  OriginX = 1019.8
  OriginY = 236.003
  Rotation = 0
  ScaleType = 0
  ShapeScale = 1
  SourceView = -> View007
  Text = A9
  TextWrapLen = -1
  X = 1319.36
  Y = 423.053
FEATURE [TechDraw::DrawViewBalloon] Balloon009  label="Infobulle009"
  BubbleShape = 3
  EndType = 0
  EndTypeScale = 1
  KinkLength = 5
  LockPosition = false
  OriginX = -893.134
  OriginY = 99.9702
  Rotation = 0
  ScaleType = 0
  ShapeScale = 1
  SourceView = -> ProjItem002
  Text = A7
  TextWrapLen = -1
  X = -1169.26
  Y = 459.529
FEATURE [TechDraw::DrawViewBalloon] Balloon010  label="Infobulle010"
  BubbleShape = 3
  EndType = 0
  EndTypeScale = 1
  KinkLength = 5
  LockPosition = false
  OriginX = -1255
  OriginY = -0.00102179
  Rotation = 0
  ScaleType = 0
  ShapeScale = 1
  SourceView = -> ProjItem002
  Text = A2
  TextWrapLen = -1
  X = -566.055
  Y = 9.51412
FEATURE [TechDraw::DrawViewBalloon] Balloon011  label="Infobulle011"
  BubbleShape = 3
  EndType = 0
  EndTypeScale = 1
  KinkLength = 5
  LockPosition = false
  OriginX = 1148.31
  OriginY = -297.441
  Rotation = 0
  ScaleType = 0
  ShapeScale = 1
  SourceView = -> ProjItem002
  Text = A17
  TextWrapLen = -1
  X = 1265.9
  Y = -116.401
FEATURE [TechDraw::DrawViewBalloon] Balloon007  label="Infobulle007"
  BubbleShape = 3
  EndType = 0
  EndTypeScale = 1
  KinkLength = 5
  LockPosition = false
  OriginX = -1255
  OriginY = -131.643
  Rotation = 0
  ScaleType = 0
  ShapeScale = 1
  SourceView = -> View007
  Text = A12
  TextWrapLen = -1
  X = -1564.96
  Y = -134.325
FEATURE [TechDraw::DrawViewBalloon] Balloon013  label="Infobulle013"
  BubbleShape = 3
  EndType = 0
  EndTypeScale = 1
  KinkLength = 5
  LockPosition = false
  OriginX = 730
  OriginY = -1.3642e-12
  Rotation = 0
  ScaleType = 0
  ShapeScale = 1
  SourceView = -> ProjItem002
  Text = A8
  TextWrapLen = -1
  X = 1130.67
  Y = 73.4783
FEATURE [TechDraw::DrawViewBalloon] Balloon014  label="Infobulle014"
  BubbleShape = 3
  EndType = 0
  EndTypeScale = 1
  KinkLength = 5
  LockPosition = false
  OriginX = -742.5
  OriginY = 158.357
  Rotation = 0
  ScaleType = 0
  ShapeScale = 1
  SourceView = -> View007
  Text = A3
  TextWrapLen = -1
  X = -1580.33
  Y = 232.592
FEATURE [TechDraw::DrawViewBalloon] Balloon015  label="Infobulle015"
  BubbleShape = 3
  EndType = 0
  EndTypeScale = 1
  KinkLength = 5
  LockPosition = false
  OriginX = -286.587
  OriginY = 146.538
  Rotation = 0
  ScaleType = 0
  ShapeScale = 1
  SourceView = -> View007
  Text = A4
  TextWrapLen = -1
  X = -1578.05
  Y = 355.88
FEATURE [TechDraw::DrawViewBalloon] Balloon016  label="Infobulle016"
  BubbleShape = 3
  EndType = 0
  EndTypeScale = 1
  KinkLength = 5
  LockPosition = false
  OriginX = -0.00265948
  OriginY = 45.8566
  Rotation = 0
  ScaleType = 0
  ShapeScale = 1
  SourceView = -> ProjItem003
  Text = A2
  TextWrapLen = -1
  X = 504.625
  Y = 414.64
FEATURE [TechDraw::DrawViewBalloon] Balloon017  label="Infobulle017"
  BubbleShape = 3
  EndType = 0
  EndTypeScale = 1
  KinkLength = 5
  LockPosition = false
  OriginX = 19.1419
  OriginY = -214.025
  Rotation = 0
  ScaleType = 0
  ShapeScale = 1
  SourceView = -> ProjItem003
  Text = A6
  TextWrapLen = -1
  X = 63.2609
  Y = -406.443
FEATURE [TechDraw::DrawViewBalloon] Balloon018  label="Infobulle018"
  BubbleShape = 3
  EndType = 0
  EndTypeScale = 1
  KinkLength = 5
  LockPosition = false
  OriginX = 177.401
  OriginY = -109.166
  Rotation = 0
  ScaleType = 0
  ShapeScale = 1
  SourceView = -> ProjItem003
  Text = A15
  TextWrapLen = -1
  X = 538.259
  Y = -89.5215
FEATURE [TechDraw::DrawViewBalloon] Balloon019  label="Infobulle019"
  BubbleShape = 3
  EndType = 0
  EndTypeScale = 1
  KinkLength = 0
  LockPosition = false
  OriginX = -269.467
  OriginY = -230.57
  Rotation = 0
  ScaleType = 0
  ShapeScale = 1
  SourceView = -> View007
  Text = A10
  TextWrapLen = -1
  X = -69.1369
  Y = -333.157
FEATURE [TechDraw::DrawViewBalloon] Balloon020  label="Infobulle020"
  BubbleShape = 3
  EndType = 0
  EndTypeScale = 1
  KinkLength = 0
  LockPosition = false
  OriginX = -285
  OriginY = -231.643
  Rotation = 0
  ScaleType = 0
  ShapeScale = 1
  SourceView = -> View007
  Text = A11
  TextWrapLen = -1
  X = -475.893
  Y = -281.405
FEATURE [PartDesign::Plane] DatumPlane004
  AttachmentOffset = pos=(0,0,12.5) rot=(0,0,1;0rad)
  AttachmentSupport = -> [XY_Plane022]
  Length = 68.7083
  MapMode = 5
  Placement = pos=(0,0,12.5) rot=(0,0,1;0rad)
  ResizeMode = 0
  Width = 193.708
FEATURE [Sketcher::SketchObject] Sketch034
  ArcFitTolerance = 1e-06
  AttachmentSupport = -> [DatumPlane004]
  FullyConstrained = false
  MakeInternals = false
  MapMode = 5
  Placement = pos=(0,0,12.5) rot=(0,0,1;0rad)
  expr: Constraints[0] = Pad008.Length - 10 mm
  sketch-geometry (1):
    g0: Circle CenterX=0 CenterY=-140 CenterZ=0 NormalX=0 NormalY=0 NormalZ=1 AngleXU=0 Radius=16.367
  constraints (2):
    c: DistanceY(g0,g-1) = 140
    c: PointOnObject(g0,g-2)
FEATURE [PartDesign::Hole] Hole
  BaseFeature = -> Pad008
  CustomThreadClearance = 0
  Depth = 326.607
  DepthType = 1
  Diameter = 6
  DrillForDepth = false
  DrillPoint = 1
  DrillPointAngle = 118
  HoleCutCountersinkAngle = 90
  HoleCutCustomValues = false
  HoleCutDepth = 0
  HoleCutDiameter = 6.1
  HoleCutType = 0
  ModelThread = false
  Placement = pos=(0,0,0) rot=(1,0,0;1.5708rad)
  Profile = -> Sketch034
  Suppressed = false
  Tapered = false
  TaperedAngle = 90
  ThreadClass = 0
  ThreadDepth = 326.607
  ThreadDepthType = 0
  ThreadDirection = 0
  ThreadFit = 0
  ThreadSize = 0
  ThreadType = 0
  Threaded = false
  UseCustomThreadClearance = false
FEATURE [PartDesign::Body] Body
  AllowCompound = false
  Group = -> [Sketch012,Pad008,Sketch034,DatumPlane004,Hole]
  Origin = -> Origin022
  Tip = -> Hole
FEATURE [App::Part] Part  label="A10"
  Group = -> [Body,axe]
  Nom_de_la_piece = 'A10
  Origin = -> Origin021
  Reference_AP = fer rond Ø25
  longueur = 150
FEATURE [PartDesign::CoordinateSystem] LCS_Origin001
  AttacherType = Attacher::AttachEngine3D
  AttachmentSupport = -> [X_Axis047]
  MapMode = 2
FEATURE [PartDesign::CoordinateSystem] LCS_Origin002
  AttacherType = Attacher::AttachEngine3D
  AttachmentSupport = -> [X_Axis048]
  MapMode = 2
FEATURE [Sketcher::SketchObject] Sketch035
  ArcFitTolerance = 1e-06
  AttachmentSupport = -> [YZ_Plane046]
  FullyConstrained = true
  MakeInternals = false
  MapMode = 5
  Placement = pos=(0,0,0) rot=(0.57735,0.57735,0.57735;2.0944rad)
  sketch-geometry (4):
    g0: LineSegment StartX=-1 StartY=28 StartZ=0 EndX=-1 EndY=13 EndZ=0
    g1: LineSegment StartX=-1 StartY=13 StartZ=0 EndX=1 EndY=13 EndZ=0
    g2: LineSegment StartX=1 StartY=13 StartZ=0 EndX=1 EndY=28 EndZ=0
    g3: LineSegment StartX=1 StartY=28 StartZ=0 EndX=-1 EndY=28 EndZ=0
  constraints (11):
    c: Coincident(g0,g1)
    c: Coincident(g1,g2)
    c: Coincident(g2,g3)
    c: Coincident(g3,g0)
    c: Vertical(g0)
    c: Vertical(g2)
    c: Horizontal(g3)
    c: Symmetric(g0,g1,g-2)
    c: DistanceY(g-1,g1) = 13  'rayint'
    c: DistanceY(g-1,g2) = 28  'rayext'
    c: DistanceX(g3,g3) = 2  'ep'
FEATURE [App::Link] rondelle_026  label="rondelle 026"
  AttachedBy = #LCS_Origin001
  AttachedTo = A10006#axe
  AttachmentOffset = pos=(0,12.5,136) rot=(1,0,0;1.5708rad)
  LinkPlacement = pos=(1005,330,-312.5) rot=(0,0,1;0rad)
  LinkedObject = -> rondelle_25
  Placement = pos=(1005,330,-312.5) rot=(0,0,1;0rad)
  SolverId = Asm4EE
  expr: Placement = A10006.Placement * axe.Placement * AttachmentOffset * LCS_Origin001.Placement ^ -1
FEATURE [App::Link] rondelle_027  label="rondelle 027"
  AttachedBy = #LCS_Origin001
  AttachedTo = A10#axe
  AttachmentOffset = pos=(0,12.5,136) rot=(1,0,0;1.5708rad)
  LinkPlacement = pos=(1005,-330,-312.5) rot=(0,0,-1;3.14159rad)
  LinkedObject = -> rondelle_25
  Placement = pos=(1005,-330,-312.5) rot=(0,0,-1;3.14159rad)
  SolverId = Asm4EE
  expr: Placement = A10.Placement * axe.Placement * AttachmentOffset * LCS_Origin001.Placement ^ -1
FEATURE [App::Link] rondelle_028  label="rondelle 028"
  AttachedBy = #LCS_Origin001
  AttachedTo = A10#axe
  AttachmentOffset = pos=(0,12.5,52) rot=(1,0,0;1.5708rad)
  LinkPlacement = pos=(1005,-246,-312.5) rot=(0,0,-1;3.14159rad)
  LinkedObject = -> rondelle_25
  Placement = pos=(1005,-246,-312.5) rot=(0,0,-1;3.14159rad)
  SolverId = Asm4EE
  expr: Placement = A10.Placement * axe.Placement * AttachmentOffset * LCS_Origin001.Placement ^ -1
FEATURE [App::Link] rondelle_029  label="rondelle 029"
  AttachedBy = #LCS_Origin001
  AttachedTo = A10006#axe
  AttachmentOffset = pos=(0,12.5,52) rot=(1,0,0;1.5708rad)
  LinkPlacement = pos=(1005,246,-312.5) rot=(0,0,1;0rad)
  LinkedObject = -> rondelle_25
  Placement = pos=(1005,246,-312.5) rot=(0,0,1;0rad)
  SolverId = Asm4EE
  expr: Placement = A10006.Placement * axe.Placement * AttachmentOffset * LCS_Origin001.Placement ^ -1
FEATURE [PartDesign::CoordinateSystem] LCS_Origin003
  AttacherType = Attacher::AttachEngine3D
  AttachmentSupport = -> [X_Axis049]
  MapMode = 2
FEATURE [PartDesign::CoordinateSystem] LCS_Origin004
  AttacherType = Attacher::AttachEngine3D
  AttachmentSupport = -> [X_Axis050]
  MapMode = 2
FEATURE [Sketcher::SketchObject] Sketch036
  ArcFitTolerance = 1e-06
  AttachmentSupport = -> [XZ_Plane048]
  FullyConstrained = false
  MakeInternals = false
  MapMode = 5
  Placement = pos=(0,0,0) rot=(1,0,0;1.5708rad)
  sketch-geometry (11):
    g0: Circle [constr] CenterX=0 CenterY=0 CenterZ=0 NormalX=0 NormalY=0 NormalZ=1 AngleXU=0 Radius=13.75
    g1: LineSegment [constr] StartX=0 StartY=-40 StartZ=0 EndX=0 EndY=40 EndZ=0
    g2: Circle [constr] CenterX=-10 CenterY=30 CenterZ=0 NormalX=0 NormalY=0 NormalZ=1 AngleXU=0 Radius=10
    g3: GeomPoint [constr] X=0 Y=30 Z=0
    g4: LineSegment [constr] StartX=0 StartY=40 StartZ=0 EndX=-69.1627 EndY=40 EndZ=0
    g5: LineSegment StartX=0 StartY=-40 StartZ=0 EndX=0 EndY=30 EndZ=0
    g6: ArcOfCircle CenterX=-10 CenterY=30 CenterZ=0 NormalX=0 NormalY=0 NormalZ=1 AngleXU=0 Radius=10 StartAngle=4.06135e-09 EndAngle=4.58938
    g7: ArcOfCircle CenterX=-11.8728 CenterY=14.8514 CenterZ=0 NormalX=0 NormalY=0 NormalZ=1 AngleXU=0 Radius=5.26396 StartAngle=5.38202 EndAngle=7.73097
    g8: ArcOfCircle CenterX=0 CenterY=0 CenterZ=0 NormalX=0 NormalY=0 NormalZ=1 AngleXU=0 Radius=13.75 StartAngle=2.24702 EndAngle=4.04719
    g9: ArcOfCircle CenterX=-12.0115 CenterY=-15.2346 CenterZ=0 NormalX=0 NormalY=0 NormalZ=1 AngleXU=0 Radius=5.65039 StartAngle=5.15136 EndAngle=7.18037
    g10: LineSegment StartX=-9.61003 StartY=-20.3493 StartZ=0 EndX=-12.9682 EndY=-21.926 EndZ=0
  constraints (21):
    c: Diameter(g0) = 27.5
    c: Coincident(g0,g-1)
    c: Distance(g1) = 80
    c: Vertical(g1)
    c: Diameter(g2) = 20
    c: PointOnObject(g3,g2)
    c: PointOnObject(g3,g1)
    c: Coincident(g4,g1)
    c: Horizontal(g4)
    c: Tangent(g4,g2)
    c: Symmetric(g1,g1,g0)
    c: Coincident(g5,g1)
    c: Coincident(g5,g3)
    c: Coincident(g6,g2)
    c: Coincident(g6,g3)
    c: PointOnObject(g7,g0)
    c: Coincident(g7,g6)
    c: Coincident(g8,g0)
    c: Coincident(g8,g7)
    c: Coincident(g9,g8)
    c: Tangent(g10,g9) = 1.5708
FEATURE [PartDesign::Plane] DatumPlane005
  AttachmentSupport = -> [Sketch036]
  Length = 60
  MapMode = 7
  Placement = pos=(0,-8.9e-15,-40) rot=(0,1,0;3.14159rad)
  ResizeMode = 0
  Width = 60
FEATURE [Sketcher::SketchObject] Sketch037
  ArcFitTolerance = 1e-06
  AttachmentSupport = -> [DatumPlane005]
  FullyConstrained = true
  MakeInternals = false
  MapMode = 5
  Placement = pos=(0,-8.9e-15,-40) rot=(0,1,0;3.14159rad)
  sketch-geometry (1):
    g0: Circle CenterX=0 CenterY=0 CenterZ=0 NormalX=0 NormalY=0 NormalZ=1 AngleXU=0 Radius=2.5
  constraints (2):
    c: Diameter(g0) = 5
    c: Coincident(g0,g-1)
FEATURE [PartDesign::AdditivePipe] AdditivePipe001
  AuxilleryCurvelinear = true
  AuxillerySpineTangent = false
  Binormal = (0,0,0)
  Mode = 0
  Placement = pos=(0,-8.9e-15,-40) rot=(0,1,0;3.14159rad)
  Profile = -> Sketch037
  Spine = -> Sketch036
  SpineTangent = false
  Suppressed = false
  Transformation = 0
  Transition = 0
FEATURE [PartDesign::Body] goupille
  AllowCompound = false
  Group = -> [LCS_Origin004,Sketch036,DatumPlane005,Sketch037,AdditivePipe001]
  Origin = -> Origin048
  Tip = -> AdditivePipe001
FEATURE [App::Part] goupille_elastique_5_x_80  label="goupille elastique 5 x 80"
  Group = -> [LCS_Origin003,goupille]
  Origin = -> Origin047
FEATURE [App::Link] goupille_elastique_5_x_081  label="goupille elastique 5 x 081"
  AttachedBy = #LCS_Origin003
  AttachedTo = A10#axe
  AttachmentOffset = pos=(0,12.5,140) rot=(1,0,0;1.5708rad)
  LinkPlacement = pos=(1005,-334,-312.5) rot=(0,0,-1;3.14159rad)
  LinkedObject = -> goupille_elastique_5_x_80
  Placement = pos=(1005,-334,-312.5) rot=(0,0,-1;3.14159rad)
  SolverId = Asm4EE
  expr: Placement = A10.Placement * axe.Placement * AttachmentOffset * LCS_Origin003.Placement ^ -1
FEATURE [App::Link] goupille_elastique_5_x_082  label="goupille elastique 5 x 082"
  AttachedBy = #LCS_Origin003
  AttachedTo = A10006#axe
  AttachmentOffset = pos=(0,12.5,140) rot=(1,0,0;1.5708rad)
  LinkPlacement = pos=(1005,334,-312.5) rot=(0,0,1;0rad)
  LinkedObject = -> goupille_elastique_5_x_80
  Placement = pos=(1005,334,-312.5) rot=(0,0,1;0rad)
  SolverId = Asm4EE
  expr: Placement = A10006.Placement * axe.Placement * AttachmentOffset * LCS_Origin003.Placement ^ -1
FEATURE [App::Part] Model
  Configuration = 0
  Group = -> [LCS_Origin,Constraints,Variables,A2001,A1001,A1004,A3001,A3002,A4001,A4002,A2003,A5001,A5002,A6001,A7003,A7004,A8002,A9,A9001,Sketch014,A12,A12001,A12002,A12003,A13001,A14001,A2004,A2005,A14002,A14003,A14004,A11,A11001,A10,A10006,Roue_increvable___389___axe25_L_82001,Roue_increvable___389___axe25_L_82002,A15,A14008,A15001,A15002,A16,A16001,BB1,BB1001,BB3,BB2,BB1003,BB1004,A17,A17001,A18,A18001,+11 more]
  Origin = -> Origin
  Type = Assembly4 Model
FEATURE [TechDraw::DrawProjGroupItem] View  label="Front"
  CoarseView = false
  Direction = (0,-1,0)
  Focus = 100
  HardHidden = false
  IsoCount = 0
  IsoHidden = false
  IsoVisible = false
  LockPosition = true
  Perspective = false
  Rotation = 0
  RotationVector = (1,0,0)
  Scale = 0.05
  ScaleType = 2
  ScrubCount = 1
  SeamHidden = false
  SeamVisible = false
  SmoothHidden = false
  SmoothVisible = true
  Source = -> [Model]
  Type = 0
  X = 0
  XDirection = (1,0,0)
  Y = 0
FEATURE [TechDraw::DrawProjGroupItem] ProjItem001  label="Dessus"
  CoarseView = false
  Direction = (0,0,1)
  Focus = 100
  HardHidden = false
  IsoCount = 0
  IsoHidden = false
  IsoVisible = false
  LockPosition = true
  Perspective = false
  Rotation = 0
  RotationVector = (1,0,0)
  ScaleType = 0
  ScrubCount = 1
  SeamHidden = false
  SeamVisible = false
  SmoothHidden = false
  SmoothVisible = false
  Source = -> [Model]
  Type = 4
  X = 0
  XDirection = (1,0,0)
  Y = 70.4662
FEATURE [TechDraw::DrawProjGroupItem] ProjItem  label="Avant en haut à droite"
  CoarseView = false
  Direction = (0.57735,-0.57735,0.57735)
  Focus = 100
  HardHidden = false
  IsoCount = 0
  IsoHidden = false
  IsoVisible = false
  LockPosition = true
  Perspective = false
  Rotation = 0
  RotationVector = (1,0,0)
  ScaleType = 0
  ScrubCount = 1
  SeamHidden = false
  SeamVisible = false
  SmoothHidden = false
  SmoothVisible = true
  Source = -> [Model]
  Type = 7
  X = 147.302
  XDirection = (0.707107,0.707107,0)
  Y = 97.4798
FEATURE [TechDraw::DrawProjGroup] ProjGroup
  Anchor = -> View
  AutoDistribute = true
  LockPosition = false
  ProjectionType = 0
  Rotation = 0
  Scale = 0.05
  ScaleType = 2
  Source = -> [Model]
  Views = -> [View,ProjItem001,ProjItem]
  X = 82.3141
  Y = 56.2019
  spacingX = 15
  spacingY = 15
FEATURE [TechDraw::DrawViewDimExtent] DimExtent
  AngleOverride = false
  Arbitrary = false
  ArbitraryTolerances = false
  DirExtent = 1
  EqualTolerance = true
  ExtensionAngle = 0
  FormatSpec = %.2w
  FormatSpecOverTolerance = %+.2w
  FormatSpecUnderTolerance = %+.2w
  Inverted = false
  LineAngle = 0
  LockPosition = false
  MeasureType = 1
  OverTolerance = 0
  References2D = -> [ProjItem001]
  Rotation = 0
  ScaleType = 0
  Source = -> [ProjItem001]
  TheoreticalExact = false
  Type = 2
  UnderTolerance = 0
  X = -72.7624
  Y = 8.40417
FEATURE [TechDraw::DrawViewDimExtent] DimExtent001
  AngleOverride = false
  Arbitrary = false
  ArbitraryTolerances = false
  DirExtent = 0
  EqualTolerance = true
  ExtensionAngle = 0
  FormatSpec = %.2w
  FormatSpecOverTolerance = %+.2w
  FormatSpecUnderTolerance = %+.2w
  Inverted = false
  LineAngle = 0
  LockPosition = false
  MeasureType = 1
  OverTolerance = 0
  References2D = -> [ProjItem001]
  Rotation = 0
  ScaleType = 0
  Source = -> [ProjItem001]
  TheoreticalExact = false
  Type = 1
  UnderTolerance = 0
  X = 0
  Y = 29.8569
FEATURE [TechDraw::DrawViewDimension] Dimension  label="Cote"
  AngleOverride = false
  Arbitrary = false
  ArbitraryTolerances = false
  BoxCorners = (2) [(-65.375,-17.2,-1e-07),(65.375,17.2,1e-07)]
  EqualTolerance = true
  ExtensionAngle = 0
  FormatSpec = %.2w
  FormatSpecOverTolerance = %+.2w
  FormatSpecUnderTolerance = %+.2w
  Inverted = false
  LineAngle = 0
  LockPosition = false
  MeasureType = 1
  OverTolerance = 0
  References2D = -> [ProjItem001]
  Rotation = 0
  ScaleType = 0
  TheoreticalExact = false
  Type = 0
  UnderTolerance = 0
  X = -10.2604
  Y = -24.9269
FEATURE [TechDraw::DrawViewDimension] Dimension001  label="Cote001"
  AngleOverride = false
  Arbitrary = false
  ArbitraryTolerances = false
  BoxCorners = (2) [(-65.375,-17.2,-1e-07),(65.375,17.2,1e-07)]
  EqualTolerance = true
  ExtensionAngle = 0
  FormatSpec = %.2w
  FormatSpecOverTolerance = %+.2w
  FormatSpecUnderTolerance = %+.2w
  Inverted = false
  LineAngle = 0
  LockPosition = false
  MeasureType = 1
  OverTolerance = 0
  References2D = -> [ProjItem001]
  Rotation = 0
  ScaleType = 0
  TheoreticalExact = false
  Type = 0
  UnderTolerance = 0
  X = 73.1222
  Y = 0
FEATURE [TechDraw::DrawViewDimExtent] DimExtent002
  AngleOverride = false
  Arbitrary = false
  ArbitraryTolerances = false
  DirExtent = 1
  EqualTolerance = true
  ExtensionAngle = 0
  FormatSpec = %.2w
  FormatSpecOverTolerance = %+.2w
  FormatSpecUnderTolerance = %+.2w
  Inverted = false
  LineAngle = 0
  LockPosition = false
  MeasureType = 1
  OverTolerance = 0
  References2D = -> [View]
  Rotation = 0
  ScaleType = 0
  Source = -> [View]
  TheoreticalExact = false
  Type = 2
  UnderTolerance = 0
  X = -72.6462
  Y = 0
FEATURE [TechDraw::DrawViewDimension] Dimension002  label="Cote002"
  AngleOverride = false
  Arbitrary = false
  ArbitraryTolerances = false
  BoxCorners = (2) [(-65.375,-28.375,-1e-07),(65.375,28.3687,1e-07)]
  EqualTolerance = true
  ExtensionAngle = 0
  FormatSpec = %.2w
  FormatSpecOverTolerance = %+.2w
  FormatSpecUnderTolerance = %+.2w
  Inverted = false
  LineAngle = 0
  LockPosition = false
  MeasureType = 1
  OverTolerance = 0
  References2D = -> [View]
  Rotation = 0
  ScaleType = 0
  TheoreticalExact = false
  Type = 2
  UnderTolerance = 0
  X = -51.6484
  Y = 13.125
FEATURE [TechDraw::DrawProjGroupItem] View010
  CoarseView = false
  Direction = (0.57735,-0.57735,0.57735)
  Focus = 100
  HardHidden = false
  IsoCount = 0
  IsoHidden = false
  IsoVisible = false
  LockPosition = false
  Perspective = false
  Rotation = 0
  RotationVector = (1,0,0)
  Scale = 0.066667
  ScaleType = 2
  ScrubCount = 1
  SeamHidden = false
  SeamVisible = false
  SmoothHidden = false
  SmoothVisible = true
  Type = 0
  X = 210.702
  XDirection = (0.707107,0.707107,0)
  XSource = -> [rondelle_026,goupille_elastique_5_x_082]
  Y = 96.9368
FEATURE [TechDraw::DrawProjGroupItem] View011
  CoarseView = false
  Direction = (0.57735,-0.57735,0.57735)
  Focus = 100
  HardHidden = false
  IsoCount = 0
  IsoHidden = false
  IsoVisible = false
  LockPosition = false
  Perspective = false
  Rotation = 0
  RotationVector = (1,0,0)
  Scale = 0.066667
  ScaleType = 2
  ScrubCount = 1
  SeamHidden = false
  SeamVisible = false
  SmoothHidden = false
  SmoothVisible = true
  Type = 0
  X = 102.137
  XDirection = (0.707107,0.707107,0)
  XSource = -> [rondelle_027,goupille_elastique_5_x_081]
  Y = 23.792
FEATURE [TechDraw::DrawViewBalloon] Balloon022  label="Infobulle022"
  BubbleShape = 3
  EndType = 0
  EndTypeScale = 1
  KinkLength = 5
  LockPosition = false
  OriginX = -93.9744
  OriginY = 26.9231
  Rotation = 0
  ScaleType = 0
  ShapeScale = 1
  SourceView = -> ProjItem004
  Text = BB2
  TextWrapLen = -1
  X = 6.02564
  Y = 126.923
FEATURE [TechDraw::DrawViewBalloon] Balloon023  label="Infobulle023"
  BubbleShape = 3
  EndType = 0
  EndTypeScale = 1
  KinkLength = 5
  LockPosition = false
  OriginX = -390.128
  OriginY = -29.1667
  Rotation = 0
  ScaleType = 0
  ShapeScale = 1
  SourceView = -> ProjItem004
  Text = BB1
  TextWrapLen = -1
  X = -485.321
  Y = 102.244
FEATURE [TechDraw::DrawViewBalloon] Balloon024  label="Infobulle024"
  BubbleShape = 3
  EndType = 0
  EndTypeScale = 1
  KinkLength = 5
  LockPosition = false
  OriginX = 291.923
  OriginY = 26.9231
  Rotation = 0
  ScaleType = 0
  ShapeScale = 1
  SourceView = -> ProjItem004
  Text = BB1
  TextWrapLen = -1
  X = 181.026
  Y = 126.923
FEATURE [TechDraw::DrawSVGTemplate] Template007  label="Modèle007"
  Height = 210
  Orientation = 1
  Template = C:/Program Files/FreeCAD_0.19/data/Mod/TechDraw/Templates/A4_LandscapeTDteste.svg
  Width = 297
FEATURE [TechDraw::DrawProjGroupItem] View012  label="Front003"
  CoarseView = false
  Direction = (0,0,1)
  Focus = 100
  HardHidden = false
  IsoCount = 0
  IsoHidden = false
  IsoVisible = false
  LockPosition = true
  Perspective = false
  Rotation = 0
  RotationVector = (1,0,0)
  Scale = 0.1
  ScaleType = 2
  ScrubCount = 1
  SeamHidden = false
  SeamVisible = false
  SmoothHidden = false
  SmoothVisible = true
  Type = 0
  X = 0
  XDirection = (1,0,0)
  XSource = -> [A2001,A1001,A1004,A7003,A7004,A8002]
  Y = 0
FEATURE [TechDraw::DrawProjGroupItem] ProjItem005  label="Dessus001"
  CoarseView = false
  Direction = (0,1,0)
  Focus = 100
  HardHidden = false
  IsoCount = 0
  IsoHidden = false
  IsoVisible = false
  LockPosition = false
  Perspective = false
  Rotation = 0
  RotationVector = (1,0,0)
  ScaleType = 0
  ScrubCount = 1
  SeamHidden = false
  SeamVisible = false
  SmoothHidden = false
  SmoothVisible = true
  Type = 4
  X = 0
  XDirection = (1,0,0)
  XSource = -> [A2001,A1001,A1004,A7003,A7004,A8002]
  Y = -46.75
FEATURE [TechDraw::DrawProjGroup] ProjGroup003
  Anchor = -> View012
  AutoDistribute = true
  LockPosition = false
  ProjectionType = 0
  Rotation = 0
  Scale = 0.1
  ScaleType = 2
  Views = -> [View012,ProjItem005]
  X = 146.183
  XSource = -> [A2001,A1001,A1004,A7003,A7004,A8002]
  Y = 108.045
  spacingX = 15
  spacingY = 15
FEATURE [TechDraw::DrawSVGTemplate] Template008  label="Modèle008"
  Height = 210
  Orientation = 1
  Template = C:/Program Files/FreeCAD_0.19/data/Mod/TechDraw/Templates/A4_LandscapeTDteste.svg
  Width = 297
FEATURE [TechDraw::DrawSVGTemplate] Template009  label="Modèle009"
  Height = 210
  Orientation = 1
  Template = C:/Program Files/FreeCAD_0.19/data/Mod/TechDraw/Templates/A4_LandscapeTDteste.svg
  Width = 297
FEATURE [TechDraw::DrawSVGTemplate] Template010  label="Modèle010"
  Height = 210
  Orientation = 1
  Template = C:/Program Files/FreeCAD_0.19/data/Mod/TechDraw/Templates/A4_LandscapeTDteste.svg
  Width = 297
FEATURE [TechDraw::DrawSVGTemplate] Template011  label="Modèle011"
  Height = 210
  Orientation = 1
  Template = C:/Program Files/FreeCAD_0.19/data/Mod/TechDraw/Templates/A4_LandscapeTDteste.svg
  Width = 297
FEATURE [TechDraw::DrawSVGTemplate] Template012  label="Modèle012"
  Height = 210
  Orientation = 1
  Template = C:/Program Files/FreeCAD_0.19/data/Mod/TechDraw/Templates/A4_LandscapeTDteste.svg
  Width = 297
FEATURE [TechDraw::DrawProjGroupItem] View015  label="Front006"
  CoarseView = false
  Direction = (0,-1,0)
  Focus = 100
  HardHidden = false
  IsoCount = 0
  IsoHidden = false
  IsoVisible = false
  LockPosition = true
  Perspective = false
  Rotation = 0
  RotationVector = (1,0,0)
  Scale = 0.0833333
  ScaleType = 2
  ScrubCount = 1
  SeamHidden = false
  SeamVisible = false
  SmoothHidden = false
  SmoothVisible = true
  Type = 0
  X = 0
  XDirection = (-1,0,0)
  XSource = -> [A2001,A1001,A1004,A2003,A5001,A5002,A6001,A7003,A7004,A8002,A12,A12001,A12002,A12003,A13001,A14001,A2004,A14003,A11,A14004,A2005,A14002,A15,A14008,A15001,A15002,A18002,A18003,A18004,A13,A18005,A11001]
  Y = 0
FEATURE [TechDraw::DrawProjGroupItem] ProjItem008  label="Gauche003"
  CoarseView = false
  Direction = (1,-1e-16,0)
  Focus = 100
  HardHidden = false
  IsoCount = 0
  IsoHidden = false
  IsoVisible = false
  LockPosition = false
  Perspective = false
  Rotation = 0
  RotationVector = (1,0,0)
  Scale = 0.0833333
  ScaleType = 2
  ScrubCount = 1
  SeamHidden = false
  SeamVisible = false
  SmoothHidden = false
  SmoothVisible = true
  Type = 1
  X = 136.667
  XDirection = (-1e-16,-1,0)
  XSource = <same value as first occurrence — deduplicated (x3 in doc)>
  Y = 0
FEATURE [TechDraw::DrawProjGroup] ProjGroup006
  Anchor = -> View015
  AutoDistribute = true
  LockPosition = false
  ProjectionType = 0
  Rotation = 0
  Scale = 0.0833333
  ScaleType = 2
  Views = -> [View015,ProjItem008]
  X = 116.186
  XSource = <same value as first occurrence — deduplicated (x3 in doc)>
  Y = 95.3239
  spacingX = 15
  spacingY = 15
FEATURE [TechDraw::DrawProjGroupItem] View016  label="Front007"
  CoarseView = false
  Direction = (0,-1,0)
  Focus = 100
  HardHidden = false
  IsoCount = 0
  IsoHidden = false
  IsoVisible = false
  LockPosition = true
  Perspective = false
  Rotation = 0
  RotationVector = (1,0,0)
  Scale = 0.083333
  ScaleType = 2
  ScrubCount = 1
  SeamHidden = false
  SeamVisible = false
  SmoothHidden = false
  SmoothVisible = true
  Type = 0
  X = 0
  XDirection = (-1,0,0)
  XSource = -> [A2001,A1001,A1004,A2003,A5001,A5002,A6001,A7003,A7004,A8002,A12,A12001,A12002,A12003,A11001,A11,A2004,A2005]
  Y = 0
FEATURE [TechDraw::DrawProjGroupItem] ProjItem009  label="Gauche004"
  CoarseView = false
  Direction = (1,-1e-16,0)
  Focus = 100
  HardHidden = false
  IsoCount = 0
  IsoHidden = false
  IsoVisible = false
  LockPosition = true
  Perspective = false
  Rotation = 0
  RotationVector = (1,0,0)
  ScaleType = 0
  ScrubCount = 1
  SeamHidden = false
  SeamVisible = false
  SmoothHidden = false
  SmoothVisible = true
  Type = 1
  X = 136.666
  XDirection = (-1e-16,-1,0)
  XSource = -> [A2001,A1001,A1004,A2003,A5001,A5002,A6001,A7003,A7004,A8002,A12,A12001,A12002,A12003,A11001,A11,A2004,A2005]
  Y = 0
FEATURE [TechDraw::DrawProjGroup] ProjGroup007
  Anchor = -> View016
  AutoDistribute = true
  LockPosition = false
  ProjectionType = 0
  Rotation = 0
  Scale = 0.083333
  ScaleType = 2
  Views = -> [View016,ProjItem009]
  X = 112.278
  XSource = -> [A2001,A1001,A1004,A2003,A5001,A5002,A6001,A7003,A7004,A8002,A12,A12001,A12002,A12003,A11001,A11,A2004,A2005]
  Y = 89.5854
  spacingX = 15
  spacingY = 15
FEATURE [TechDraw::DrawGeomHatch] GeomHatch002  label="Hachures géométriques002"
  FilePattern = <userpath>\Desktop\bureau\FreeCAD_1.0.0-conda-Windows-x86_64-py311\data\Mod/TechDraw/PAT/FCPAT.pat
  NamePattern = Diamond2
  PatternOffset = (0,0,0)
  PatternRotation = 0
  ScalePattern = 1
  Source = -> View016 [Face2,Face6,Face3]
FEATURE [TechDraw::DrawGeomHatch] GeomHatch003  label="Hachures géométriques003"
  FilePattern = <userpath>\Desktop\bureau\FreeCAD_1.0.0-conda-Windows-x86_64-py311\data\Mod/TechDraw/PAT/FCPAT.pat
  NamePattern = Diamond2
  PatternOffset = (0,0,0)
  PatternRotation = 0
  ScalePattern = 1
  Source = -> ProjItem009 [Face6,Face7,Face4,Face8,Face5,Face20,Face19]
FEATURE [TechDraw::DrawGeomHatch] GeomHatch  label="Hachures géométriques"
  FilePattern = <userpath>\Desktop\bureau\FreeCAD_1.0.0-conda-Windows-x86_64-py311\data\Mod/TechDraw/PAT/FCPAT.pat
  NamePattern = Diamond2
  PatternOffset = (0,0,0)
  PatternRotation = 0
  ScalePattern = 1
  Source = -> View015 [Face15,Face8,Face6,Face7,Face9]
FEATURE [TechDraw::DrawGeomHatch] GeomHatch004  label="Hachures géométriques004"
  FilePattern = <userpath>\Desktop\bureau\FreeCAD_1.0.0-conda-Windows-x86_64-py311\data\Mod/TechDraw/PAT/FCPAT.pat
  NamePattern = Diamond2
  PatternOffset = (0,0,0)
  PatternRotation = 0
  ScalePattern = 1
  Source = -> ProjItem008 [Face7,Face8]
FEATURE [TechDraw::DrawGeomHatch] GeomHatch005  label="Hachures géométriques005"
  FilePattern = <userpath>\Desktop\bureau\FreeCAD_1.0.0-conda-Windows-x86_64-py311\data\Mod/TechDraw/PAT/FCPAT.pat
  NamePattern = Diamond2
  PatternOffset = (0,0,0)
  PatternRotation = 0
  ScalePattern = 1
  Source = -> ProjItem008 [Face17,Face18]
FEATURE [PartDesign::Revolution] Revolution001
  Angle = 360
  Angle2 = 60
  Axis = (0,1,0)
  Base = (0,0,0)
  Placement = pos=(0,0,0) rot=(1,1,1;2.0944rad)
  Profile = -> Sketch035
  ReferenceAxis = -> Sketch035 [H_Axis]
  Suppressed = false
  Type = 0
FEATURE [PartDesign::Body] rondellle
  AllowCompound = false
  Group = -> [LCS_Origin002,Sketch035,Revolution001]
  Origin = -> Origin046
  Tip = -> Revolution001
FEATURE [App::Part] rondelle_25  label="rondelle 25"
  Group = -> [LCS_Origin001,rondellle]
  Origin = -> Origin045
FEATURE [App::DocumentObjectGroup] Parts
  Group = -> [A1,A2,A3,A4,Roue_increvable___389___axe25_L_82,A5,A6,A7,A8,A8003,Part,Part001,Part002,Part003,Part004,Part005,Part006,Part008,Part009,Part007,Part010,Part011,rondelle_25,goupille_elastique_5_x_80]
FEATURE [TechDraw::DrawProjGroupItem] View017
  CoarseView = false
  Direction = (0.57735,-0.57735,0.57735)
  Focus = 100
  HardHidden = false
  IsoCount = 0
  IsoHidden = false
  IsoVisible = false
  LockPosition = true
  Perspective = false
  Rotation = 0
  RotationVector = (1,0,0)
  Scale = 0.2
  ScaleType = 2
  ScrubCount = 1
  SeamHidden = false
  SeamVisible = false
  SmoothHidden = false
  SmoothVisible = true
  Type = 0
  X = 111.224
  XDirection = (0.707107,0.707107,0)
  XSource = -> [A10]
  Y = 80.7781
FEATURE [TechDraw::DrawProjGroupItem] View018
  CoarseView = false
  Direction = (0.57735,-0.57735,0.57735)
  Focus = 100
  HardHidden = false
  IsoCount = 0
  IsoHidden = false
  IsoVisible = false
  LockPosition = true
  Perspective = false
  Rotation = 0
  RotationVector = (1,0,0)
  Scale = 0.2
  ScaleType = 2
  ScrubCount = 1
  SeamHidden = false
  SeamVisible = false
  SmoothHidden = false
  SmoothVisible = true
  Type = 0
  X = 92.2089
  XDirection = (0.707107,0.707107,0)
  XSource = -> [rondelle_026]
  Y = 69.9756
FEATURE [TechDraw::DrawProjGroupItem] View019
  CoarseView = false
  Direction = (0.57735,-0.57735,0.57735)
  Focus = 100
  HardHidden = false
  IsoCount = 0
  IsoHidden = false
  IsoVisible = false
  LockPosition = true
  Perspective = false
  Rotation = 0
  RotationVector = (1,0,0)
  Scale = 0.2
  ScaleType = 2
  ScrubCount = 1
  SeamHidden = false
  SeamVisible = false
  SmoothHidden = false
  SmoothVisible = true
  Type = 0
  X = 63.238
  XDirection = (0.707107,0.707107,0)
  XSource = -> [Roue_increvable___389___axe25_L_82001]
  Y = 53.424
FEATURE [TechDraw::DrawProjGroupItem] View020
  CoarseView = false
  Direction = (0.57735,-0.57735,0.57735)
  Focus = 100
  HardHidden = false
  IsoCount = 0
  IsoHidden = false
  IsoVisible = false
  LockPosition = true
  Perspective = false
  Rotation = 0
  RotationVector = (1,0,0)
  Scale = 0.2
  ScaleType = 2
  ScrubCount = 1
  SeamHidden = false
  SeamVisible = false
  SmoothHidden = false
  SmoothVisible = true
  Type = 0
  X = 43.632
  XDirection = (0.707107,0.707107,0)
  XSource = -> [rondelle_026]
  Y = 41.7812
FEATURE [TechDraw::DrawProjGroupItem] View021
  CoarseView = false
  Direction = (0.57735,-0.57735,0.57735)
  Focus = 100
  HardHidden = false
  IsoCount = 0
  IsoHidden = false
  IsoVisible = false
  LockPosition = true
  Perspective = false
  Rotation = 0
  RotationVector = (1,0,0)
  Scale = 0.2
  ScaleType = 2
  ScrubCount = 1
  SeamHidden = false
  SeamVisible = false
  SmoothHidden = false
  SmoothVisible = true
  Type = 0
  X = 33.3833
  XDirection = (0.707107,0.707107,0)
  XSource = -> [goupille_elastique_5_x_081]
  Y = 36.4851
FEATURE [TechDraw::DrawProjGroupItem] View022
  CoarseView = false
  Direction = (0,0,1)
  Focus = 100
  HardHidden = false
  IsoCount = 0
  IsoHidden = false
  IsoVisible = false
  LockPosition = true
  Perspective = false
  Rotation = 0
  RotationVector = (1,0,0)
  Scale = 0.666667
  ScaleType = 2
  ScrubCount = 1
  SeamHidden = false
  SeamVisible = false
  SmoothHidden = false
  SmoothVisible = true
  Type = 0
  X = 263.224
  XDirection = (1,0,0)
  XSource = -> [rondelle_028,A10]
  Y = 80.7781
FEATURE [TechDraw::DrawProjGroupItem] View023  label="Front008"
  CoarseView = false
  Direction = (0,1,0)
  Focus = 100
  HardHidden = false
  IsoCount = 0
  IsoHidden = false
  IsoVisible = false
  LockPosition = true
  Perspective = false
  Rotation = 0
  RotationVector = (1,0,0)
  Scale = 0.2
  ScaleType = 2
  ScrubCount = 1
  SeamHidden = false
  SeamVisible = false
  SmoothHidden = false
  SmoothVisible = true
  Type = 0
  X = 0
  XDirection = (-1,0,0)
  XSource = -> [A9001,A17001]
  Y = 0
FEATURE [TechDraw::DrawProjGroupItem] ProjItem010  label="Avant en bas à gauche"
  CoarseView = false
  Direction = (0.57735,0.57735,-0.57735)
  Focus = 100
  HardHidden = false
  IsoCount = 0
  IsoHidden = false
  IsoVisible = false
  LockPosition = true
  Perspective = false
  Rotation = 0
  RotationVector = (1,0,0)
  ScaleType = 0
  ScrubCount = 1
  SeamHidden = false
  SeamVisible = false
  SmoothHidden = false
  SmoothVisible = true
  Type = 8
  X = 4.8385
  XDirection = (-0.707107,0.707107,0)
  XSource = -> [A9001,A17001]
  Y = -100.637
FEATURE [TechDraw::DrawProjGroup] ProjGroup008
  Anchor = -> View023
  AutoDistribute = true
  LockPosition = false
  ProjectionType = 0
  Rotation = 0
  Scale = 0.2
  ScaleType = 2
  Views = -> [View023,ProjItem010]
  X = 252.763
  XSource = -> [A9001,A17001]
  Y = 151.101
  spacingX = 15
  spacingY = 15
FEATURE [TechDraw::DrawProjGroupItem] View024
  CoarseView = false
  Direction = (-1,-1e-16,0)
  Focus = 100
  HardHidden = false
  IsoCount = 0
  IsoHidden = false
  IsoVisible = false
  LockPosition = true
  Perspective = false
  Rotation = 0
  RotationVector = (1,0,0)
  Scale = 0.666667
  ScaleType = 2
  ScrubCount = 1
  SeamHidden = false
  SeamVisible = false
  SmoothHidden = false
  SmoothVisible = true
  Type = 0
  X = 21.9334
  XDirection = (1e-16,-1,0)
  XSource = -> [A9001]
  Y = 85.4173
FEATURE [TechDraw::DrawSVGTemplate] Template013  label="Modèle013"
  Height = 210
  Orientation = 1
  Template = C:/Program Files/FreeCAD_0.19/data/Mod/TechDraw/Templates/A4_LandscapeTDteste.svg
  Width = 297
FEATURE [TechDraw::DrawSVGTemplate] Template014  label="Modèle014"
  Height = 210
  Orientation = 1
  Template = C:/Program Files/FreeCAD_0.19/data/Mod/TechDraw/Templates/A4_LandscapeTDteste.svg
  Width = 297
FEATURE [TechDraw::DrawSVGTemplate] Template015  label="Modèle015"
  Height = 210
  Orientation = 1
  Template = C:/Program Files/FreeCAD_0.19/data/Mod/TechDraw/Templates/A4_LandscapeTDteste.svg
  Width = 297
FEATURE [TechDraw::DrawProjGroupItem] View025  label="Front009"
  CoarseView = false
  Direction = (0,-1,0)
  Focus = 100
  HardHidden = false
  IsoCount = 0
  IsoHidden = false
  IsoVisible = false
  LockPosition = true
  Perspective = false
  Rotation = 0
  RotationVector = (1,0,0)
  Scale = 0.083333
  ScaleType = 2
  ScrubCount = 1
  SeamHidden = false
  SeamVisible = false
  SmoothHidden = false
  SmoothVisible = true
  Type = 0
  X = 0
  XDirection = (-1,0,0)
  XSource = -> [A2001,A1001,A1004,A2003,A5001,A5002,A6001,A7003,A7004,A8002,A12001,A12002,A12003,A2004,A14002,A14003,A11,A11001,A10,rondelle_028,rondelle_029,A18005,A13,A18004,A15002,A15001,A14008,A15,A10006,A14004,A2005,A14001,A13001,A12,A18002,A18003]
  Y = 0
FEATURE [TechDraw::DrawProjGroupItem] ProjItem011  label="Dessus003"
  CoarseView = false
  Direction = (0,0,-1)
  Focus = 100
  HardHidden = false
  IsoCount = 0
  IsoHidden = false
  IsoVisible = false
  LockPosition = true
  Perspective = false
  Rotation = 0
  RotationVector = (1,0,0)
  ScaleType = 0
  ScrubCount = 1
  SeamHidden = false
  SeamVisible = false
  SmoothHidden = false
  SmoothVisible = true
  Type = 4
  X = 0
  XDirection = (-1,0,0)
  XSource = <same value as first occurrence — deduplicated (x3 in doc)>
  Y = -61.375
FEATURE [TechDraw::DrawProjGroup] ProjGroup009
  Anchor = -> View025
  AutoDistribute = true
  LockPosition = false
  ProjectionType = 0
  Rotation = 0
  Scale = 0.083333
  ScaleType = 2
  Views = -> [View025,ProjItem011]
  X = 112.182
  XSource = <same value as first occurrence — deduplicated (x3 in doc)>
  Y = 113.968
  spacingX = 15
  spacingY = 15
FEATURE [TechDraw::DrawViewDetail] Detail001  label="Detail zoom"
  AnchorPoint = (153.5,260.02,0)
  BaseView = -> ProjItem011
  CoarseView = false
  Direction = (0,0,-1)
  Focus = 100
  HardHidden = false
  IsoCount = 0
  IsoHidden = false
  IsoVisible = false
  LockPosition = true
  Perspective = false
  Radius = 100
  Reference = zoom
  Rotation = 0
  Scale = 0.3
  ScaleType = 2
  ScrubCount = 1
  SeamHidden = false
  SeamVisible = false
  ShowHighlight = true
  ShowMatting = true
  SmoothHidden = false
  SmoothVisible = true
  Source = -> [Sketch014]
  X = 253.249
  XDirection = (-1,0,0)
  Y = 98.4736
FEATURE [TechDraw::DrawProjGroupItem] View026  label="Front010"
  CoarseView = false
  Direction = (0,-1,0)
  Focus = 100
  HardHidden = false
  IsoCount = 0
  IsoHidden = false
  IsoVisible = false
  LockPosition = true
  Perspective = false
  Rotation = 0
  RotationVector = (1,0,0)
  Scale = 0.071429
  ScaleType = 2
  ScrubCount = 1
  SeamHidden = false
  SeamVisible = false
  SmoothHidden = false
  SmoothVisible = true
  Type = 0
  X = 0
  XDirection = (1,0,0)
  XSource = -> [rondelle_028,A18005,A13,A18004,A18003,A18002,A18001,A18,A17001,A17,A15002,A15001,A14008,A15,A10006,A10,A11001,A11,A14004,A14003,A14002,A2005,A2004,A14001,A13001,A12003,A12002,A12001,A12,A9001,A9,A8002,A7004,A7003,A6001,A5002,A5001,A2003,A4002,A4001,A3002,A3001,A1004,A1001,A2001,rondelle_029]
  Y = 0
FEATURE [TechDraw::DrawProjGroupItem] ProjItem012  label="Dessus004"
  CoarseView = false
  Direction = (0,0,1)
  Focus = 100
  HardHidden = false
  IsoCount = 0
  IsoHidden = false
  IsoVisible = false
  LockPosition = true
  Perspective = false
  Rotation = 0
  RotationVector = (1,0,0)
  Scale = 0.071429
  ScaleType = 2
  ScrubCount = 1
  SeamHidden = false
  SeamVisible = false
  SmoothHidden = false
  SmoothVisible = true
  Type = 4
  X = 0
  XDirection = (1,0,0)
  XSource = <same value as first occurrence — deduplicated (x3 in doc)>
  Y = -59.5779
FEATURE [TechDraw::DrawProjGroup] ProjGroup010
  Anchor = -> View026
  AutoDistribute = true
  LockPosition = false
  ProjectionType = 0
  Rotation = 0
  Scale = 0.071429
  ScaleType = 2
  Views = -> [View026,ProjItem012]
  X = 102.383
  XSource = <same value as first occurrence — deduplicated (x3 in doc)>
  Y = 139.056
  spacingX = 15
  spacingY = 15
FEATURE [TechDraw::DrawSVGTemplate] Template016  label="Modèle016"
  Height = 210
  Orientation = 1
  Template = C:/Program Files/FreeCAD_0.19/data/Mod/TechDraw/Templates/A4_LandscapeTDteste.svg
  Width = 297
FEATURE [TechDraw::DrawSVGTemplate] Template017  label="Modèle017"
  Height = 210
  Orientation = 1
  Template = C:/Program Files/FreeCAD_0.19/data/Mod/TechDraw/Templates/A4_LandscapeTDteste.svg
  Width = 297
FEATURE [TechDraw::DrawProjGroupItem] View027  label="Front011"
  CoarseView = false
  Direction = (-1,-1e-16,0)
  Focus = 100
  HardHidden = false
  IsoCount = 0
  IsoHidden = false
  IsoVisible = false
  LockPosition = true
  Perspective = false
  Rotation = 0
  RotationVector = (1,0,0)
  Scale = 0.166667
  ScaleType = 2
  ScrubCount = 1
  SeamHidden = false
  SeamVisible = false
  SmoothHidden = false
  SmoothVisible = true
  Type = 0
  X = 0
  XDirection = (1e-16,-1,0)
  XSource = -> [BB1004,BB1003,BB2,BB3,BB1001,BB1]
  Y = 0
FEATURE [TechDraw::DrawProjGroupItem] ProjItem013  label="Gauche005"
  CoarseView = false
  Direction = (-2e-16,1,0)
  Focus = 100
  HardHidden = false
  IsoCount = 0
  IsoHidden = false
  IsoVisible = false
  LockPosition = false
  Perspective = false
  Rotation = 0
  RotationVector = (1,0,0)
  Scale = 0.166667
  ScaleType = 2
  ScrubCount = 1
  SeamHidden = false
  SeamVisible = false
  SmoothHidden = false
  SmoothVisible = true
  Type = 1
  X = 67.9168
  XDirection = (-1,-2e-16,0)
  XSource = -> [BB1004,BB1003,BB2,BB3,BB1001,BB1]
  Y = 0
FEATURE [TechDraw::DrawProjGroup] ProjGroup011
  Anchor = -> View027
  AutoDistribute = true
  LockPosition = false
  ProjectionType = 0
  Rotation = 0
  Scale = 0.166667
  ScaleType = 2
  Views = -> [View027,ProjItem013]
  X = 67.9806
  XSource = -> [BB1004,BB1003,BB2,BB3,BB1001,BB1]
  Y = 95.379
  spacingX = 15
  spacingY = 15
FEATURE [TechDraw::DrawProjGroupItem] View028  label="Front012"
  CoarseView = false
  Direction = (0,-1,0)
  Focus = 100
  HardHidden = false
  IsoCount = 0
  IsoHidden = false
  IsoVisible = false
  LockPosition = true
  Perspective = false
  Rotation = 0
  RotationVector = (1,0,0)
  Scale = 0.066667
  ScaleType = 2
  ScrubCount = 1
  SeamHidden = false
  SeamVisible = false
  SmoothHidden = false
  SmoothVisible = true
  Type = 0
  X = 0
  XDirection = (1,0,0)
  XSource = -> [A2001,A1001,A1004,A3001,A3002,A4001,A4002,A2003,A5001,A5002,A6001,A7003,A7004,A8002,A9,A9001,A12,A12001,A12002,A12003,A13001,A14001,A2004,A2005,A14002,A14003,A14004,A11,A11001,A10,A10006,A15,A14008,A15001,A15002,A16,A16001,BB1,BB1001,BB3,BB2,BB1003,BB1004,A17,A17001,A18,A18001,A18002,A18003,A18004,A13,A18005,rondelle_028,rondelle_029]
  Y = 0
FEATURE [TechDraw::DrawProjGroupItem] ProjItem014  label="Gauche006"
  CoarseView = false
  Direction = (-1,-1e-16,0)
  Focus = 100
  HardHidden = false
  IsoCount = 0
  IsoHidden = false
  IsoVisible = false
  LockPosition = false
  Perspective = false
  Rotation = 0
  RotationVector = (1,0,0)
  ScaleType = 0
  ScrubCount = 1
  SeamHidden = false
  SeamVisible = false
  SmoothHidden = false
  SmoothVisible = true
  Type = 1
  X = 125.101
  XDirection = (1e-16,-1,0)
  XSource = <same value as first occurrence — deduplicated (x3 in doc)>
  Y = 0
FEATURE [TechDraw::DrawProjGroup] ProjGroup012
  Anchor = -> View028
  AutoDistribute = true
  LockPosition = false
  ProjectionType = 0
  Rotation = 0
  Scale = 0.066667
  ScaleType = 2
  Views = -> [View028,ProjItem014]
  X = 116.129
  XSource = <same value as first occurrence — deduplicated (x3 in doc)>
  Y = 118.399
  spacingX = 15
  spacingY = 15
FEATURE [TechDraw::DrawViewAnnotation] Annotation
  Font = osifont
  LineSpace = 100
  LockPosition = false
  MaxWidth = -1
  Rotation = 0
  ScaleType = 0
  Text = Souder les pièces du plateau  | principal de la brouette
  TextSize = 5
  TextStyle = 0
  X = 71.8354
  Y = 27.9636
FEATURE [TechDraw::DrawViewBalloon] Balloon025  label="Infobulle025"
  BubbleShape = 0
  EndType = 0
  EndTypeScale = 1
  KinkLength = 5
  LockPosition = false
  OriginX = -1051.89
  OriginY = 295.053
  Rotation = 0
  ScaleType = 0
  ShapeScale = 1
  SourceView = -> View012
  Text = A1
  TextWrapLen = -1
  X = -851.887
  Y = 495.053
FEATURE [TechDraw::DrawViewBalloon] Balloon026  label="Infobulle026"
  BubbleShape = 0
  EndType = 0
  EndTypeScale = 1
  KinkLength = 5
  LockPosition = false
  OriginX = -1144.23
  OriginY = 225.792
  Rotation = 0
  ScaleType = 0
  ShapeScale = 1
  SourceView = -> View012
  Text = A2
  TextWrapLen = -1
  X = -1314.36
  Y = 327.307
FEATURE [TechDraw::DrawViewBalloon] Balloon027  label="Infobulle027"
  BubbleShape = 0
  EndType = 0
  EndTypeScale = 1
  KinkLength = 5
  LockPosition = false
  OriginX = -1055.73
  OriginY = -97.4274
  Rotation = 0
  ScaleType = 0
  ShapeScale = 1
  SourceView = -> View012
  Text = A7
  TextWrapLen = -1
  X = -1303.59
  Y = 71.7898
FEATURE [TechDraw::DrawViewBalloon] Balloon028  label="Infobulle028"
  BubbleShape = 0
  EndType = 0
  EndTypeScale = 1
  KinkLength = 5
  LockPosition = false
  OriginX = 845.101
  OriginY = 218.096
  Rotation = 0
  ScaleType = 0
  ShapeScale = 1
  SourceView = -> View012
  Text = A8
  TextWrapLen = -1
  X = 544.881
  Y = 475.814
FEATURE [TechDraw::DrawViewDimension] Dimension029  label="Cote029"
  AngleOverride = false
  Arbitrary = false
  ArbitraryTolerances = false
  BoxCorners = (2) [(-115.5,-30.5,-1e-07),(115.5,30.5,1e-07)]
  EqualTolerance = true
  ExtensionAngle = 0
  FormatSpec = %.2w
  FormatSpecOverTolerance = %+.2w
  FormatSpecUnderTolerance = %+.2w
  Inverted = false
  LineAngle = 0
  LockPosition = false
  MeasureType = 1
  OverTolerance = 0
  References2D = -> [View012]
  Rotation = 0
  ScaleType = 0
  TheoreticalExact = false
  Type = 2
  UnderTolerance = 0
  X = 103.22
  Y = 15.6408
FEATURE [TechDraw::DrawViewDimension] Dimension030  label="Cote030"
  AngleOverride = false
  Arbitrary = false
  ArbitraryTolerances = false
  BoxCorners = (2) [(-115.5,-30.5,-1e-07),(115.5,30.5,1e-07)]
  EqualTolerance = true
  ExtensionAngle = 0
  FormatSpec = %.2w
  FormatSpecOverTolerance = %+.2w
  FormatSpecUnderTolerance = %+.2w
  Inverted = false
  LineAngle = 0
  LockPosition = false
  MeasureType = 1
  OverTolerance = 0
  References2D = -> [View012]
  Rotation = 0
  ScaleType = 0
  TheoreticalExact = false
  Type = 2
  UnderTolerance = 0
  X = 118.992
  Y = 6.22639
FEATURE [TechDraw::DrawViewDimension] Dimension031  label="Cote031"
  AngleOverride = false
  Arbitrary = false
  ArbitraryTolerances = false
  BoxCorners = (2) [(-115.5,-30.5,-1e-07),(115.5,30.5,1e-07)]
  EqualTolerance = true
  ExtensionAngle = 0
  FormatSpec = %.2w
  FormatSpecOverTolerance = %+.2w
  FormatSpecUnderTolerance = %+.2w
  Inverted = false
  LineAngle = 0
  LockPosition = false
  MeasureType = 1
  OverTolerance = 0
  References2D = -> [View012]
  Rotation = 0
  ScaleType = 0
  TheoreticalExact = false
  Type = 2
  UnderTolerance = 0
  X = 71.805
  Y = 9.71013
FEATURE [TechDraw::DrawViewDimension] Dimension032  label="Cote032"
  AngleOverride = false
  Arbitrary = false
  ArbitraryTolerances = false
  BoxCorners = (2) [(-115.5,-30.5,-1e-07),(115.5,30.5,1e-07)]
  EqualTolerance = true
  ExtensionAngle = 0
  FormatSpec = %.2w
  FormatSpecOverTolerance = %+.2w
  FormatSpecUnderTolerance = %+.2w
  Inverted = false
  LineAngle = 0
  LockPosition = false
  MeasureType = 1
  OverTolerance = 0
  References2D = -> [View012]
  Rotation = 0
  ScaleType = 0
  TheoreticalExact = false
  Type = 1
  UnderTolerance = 0
  X = 100.5
  Y = -35.8715
FEATURE [TechDraw::DrawProjGroupItem] View029
  CoarseView = false
  Direction = (0.57735,-0.57735,0.57735)
  Focus = 100
  HardHidden = false
  IsoCount = 0
  IsoHidden = false
  IsoVisible = false
  LockPosition = false
  Perspective = false
  Rotation = 0
  RotationVector = (1,0,0)
  Scale = 0.033333
  ScaleType = 2
  ScrubCount = 1
  SeamHidden = false
  SeamVisible = false
  SmoothHidden = false
  SmoothVisible = true
  Type = 0
  X = 251.521
  XDirection = (0.707107,0.707107,0)
  XSource = -> [A2001,A1001,A1004,A7003,A7004,A8002]
  Y = 176.767
FEATURE [Spreadsheet::Sheet] Spreadsheet001  label="et1"
  cells = A1='Qté; B1='Nom_de_la_piece; C1='Reference_AP; D1='Angle1; E1='Angle2; F1='percage; G1='longueur; A2=1; B2='A2; C2='Tube carré 25 x 2; G2=610; A3=2; B3='A1; C3='Tube carré 25 x 2; G3=2285; A4=2; B4='A7; C4='Tube carré 25 x 2; G4=1960; A5=1; B5='A8; C5='Tube carré 25 x 2; G5=560
FEATURE [TechDraw::DrawViewSpreadsheet] Sheet
  CellEnd = g5
  CellStart = A1
  Font = osifont
  LineWidth = 0.35
  LockPosition = false
  Rotation = 0
  ScaleType = 2
  Source = -> Spreadsheet001
  Symbol = <blob: 7494 chars omitted>
  TextSize = 14
  X = 221.98
  Y = 24.9012
FEATURE [Spreadsheet::Sheet] Spreadsheet002  label="et2"
  cells = A1='Qté; B1='Nom_de_la_piece; C1='Reference_AP; D1='Angle1; E1='Angle2; F1='percage; G1='longueur; A2=3; B2='A2; C2='Tube carré 25 x 2; G2=610
FEATURE [Spreadsheet::Sheet] Spreadsheet003  label="et3"
  cells = A1='Qté; B1='Nom_de_la_piece; C1='Reference_AP; D1='Angle1; E1='Angle2; F1='percage; G1='longueur; A2=2; B2='A5; C2='Tube carré 25 x 2; G2=258.5; A3=1; B3='A6; C3='Tube carré 25 x 2; G3=420; A4=4; B4='A12; C4='Tube carré 25 x 2; G4=400
FEATURE [Spreadsheet::Sheet] Spreadsheet004  label="et4"
  cells = A1='Qté; B1='Nom_de_la_piece; C1='Reference_AP; D1='Angle1; E1='Angle2; F1='percage; G1='longueur; A2=4; B2='A13; C2='Tube carré 25 x 2; D2=33.49; E2=56.51; G2=449.646319854351; A3=4; B3='A14; C3='Tube carré 25 x 2; D3=19.66; E3=19.66; G3=772.835249419013; A4=4; B4='A15; C4='Tube carré 25 x 2; D4=30.03; E4=59.97; G4=462; A5=2; B5='A18; C5='Tube carré 25 x 2; D5=45; E5=45; G5=142
FEATURE [Spreadsheet::Sheet] Spreadsheet005  label="et5"
  cells = A1='Qté; B1='Nom_de_la_piece; C1='Reference_AP; D1='Angle1; E1='Angle2; F1='percage; G1='longueur; A2=2; B2='A10; C2='étiré rond Ø25; F2='Ø6; G2=150; A3=2; B3='rondelle int 25; C3='rondelle int 25
FEATURE [Spreadsheet::Sheet] Spreadsheet006  label="et6"
  cells = A1='Qté; B1='Nom_de_la_piece; C1='Reference_AP; D1='Angle1; E1='Angle2; F1='percage; G1='longueur; A2=2; B2='A17; C2='Tube rond 30 x 2; G2=300; A3=2; B3='A9; C3='Tube carré 25 x 2; G3=215
FEATURE [Spreadsheet::Sheet] Spreadsheet007  label="et7"
FEATURE [Spreadsheet::Sheet] Spreadsheet008  label="et8"
  cells = A1='Qté; B1='Nom_de_la_piece; C1='Reference_AP; D1='Angle1; E1='Angle2; F1='percage; G1='longueur; A2=2; B2='A3; C2='fer rond Ø10; G2=2140; A3=2; B3='A4; C3='fer rond Ø10; G3=90; A4=2; B4='A9; C4='Tube carré 25 x 2; G4=215; A5=2; B5='A17; C5='Tube rond 30 x 2; G5=300; A6=2; B6='A18; C6='Tube carré 25 x 2; D6=45; E6=45; G6=142
FEATURE [TechDraw::DrawProjGroupItem] View030  label="Front013"
  CoarseView = false
  Direction = (0,1,0)
  Focus = 100
  HardHidden = false
  IsoCount = 0
  IsoHidden = false
  IsoVisible = false
  LockPosition = true
  Perspective = false
  Rotation = 0
  RotationVector = (1,0,0)
  Scale = 0.083333
  ScaleType = 2
  ScrubCount = 1
  SeamHidden = false
  SeamVisible = false
  SmoothHidden = false
  SmoothVisible = true
  Type = 0
  X = 0
  XDirection = (1,0,0)
  XSource = -> [A2001,A1001,A1004,A8002,A7004,A7003,A2003,A2004,A2005]
  Y = 0
FEATURE [TechDraw::DrawProjGroupItem] ProjItem015  label="Dessus005"
  CoarseView = false
  Direction = (0,0,-1)
  Focus = 100
  HardHidden = false
  IsoCount = 0
  IsoHidden = false
  IsoVisible = false
  LockPosition = true
  Perspective = false
  Rotation = 0
  RotationVector = (1,0,0)
  ScaleType = 2
  ScrubCount = 1
  SeamHidden = false
  SeamVisible = false
  SmoothHidden = false
  SmoothVisible = true
  Type = 4
  X = 0
  XDirection = (1,0,0)
  XSource = -> [A2001,A1001,A1004,A8002,A7004,A7003,A2003,A2004,A2005]
  Y = 60.7893
FEATURE [TechDraw::DrawProjGroup] ProjGroup013
  Anchor = -> View030
  AutoDistribute = true
  LockPosition = false
  ProjectionType = 0
  Rotation = 0
  Scale = 0.083333
  ScaleType = 2
  Views = -> [View030,ProjItem015]
  X = 140.798
  XSource = -> [A2001,A1001,A1004,A8002,A7004,A7003,A2003,A2004,A2005]
  Y = 58.1595
  spacingX = 15
  spacingY = 15
FEATURE [TechDraw::DrawProjGroupItem] View031
  CoarseView = false
  Direction = (0.2,0.6,-0.75)
  Focus = 100
  HardHidden = false
  IsoCount = 0
  IsoHidden = false
  IsoVisible = false
  LockPosition = true
  Perspective = false
  Rotation = 0
  RotationVector = (1,0,0)
  Scale = 0.033333
  ScaleType = 2
  ScrubCount = 1
  SeamHidden = false
  SeamVisible = false
  SmoothHidden = false
  SmoothVisible = true
  Type = 0
  X = 252.938
  XDirection = (0.806962,-0.532503,-0.255446)
  XSource = -> [A2001,A1001,A1004,A2003,A7003,A7004,A8002,A2004,A2005]
  Y = 173.425
FEATURE [TechDraw::DrawViewBalloon] Balloon029  label="Infobulle029"
  BubbleShape = 0
  EndType = 0
  EndTypeScale = 1
  KinkLength = 5
  LockPosition = false
  OriginX = -890.785
  OriginY = 164.882
  Rotation = 0
  ScaleType = 2
  ShapeScale = 1
  SourceView = -> ProjItem015
  Text = A2
  TextWrapLen = -1
  X = -440.655
  Y = 410.886
FEATURE [TechDraw::DrawGeomHatch] GeomHatch006  label="Hachures géométriques006"
  FilePattern = <userpath>\Desktop\bureau\FreeCAD_1.0.0-conda-Windows-x86_64-py311\data\Mod/TechDraw/PAT/FCPAT.pat
  NamePattern = Diamond2
  PatternOffset = (0,0,0)
  PatternRotation = 0
  ScalePattern = 1
  Source = -> ProjItem015 [Face22,Face23,Face21]
FEATURE [TechDraw::DrawViewSpreadsheet] Sheet001
  CellEnd = g2
  CellStart = A1
  Font = osifont
  LineWidth = 0.35
  LockPosition = false
  Rotation = 0
  ScaleType = 2
  Source = -> Spreadsheet002
  Symbol = <blob: 3242 chars omitted>
  TextSize = 14
  X = 225.788
  Y = 13.7178
FEATURE [TechDraw::DrawViewDimension] Dimension033  label="Cote033"
  AngleOverride = false
  Arbitrary = false
  ArbitraryTolerances = false
  BoxCorners = (2) [(-96.2496,-25.4166,-1e-07),(96.2496,25.4166,1e-07)]
  EqualTolerance = true
  ExtensionAngle = 0
  FormatSpec = %.0w
  FormatSpecOverTolerance = %+.2w
  FormatSpecUnderTolerance = %+.2w
  Inverted = false
  LineAngle = 0
  LockPosition = false
  MeasureType = 1
  OverTolerance = 0
  References2D = -> [ProjItem015]
  Rotation = 0
  ScaleType = 2
  TheoreticalExact = false
  Type = 1
  UnderTolerance = 0
  X = -85.9119
  Y = -32.0237
FEATURE [TechDraw::DrawViewDimension] Dimension034  label="Cote034"
  AngleOverride = false
  Arbitrary = false
  ArbitraryTolerances = false
  BoxCorners = (2) [(-96.2496,-25.4166,-1e-07),(96.2496,25.4166,1e-07)]
  EqualTolerance = true
  ExtensionAngle = 0
  FormatSpec = %.2w
  FormatSpecOverTolerance = %+.2w
  FormatSpecUnderTolerance = %+.2w
  Inverted = false
  LineAngle = 0
  LockPosition = false
  MeasureType = 1
  OverTolerance = 0
  References2D = -> [ProjItem015]
  Rotation = 0
  ScaleType = 2
  TheoreticalExact = false
  Type = 1
  UnderTolerance = 0
  X = -42.0672
  Y = -34.7367
FEATURE [TechDraw::DrawViewDimension] Dimension035  label="Cote035"
  AngleOverride = false
  Arbitrary = false
  ArbitraryTolerances = false
  BoxCorners = (2) [(-96.2496,-25.4166,-1e-07),(96.2496,25.4166,1e-07)]
  EqualTolerance = true
  ExtensionAngle = 0
  FormatSpec = %.0w
  FormatSpecOverTolerance = %+.2w
  FormatSpecUnderTolerance = %+.2w
  Inverted = false
  LineAngle = 0
  LockPosition = false
  MeasureType = 1
  OverTolerance = 0
  References2D = -> [ProjItem015]
  Rotation = 0
  ScaleType = 2
  TheoreticalExact = false
  Type = 1
  UnderTolerance = 0
  X = 15.9558
  Y = -36.4032
FEATURE [TechDraw::DrawViewAnnotation] Annotation007
  Font = osifont
  LineSpace = 100
  LockPosition = false
  MaxWidth = -1
  Rotation = 0
  ScaleType = 2
  Text = brouette à l'envers | souder les 3 A2 restantes
  TextSize = 5
  TextStyle = 0
  X = 75.9557
  Y = 22.9499
FEATURE [TechDraw::DrawGeomHatch] GeomHatch007  label="Hachures géométriques007"
  FilePattern = <userpath>\Desktop\bureau\FreeCAD_1.0.0-conda-Windows-x86_64-py311\data\Mod/TechDraw/PAT/FCPAT.pat
  NamePattern = Diamond2
  PatternOffset = (0,0,0)
  PatternRotation = 0
  ScalePattern = 1
  Source = -> View030 [Face11,Face8,Face10]
FEATURE [TechDraw::DrawProjGroupItem] View032
  CoarseView = false
  Direction = (0.192436,0.645981,-0.738699)
  Focus = 100
  HardHidden = false
  IsoCount = 0
  IsoHidden = false
  IsoVisible = false
  LockPosition = true
  Perspective = false
  Rotation = 0
  RotationVector = (1,0,0)
  Scale = 0.033333
  ScaleType = 2
  ScrubCount = 1
  SeamHidden = false
  SeamVisible = false
  SmoothHidden = false
  SmoothVisible = true
  Type = 0
  X = 249.982
  XDirection = (0.806962,-0.532503,-0.255446)
  XSource = -> [A2001,A1001,A1004,A2003,A5001,A5002,A6001,A7003,A7004,A8002,A2004,A2005,A12001,A12002,A12,A12003]
  Y = 168.426
FEATURE [TechDraw::DrawViewDimension] Dimension036  label="Cote036"
  AngleOverride = false
  Arbitrary = false
  ArbitraryTolerances = false
  BoxCorners = (2) [(-96.2496,-17.7083,-1e-07),(96.2496,17.7083,1e-07)]
  EqualTolerance = true
  ExtensionAngle = 0
  FormatSpec = %.2w
  FormatSpecOverTolerance = %+.2w
  FormatSpecUnderTolerance = %+.2w
  Inverted = false
  LineAngle = 0
  LockPosition = false
  MeasureType = 1
  OverTolerance = 0
  References2D = -> [View016]
  Rotation = 0
  ScaleType = 2
  TheoreticalExact = false
  Type = 1
  UnderTolerance = 0
  X = -83.7497
  Y = -7.49662
FEATURE [TechDraw::DrawViewDimension] Dimension037  label="Cote037"
  AngleOverride = false
  Arbitrary = false
  ArbitraryTolerances = false
  BoxCorners = (2) [(-25.4166,-17.7083,-1e-07),(25.4166,17.7083,1e-07)]
  EqualTolerance = true
  ExtensionAngle = 0
  FormatSpec = %.2w
  FormatSpecOverTolerance = %+.2w
  FormatSpecUnderTolerance = %+.2w
  Inverted = false
  LineAngle = 0
  LockPosition = false
  MeasureType = 1
  OverTolerance = 0
  References2D = -> [ProjItem009]
  Rotation = 0
  ScaleType = 2
  TheoreticalExact = false
  Type = 1
  UnderTolerance = 0
  X = -28.8338
  Y = -24.0081
FEATURE [TechDraw::DrawViewBalloon] Balloon030  label="Infobulle030"
  BubbleShape = 0
  EndType = 0
  EndTypeScale = 1
  KinkLength = 5
  LockPosition = false
  OriginX = -842.848
  OriginY = -56.7673
  Rotation = 0
  ScaleType = 2
  ShapeScale = 1
  SourceView = -> View016
  Text = A12
  TextWrapLen = -1
  X = -574.477
  Y = 110.573
FEATURE [TechDraw::DrawViewBalloon] Balloon031  label="Infobulle031"
  BubbleShape = 0
  EndType = 0
  EndTypeScale = 1
  KinkLength = 5
  LockPosition = false
  OriginX = 150.777
  OriginY = -23.7153
  Rotation = 0
  ScaleType = 2
  ShapeScale = 1
  SourceView = -> View016
  Text = A5
  TextWrapLen = -1
  X = 439.303
  Y = -23.3812
FEATURE [TechDraw::DrawViewBalloon] Balloon032  label="Infobulle032"
  BubbleShape = 0
  EndType = 0
  EndTypeScale = 1
  KinkLength = 5
  LockPosition = false
  OriginX = -222.92
  OriginY = -98.0822
  Rotation = 0
  ScaleType = 2
  ShapeScale = 1
  SourceView = -> ProjItem009
  Text = A5
  TextWrapLen = -1
  X = 10.8839
  Y = -73.6255
FEATURE [TechDraw::DrawViewBalloon] Balloon033  label="Infobulle033"
  BubbleShape = 0
  EndType = 0
  EndTypeScale = 1
  KinkLength = 5
  LockPosition = false
  OriginX = -30.8053
  OriginY = 81.6379
  Rotation = 0
  ScaleType = 2
  ShapeScale = 1
  SourceView = -> ProjItem009
  Text = A6
  TextWrapLen = -1
  X = 164.064
  Y = 193.117
FEATURE [TechDraw::DrawViewBalloon] Balloon034  label="Infobulle034"
  BubbleShape = 0
  EndType = 0
  EndTypeScale = 1
  KinkLength = 5
  LockPosition = false
  OriginX = -219.004
  OriginY = 102.147
  Rotation = 0
  ScaleType = 2
  ShapeScale = 1
  SourceView = -> ProjItem009
  Text = A11
  TextWrapLen = -1
  X = -86.4759
  Y = 226.714
FEATURE [TechDraw::DrawViewBalloon] Balloon035  label="Infobulle035"
  BubbleShape = 0
  EndType = 0
  EndTypeScale = 1
  KinkLength = 5
  LockPosition = false
  OriginX = 137.254
  OriginY = 105.093
  Rotation = 0
  ScaleType = 2
  ShapeScale = 1
  SourceView = -> View016
  Text = A11
  TextWrapLen = -1
  X = -137.995
  Y = 112.182
FEATURE [TechDraw::DrawViewSpreadsheet] Sheet002
  CellEnd = g4
  CellStart = A1
  Font = osifont
  LineWidth = 0.35
  LockPosition = false
  Rotation = 0
  ScaleType = 2
  Source = -> Spreadsheet003
  Symbol = <blob: 6071 chars omitted>
  TextSize = 14
  X = 224.349
  Y = 20.6604
FEATURE [TechDraw::DrawViewAnnotation] Annotation008
  Font = osifont
  LineSpace = 100
  LockPosition = false
  MaxWidth = -1
  Rotation = 0
  ScaleType = 2
  Text = brouette à l'envers | souder les 4 pieds (A12) | souder la structure support pour les axes de roue ( A5 - A6 - A11 )
  TextSize = 5
  TextStyle = 0
  X = 141.395
  Y = 131.756
FEATURE [TechDraw::DrawViewAnnotation] Annotation009
  Font = osifont
  LineSpace = 100
  LockPosition = false
  MaxWidth = -1
  Rotation = 0
  ScaleType = 2
  Text = Prennez soin à ce que tous soit bien perpendiculaire | aidez vous de l'equerre pour pointer | et vérifié les diagonales, avant de souder | un réajustement pourra avoir lieu au moment | du pointage des renforts
  TextSize = 5
  TextStyle = 0
  X = 89.4317
  Y = 34.3616
FEATURE [TechDraw::DrawViewBalloon] Balloon036  label="Infobulle036"
  BubbleShape = 0
  EndType = 0
  EndTypeScale = 1
  KinkLength = 5
  LockPosition = false
  OriginX = -723.778
  OriginY = 25.2318
  Rotation = 0
  ScaleType = 2
  ShapeScale = 1
  SourceView = -> View015
  Text = A13
  TextWrapLen = -1
  X = -425.962
  Y = 122.391
FEATURE [TechDraw::DrawViewBalloon] Balloon037  label="Infobulle037"
  BubbleShape = 0
  EndType = 0
  EndTypeScale = 1
  KinkLength = 5
  LockPosition = false
  OriginX = 370.222
  OriginY = 1.78897
  Rotation = 0
  ScaleType = 2
  ShapeScale = 1
  SourceView = -> View015
  Text = A14
  TextWrapLen = -1
  X = 708.85
  Y = 122.755
FEATURE [TechDraw::DrawViewBalloon] Balloon038  label="Infobulle038"
  BubbleShape = 0
  EndType = 0
  EndTypeScale = 1
  KinkLength = 5
  LockPosition = false
  OriginX = -898.948
  OriginY = -146.393
  Rotation = 0
  ScaleType = 2
  ShapeScale = 1
  SourceView = -> View015
  Text = A18
  TextWrapLen = -1
  X = -1083.51
  Y = 109.698
FEATURE [TechDraw::DrawViewBalloon] Balloon039  label="Infobulle039"
  BubbleShape = 0
  EndType = 0
  EndTypeScale = 1
  KinkLength = 5
  LockPosition = false
  OriginX = -176.747
  OriginY = 3.39399
  Rotation = 0
  ScaleType = 2
  ShapeScale = 1
  SourceView = -> ProjItem008
  Text = A15
  TextWrapLen = -1
  X = 63.2526
  Y = 178.775
FEATURE [TechDraw::DrawProjGroupItem] View033
  CoarseView = false
  Direction = (0.192436,0.645981,-0.738699)
  Focus = 100
  HardHidden = false
  IsoCount = 0
  IsoHidden = false
  IsoVisible = false
  LockPosition = false
  Perspective = false
  Rotation = 0
  RotationVector = (1,0,0)
  Scale = 0.033333
  ScaleType = 2
  ScrubCount = 1
  SeamHidden = false
  SeamVisible = false
  SmoothHidden = false
  SmoothVisible = true
  Type = 0
  X = 253.635
  XDirection = (0.806962,-0.532503,-0.255446)
  XSource = -> [A2001,A1001,A1004,A5001,A5002,A6001,A7003,A7004,A8002,A12,A12001,A12003,A12002,A13001,A14001,A2004,A2005,A14002,A14003,A14004,A11,A11001,A15,A14008,A15001,A15002,A18002,A18003,A18004,A13,A18005]
  Y = 170.982
FEATURE [TechDraw::DrawViewAnnotation] Annotation010
  Font = osifont
  LineSpace = 100
  LockPosition = false
  MaxWidth = -1
  Rotation = 0
  ScaleType = 2
  Text = placer les renforts des pièces installées | à l'étape précédente
  TextSize = 5
  TextStyle = 0
  X = 80.5106
  Y = 31.4076
FEATURE [TechDraw::DrawViewSpreadsheet] Sheet003
  CellEnd = g5
  CellStart = A1
  Font = osifont
  LineWidth = 0.35
  LockPosition = false
  Rotation = 0
  ScaleType = 2
  Source = -> Spreadsheet004
  Symbol = <blob: 7530 chars omitted>
  TextSize = 14
  X = 226.55
  Y = 24.7361
FEATURE [TechDraw::DrawViewAnnotation] Annotation011
  Font = osifont
  LineSpace = 100
  LockPosition = false
  MaxWidth = -1
  Rotation = 0
  ScaleType = 2
  Text = sur établi préparer les 2 axes pour les roues. Des cotes théorique vous sont donnés  | mais afin de vous assurer de la justesse du montage il vous est conseillé la manière suivante : | sur l'axe A10 installer la goupille puis une rondelle de 25 , la roue | et enfin la dernière rondelle de 25. c'est celle-ci qui devra être souder  | faire une marque sur la position de cette dernière , défaire le montage | puis repositionner la rondelle afin de la souder
  TextSize = 5
  TextStyle = 0
  X = 149.019
  Y = 134.16
FEATURE [TechDraw::DrawViewDimension] Dimension038  label="Cote038"
  AngleOverride = false
  Arbitrary = false
  ArbitraryTolerances = false
  BoxCorners = (2) [(-18.6667,-50,-1e-07),(18.6667,50,1e-07)]
  EqualTolerance = true
  ExtensionAngle = 0
  FormatSpec = %.2w
  FormatSpecOverTolerance = %+.2w
  FormatSpecUnderTolerance = %+.2w
  Inverted = false
  LineAngle = 0
  LockPosition = false
  MeasureType = 1
  OverTolerance = 0
  References2D = -> [View022]
  Rotation = 0
  ScaleType = 2
  TheoreticalExact = false
  Type = 2
  UnderTolerance = 0
  X = 13.1381
  Y = 33
FEATURE [TechDraw::DrawViewAnnotation] Annotation012
  Font = osifont
  LineSpace = 100
  LockPosition = false
  MaxWidth = -1
  Rotation = 0
  ScaleType = 2
  Text = Etre attentif à la perpendicularité  | de la rondelle par rapport à l'axe
  TextSize = 5
  TextStyle = 0
  X = 190.42
  Y = 53.424
FEATURE [TechDraw::DrawViewBalloon] Balloon040  label="Infobulle040"
  BubbleShape = 0
  EndType = 0
  EndTypeScale = 1
  KinkLength = 5
  LockPosition = false
  OriginX = -6.69559
  OriginY = 21.6683
  Rotation = 0
  ScaleType = 2
  ShapeScale = 1
  SourceView = -> View022
  TextWrapLen = -1
  X = -32.1717
  Y = -35.3139
FEATURE [TechDraw::DrawViewSpreadsheet] Sheet004
  CellEnd = g3
  CellStart = A1
  Font = osifont
  LineWidth = 0.35
  LockPosition = false
  Rotation = 0
  ScaleType = 2
  Source = -> Spreadsheet005
  Symbol = <blob: 4657 chars omitted>
  TextSize = 12
  X = 169.415
  Y = 17.1768
FEATURE [TechDraw::DrawViewSpreadsheet] Sheet005
  CellEnd = g3
  CellStart = A1
  Font = osifont
  LineWidth = 0.35
  LockPosition = false
  Rotation = 0
  ScaleType = 2
  Source = -> Spreadsheet006
  Symbol = <blob: 4649 chars omitted>
  TextSize = 14
  X = 136.574
  Y = 16.8519
FEATURE [TechDraw::DrawViewBalloon] Balloon042  label="Infobulle042"
  BubbleShape = 0
  EndType = 0
  EndTypeScale = 1
  KinkLength = 5
  LockPosition = false
  OriginX = -68.7995
  OriginY = 100.346
  Rotation = 0
  ScaleType = 2
  ShapeScale = 1
  SourceView = -> View023
  Text = A11
  TextWrapLen = -1
  X = -194.024
  Y = 1.61834
FEATURE [TechDraw::DrawViewDetail] Detail002  label="Detail gueule de loup"
  AnchorPoint = (0,105,0)
  BaseView = -> View024
  CoarseView = false
  Direction = (-1,-1e-16,0)
  Focus = 100
  HardHidden = false
  IsoCount = 0
  IsoHidden = false
  IsoVisible = false
  LockPosition = false
  Perspective = false
  Radius = 18
  Reference = gueule de loup
  Rotation = 0
  ScaleType = 2
  ScrubCount = 1
  SeamHidden = false
  SeamVisible = false
  ShowHighlight = true
  ShowMatting = true
  SmoothHidden = false
  SmoothVisible = true
  X = 54.7006
  XDirection = (1e-16,-1,0)
  Y = 134.677
FEATURE [TechDraw::DrawViewAnnotation] Annotation013
  Font = osifont
  LineSpace = 100
  LockPosition = false
  MaxWidth = -1
  Rotation = 0
  ScaleType = 2
  Text = Effectuer une gueule de loup sur la pièce A9 | vous pouvez vous aidez en découpant le détail  | de celle-ci ci-dessus à gauche. | Il est à l'échelle 1 et devrait faire 25 mm
  TextSize = 5
  TextStyle = 0
  X = 136.574
  Y = 76.3832
FEATURE [TechDraw::DrawViewAnnotation] Annotation014
  Font = osifont
  LineSpace = 100
  LockPosition = false
  MaxWidth = -1
  Rotation = 0
  ScaleType = 2
  Text = puis souder A9 et A11
  TextSize = 5
  TextStyle = 0
  X = 235.41
  Y = 126.198
FEATURE [TechDraw::DrawViewDimension] Dimension039  label="Cote039"
  AngleOverride = false
  Arbitrary = false
  ArbitraryTolerances = false
  BoxCorners = (2) [(-12.5,-2.5,0),(12.5,18.18,0)]
  EqualTolerance = true
  ExtensionAngle = 0
  FormatSpec = %.2w
  FormatSpecOverTolerance = %+.2w
  FormatSpecUnderTolerance = %+.2w
  Inverted = false
  LineAngle = 0
  LockPosition = false
  MeasureType = 1
  OverTolerance = 0
  References2D = -> [Detail002]
  Rotation = 0
  ScaleType = 2
  TheoreticalExact = false
  Type = 1
  UnderTolerance = 0
  X = 0
  Y = -23.0868
FEATURE [TechDraw::DrawViewBalloon] Balloon043  label="Infobulle043"
  BubbleShape = 0
  EndType = 0
  EndTypeScale = 1
  KinkLength = 5
  LockPosition = false
  OriginX = -0.308786
  OriginY = -75.6618
  Rotation = 0
  ScaleType = 2
  ShapeScale = 1
  SourceView = -> View024
  Text = A9
  TextWrapLen = -1
  X = 43.9996
  Y = -15.4553
FEATURE [TechDraw::DrawGeomHatch] GeomHatch008  label="Hachures géométriques008"
  FilePattern = <userpath>\Desktop\bureau\FreeCAD_1.0.0-conda-Windows-x86_64-py311\data\Mod/TechDraw/PAT/FCPAT.pat
  NamePattern = Diamond2
  PatternOffset = (0,0,0)
  PatternRotation = 0
  ScalePattern = 1
  Source = -> ProjItem011 [Face46,Face79]
FEATURE [TechDraw::DrawGeomHatch] GeomHatch009  label="Hachures géométriques009"
  FilePattern = <userpath>\Desktop\bureau\FreeCAD_1.0.0-conda-Windows-x86_64-py311\data\Mod/TechDraw/PAT/FCPAT.pat
  NamePattern = Diamond2
  PatternOffset = (0,0,0)
  PatternRotation = 0
  ScalePattern = 1
  Source = -> Detail001 [Face1,Face6]
FEATURE [TechDraw::DrawGeomHatch] GeomHatch010  label="Hachures géométriques010"
  FilePattern = <userpath>\Desktop\bureau\FreeCAD_1.0.0-conda-Windows-x86_64-py311\data\Mod/TechDraw/PAT/FCPAT.pat
  NamePattern = Diamond2
  PatternOffset = (0,0,0)
  PatternRotation = 0
  ScalePattern = 1
  Source = -> View025 [Face36]
FEATURE [TechDraw::DrawViewBalloon] Balloon044  label="Infobulle044"
  BubbleShape = 3
  EndType = 0
  EndTypeScale = 1
  KinkLength = 5
  LockPosition = false
  OriginX = 149.259
  OriginY = -270.658
  Rotation = 0
  ScaleType = 2
  ShapeScale = 1
  SourceView = -> ProjItem011
  Text = Axe de roue
  TextWrapLen = -1
  X = 642.381
  Y = -390.296
FEATURE [TechDraw::DrawViewDimension] Dimension040  label="Cote040"
  AngleOverride = false
  Arbitrary = false
  ArbitraryTolerances = false
  BoxCorners = (2) [(-29.7012,-25.194,-1e-07),(29.7012,30.3,1e-07)]
  EqualTolerance = true
  ExtensionAngle = 0
  FormatSpec = %.2w
  FormatSpecOverTolerance = %+.2w
  FormatSpecUnderTolerance = %+.2w
  Inverted = false
  LineAngle = 0
  LockPosition = false
  MeasureType = 1
  OverTolerance = 0
  References2D = -> [Detail001]
  Rotation = 0
  ScaleType = 2
  TheoreticalExact = false
  Type = 2
  UnderTolerance = 0
  X = 12.0944
  Y = -26.356
FEATURE [TechDraw::DrawProjGroupItem] View034
  CoarseView = false
  Direction = (0.192436,0.645981,-0.738699)
  Focus = 100
  HardHidden = false
  IsoCount = 0
  IsoHidden = false
  IsoVisible = false
  LockPosition = true
  Perspective = false
  Rotation = 0
  RotationVector = (1,0,0)
  Scale = 0.033333
  ScaleType = 2
  ScrubCount = 1
  SeamHidden = false
  SeamVisible = false
  SmoothHidden = false
  SmoothVisible = true
  Type = 0
  X = 253.249
  XDirection = (0.806962,-0.532503,-0.255446)
  XSource = -> [A2001,A1001,A1004,A2003,A5001,A5002,A6001,A7003,A7004,A12,A12001,A12002,A12003,A13001,A14001,A2004,A2005,A14002,A14003,A14004,A11,A11001,A10,A10006,A15,A14008,A18002,A18003,A18004,A13,rondelle_028,rondelle_029,A18005,A8002,A15001,A15002]
  Y = 170.126
FEATURE [TechDraw::DrawViewAnnotation] Annotation015
  Font = osifont
  LineSpace = 100
  LockPosition = false
  MaxWidth = -1
  Rotation = 0
  ScaleType = 2
  Text = souder les 2 axes de roue préparés précédement | sur les UPN A10
  TextSize = 5
  TextStyle = 0
  X = 112.772
  Y = 149.481
FEATURE [TechDraw::DrawViewAnnotation] Annotation016
  Font = osifont
  LineSpace = 100
  LockPosition = false
  MaxWidth = -1
  Rotation = 0
  ScaleType = 2
  Text = Respecter un espacement  | de 10 mm entre  | le bout de la pièce A10 | et la rondelle
  TextSize = 5
  TextStyle = 0
  X = 253.249
  Y = 36.9014
FEATURE [TechDraw::DrawGeomHatch] GeomHatch011  label="Hachures géométriques011"
  FilePattern = <userpath>\Desktop\bureau\FreeCAD_1.0.0-conda-Windows-x86_64-py311\data\Mod/TechDraw/PAT/FCPAT.pat
  NamePattern = Diamond2
  PatternOffset = (0,0,0)
  PatternRotation = 0
  ScalePattern = 1
  Source = -> View026 [Face11,Face18,Face25]
FEATURE [TechDraw::DrawGeomHatch] GeomHatch013  label="Hachures géométriques013"
  FilePattern = <userpath>\Desktop\bureau\FreeCAD_1.0.0-conda-Windows-x86_64-py311\data\Mod/TechDraw/PAT/FCPAT.pat
  NamePattern = Diamond2
  PatternOffset = (0,0,0)
  PatternRotation = 0
  ScalePattern = 1
  Source = -> ProjItem012 [Face31,Face50,Face51,Face32]
FEATURE [TechDraw::DrawViewSpreadsheet] Sheet006
  CellEnd = g6
  CellStart = A1
  Font = osifont
  LineWidth = 0.35
  LockPosition = false
  Rotation = 0
  ScaleType = 2
  Source = -> Spreadsheet008
  Symbol = <blob: 8916 chars omitted>
  TextSize = 12
  X = 224.321
  Y = 29.1789
FEATURE [TechDraw::DrawProjGroupItem] View035
  CoarseView = false
  Direction = (0.57735,-0.57735,0.57735)
  Focus = 100
  HardHidden = false
  IsoCount = 0
  IsoHidden = false
  IsoVisible = false
  LockPosition = false
  Perspective = false
  Rotation = 0
  RotationVector = (1,0,0)
  Scale = 0.0333333
  ScaleType = 2
  ScrubCount = 1
  SeamHidden = false
  SeamVisible = false
  SmoothHidden = false
  SmoothVisible = true
  Type = 0
  X = 250.945
  XDirection = (0.707107,0.707107,0)
  XSource = -> [A2001,A1001,A1004,A3001,A3002,A4001,A4002,A2003,A5001,A5002,A6001,A7003,A7004,A8002,A9,A9001,A12,A12001,A12002,A12003,A13001,A14001,A2004,A2005,A14002,A14003,A14004,A11,A11001,A10,A10006,A15,A14008,A15001,A15002,A17,A17001,A18,A18001,A18002,A18003,A18004,A13,A18005,rondelle_028,rondelle_029]
  Y = 177.927
FEATURE [TechDraw::DrawViewBalloon] Balloon045  label="Infobulle045"
  BubbleShape = 0
  EndType = 0
  EndTypeScale = 1
  KinkLength = 5
  LockPosition = false
  OriginX = 1127.98
  OriginY = 311.888
  Rotation = 0
  ScaleType = 2
  ShapeScale = 1
  SourceView = -> View026
  Text = A17
  TextWrapLen = -1
  X = 949.796
  Y = 570.068
FEATURE [TechDraw::DrawViewBalloon] Balloon046  label="Infobulle046"
  BubbleShape = 0
  EndType = 0
  EndTypeScale = 1
  KinkLength = 5
  LockPosition = false
  OriginX = 1002.07
  OriginY = 198.601
  Rotation = 0
  ScaleType = 2
  ShapeScale = 1
  SourceView = -> View026
  Text = A9
  TextWrapLen = -1
  X = 1232.98
  Y = 118.6
FEATURE [TechDraw::DrawViewBalloon] Balloon047  label="Infobulle047"
  BubbleShape = 0
  EndType = 0
  EndTypeScale = 1
  KinkLength = 5
  LockPosition = false
  OriginX = 945.607
  OriginY = 129.352
  Rotation = 0
  ScaleType = 2
  ShapeScale = 1
  SourceView = -> View026
  Text = A18
  TextWrapLen = -1
  X = 816.515
  Y = -108.831
FEATURE [TechDraw::DrawViewBalloon] Balloon049  label="Infobulle049"
  BubbleShape = 0
  EndType = 0
  EndTypeScale = 1
  KinkLength = 5
  LockPosition = false
  OriginX = -282.5
  OriginY = 113.357
  Rotation = 0
  ScaleType = 2
  ShapeScale = 1
  SourceView = -> View026
  Text = A4
  TextWrapLen = -1
  X = -51.5926
  Y = -15.7361
FEATURE [TechDraw::DrawViewBalloon] Balloon050  label="Infobulle050"
  BubbleShape = 0
  EndType = 0
  EndTypeScale = 1
  KinkLength = 5
  LockPosition = false
  OriginX = -757.5
  OriginY = 158.357
  Rotation = 0
  ScaleType = 2
  ShapeScale = 1
  SourceView = -> View026
  Text = A3
  TextWrapLen = -1
  X = -493.865
  Y = -19.827
FEATURE [TechDraw::DrawViewAnnotation] Annotation017
  Font = osifont
  LineSpace = 100
  LockPosition = false
  MaxWidth = -1
  Rotation = 0
  ScaleType = 2
  Text = Souder les poignets  | précédement construitent  | ainsi que leurs renforts
  TextSize = 5
  TextStyle = 0
  X = 244.345
  Y = 108.117
FEATURE [TechDraw::DrawViewDimension] Dimension042  label="Cote042"
  AngleOverride = false
  Arbitrary = false
  ArbitraryTolerances = false
  BoxCorners = (2) [(-92.322,-23.6893,-1e-07),(92.322,23.6893,1e-07)]
  EqualTolerance = true
  ExtensionAngle = 0
  FormatSpec = %.2w
  FormatSpecOverTolerance = %+.2w
  FormatSpecUnderTolerance = %+.2w
  Inverted = false
  LineAngle = 0
  LockPosition = false
  MeasureType = 1
  OverTolerance = 0
  References2D = -> [View026]
  Rotation = 0
  ScaleType = 2
  TheoreticalExact = false
  Type = 1
  UnderTolerance = 0
  X = -20.5358
  Y = 26.1577
FEATURE [TechDraw::DrawViewDimension] Dimension043  label="Cote043"
  AngleOverride = false
  Arbitrary = false
  ArbitraryTolerances = false
  BoxCorners = (2) [(-92.322,-23.6893,-1e-07),(92.322,23.6893,1e-07)]
  EqualTolerance = true
  ExtensionAngle = 0
  FormatSpec = %.2w
  FormatSpecOverTolerance = %+.2w
  FormatSpecUnderTolerance = %+.2w
  Inverted = false
  LineAngle = 0
  LockPosition = false
  MeasureType = 1
  OverTolerance = 0
  References2D = -> [View026]
  Rotation = 0
  ScaleType = 2
  TheoreticalExact = false
  Type = 1
  UnderTolerance = 0
  X = -20.5358
  Y = 19.1577
FEATURE [TechDraw::DrawViewAnnotation] Annotation018
  Font = osifont
  LineSpace = 100
  LockPosition = false
  MaxWidth = -1
  Rotation = 0
  ScaleType = 2
  Text = tordre A3 puis souder A3 et A4 | sur les paroies exterieur de la brouette
  TextSize = 5
  TextStyle = 0
  X = 80.9796
  Y = 29.1789
FEATURE [TechDraw::DrawProjGroupItem] View036
  CoarseView = false
  Direction = (0.57735,-0.57735,0.57735)
  Focus = 100
  HardHidden = false
  IsoCount = 0
  IsoHidden = false
  IsoVisible = false
  LockPosition = false
  Perspective = false
  Rotation = 0
  RotationVector = (1,0,0)
  Scale = 0.05
  ScaleType = 2
  ScrubCount = 1
  SeamHidden = false
  SeamVisible = false
  SmoothHidden = false
  SmoothVisible = true
  Type = 0
  X = 236.327
  XDirection = (0.707107,0.707107,0)
  XSource = -> [BB1,BB1001,BB3,BB2,BB1003,BB1004]
  Y = 181.542
FEATURE [TechDraw::DrawViewBalloon] Balloon051  label="Infobulle051"
  BubbleShape = 0
  EndType = 0
  EndTypeScale = 1
  KinkLength = 5
  LockPosition = false
  OriginX = -291.422
  OriginY = -60.9952
  Rotation = 0
  ScaleType = 2
  ShapeScale = 1
  SourceView = -> View027
  Text = A1
  TextWrapLen = -1
  X = -191.422
  Y = 39.0048
FEATURE [TechDraw::DrawViewBalloon] Balloon052  label="Infobulle052"
  BubbleShape = 0
  EndType = 0
  EndTypeScale = 1
  KinkLength = 5
  LockPosition = false
  OriginX = -97.6134
  OriginY = -46.2756
  Rotation = 0
  ScaleType = 2
  ShapeScale = 1
  SourceView = -> View027
  Text = A2
  TextWrapLen = -1
  X = 2.38663
  Y = 53.7244
FEATURE [TechDraw::DrawViewDimension] Dimension044  label="Cote044"
  AngleOverride = false
  Arbitrary = false
  ArbitraryTolerances = false
  BoxCorners = (2) [(-50.8334,-57.0834,-1e-07),(50.8334,57.0834,1e-07)]
  EqualTolerance = true
  ExtensionAngle = 0
  FormatSpec = %.2w
  FormatSpecOverTolerance = %+.2w
  FormatSpecUnderTolerance = %+.2w
  Inverted = false
  LineAngle = 0
  LockPosition = false
  MeasureType = 1
  OverTolerance = 0
  References2D = -> [View027]
  Rotation = 0
  ScaleType = 2
  TheoreticalExact = false
  Type = 1
  UnderTolerance = 0
  X = -32.5001
  Y = -59.0614
FEATURE [TechDraw::DrawViewDimension] Dimension045  label="Cote045"
  AngleOverride = false
  Arbitrary = false
  ArbitraryTolerances = false
  BoxCorners = (2) [(-61,-68.5,-1e-07),(61,68.5,1e-07)]
  EqualTolerance = true
  ExtensionAngle = 0
  FormatSpec = %.2w
  FormatSpecOverTolerance = %+.2w
  FormatSpecUnderTolerance = %+.2w
  Inverted = false
  LineAngle = 0
  LockPosition = false
  MeasureType = 1
  OverTolerance = 0
  References2D = -> [View027]
  Rotation = 0
  ScaleType = 2
  TheoreticalExact = false
  Type = 1
  UnderTolerance = 0
  X = 0
  Y = -59.0614
FEATURE [TechDraw::DrawViewDimension] Dimension046  label="Cote046"
  AngleOverride = false
  Arbitrary = false
  ArbitraryTolerances = false
  BoxCorners = (2) [(-50.8334,-57.0834,-1e-07),(50.8334,57.0834,1e-07)]
  EqualTolerance = true
  ExtensionAngle = 0
  FormatSpec = %.2w
  FormatSpecOverTolerance = %+.2w
  FormatSpecUnderTolerance = %+.2w
  Inverted = false
  LineAngle = 0
  LockPosition = false
  MeasureType = 1
  OverTolerance = 0
  References2D = -> [View027]
  Rotation = 0
  ScaleType = 2
  TheoreticalExact = false
  Type = 1
  UnderTolerance = 0
  X = -15.3592
  Y = -68.2817
FEATURE [Spreadsheet::Sheet] Spreadsheet011  label="et9"
  cells = A1='Qté; B1='Nom_de_la_piece; C1='Reference_AP; D1='Angle1; E1='Angle2; F1='percage; G1='longueur; A2=2; B2='BB1; C2='Tube carré 25 x 2; G2=685; A3=4; B3='BB2; C3='Tube carré 25 x 2; G3=560
FEATURE [Spreadsheet::Sheet] Spreadsheet012  label="et10"
  cells = A1='Qté; B1='Nom_de_la_piece; C1='Reference_AP; D1='Angle1; E1='Angle2; F1='percage; G1='longueur; A2=2; B2='A16; C2='Tube carré 30 x 2; G2=50
FEATURE [TechDraw::DrawViewSpreadsheet] Sheet007
  CellEnd = g3
  CellStart = A1
  Font = osifont
  LineWidth = 0.35
  LockPosition = false
  Rotation = 0
  ScaleType = 2
  Source = -> Spreadsheet011
  Symbol = <blob: 4651 chars omitted>
  TextSize = 12
  X = 224.133
  Y = 16.8524
FEATURE [TechDraw::DrawViewAnnotation] Annotation019
  Font = osifont
  LineSpace = 100
  LockPosition = false
  MaxWidth = -1
  Rotation = 0
  ScaleType = 2
  Text = souder les pièces du fond de la brouette
  TextSize = 5
  TextStyle = 0
  X = 224.133
  Y = 95.379
FEATURE [TechDraw::DrawViewSpreadsheet] Sheet008
  CellEnd = g2
  CellStart = A1
  Font = osifont
  LineWidth = 0.35
  LockPosition = false
  Rotation = 0
  ScaleType = 2
  Source = -> Spreadsheet012
  Symbol = <blob: 3237 chars omitted>
  TextSize = 12
  X = 224.813
  Y = 13.0902
FEATURE [TechDraw::DrawGeomHatch] GeomHatch014  label="Hachures géométriques014"
  FilePattern = <userpath>\Desktop\bureau\FreeCAD_1.0.0-conda-Windows-x86_64-py311\data\Mod/TechDraw/PAT/FCPAT.pat
  NamePattern = Diamond2
  PatternOffset = (0,0,0)
  PatternRotation = 0
  ScalePattern = 1
  Source = -> ProjItem014 [Face41,Face40]
FEATURE [TechDraw::DrawGeomHatch] GeomHatch015  label="Hachures géométriques015"
  FilePattern = <userpath>\Desktop\bureau\FreeCAD_1.0.0-conda-Windows-x86_64-py311\data\Mod/TechDraw/PAT/FCPAT.pat
  NamePattern = Diamond2
  PatternOffset = (0,0,0)
  PatternRotation = 0
  ScalePattern = 1
  Source = -> View028 [Face35]
FEATURE [TechDraw::DrawViewAnnotation] Annotation020
  Font = osifont
  LineSpace = 100
  LockPosition = false
  MaxWidth = -1
  Rotation = 0
  ScaleType = 2
  Text = pointez les pièces A16 | puis installez le fond de brouette | afin de vous assurez que  | les pièces A16 soient au bon endroit | puis soudez
  TextSize = 5
  TextStyle = 0
  X = 79.8462
  Y = 37.2237
FEATURE [TechDraw::DrawProjGroupItem] View037
  CoarseView = false
  Direction = (0.57735,-0.57735,0.57735)
  Focus = 100
  HardHidden = false
  IsoCount = 0
  IsoHidden = false
  IsoVisible = false
  LockPosition = true
  Perspective = false
  Rotation = 0
  RotationVector = (1,0,0)
  Scale = 0.071429
  ScaleType = 2
  ScrubCount = 1
  SeamHidden = false
  SeamVisible = false
  SmoothHidden = false
  SmoothVisible = true
  Type = 0
  X = 101.022
  XDirection = (0.707107,0.707107,0)
  XSource = -> [rondelle_029,rondelle_028,A18005,A13,A18004,A18003,A18002,A18001,A18,A17001,A17,BB1004,BB1003,BB2,BB3,BB1001,BB1,A16001,A16,A15002,A15001,A14008,A15,A10006,A10,A11001,A11,A14004,A14003,A14002,A2005,A2004,A14001,A13001,A12003,A12002,A12001,A12,A9001,A9,A8002,A7004,A7003,A6001,A5002,A5001,A2003,A4002,A4001,A3002,A3001,A1004,A1001,A2001]
  Y = 90.0259
FEATURE [TechDraw::DrawProjGroupItem] View038
  CoarseView = false
  Direction = (0.57735,-0.57735,0.57735)
  Focus = 100
  HardHidden = false
  IsoCount = 0
  IsoHidden = false
  IsoVisible = false
  LockPosition = true
  Perspective = false
  Rotation = 0
  RotationVector = (1,0,0)
  Scale = 0.071429
  ScaleType = 2
  ScrubCount = 1
  SeamHidden = false
  SeamVisible = false
  SmoothHidden = false
  SmoothVisible = true
  Type = 0
  X = 58.9158
  XDirection = (0.707107,0.707107,0)
  XSource = -> [Roue_increvable___389___axe25_L_82002]
  Y = 48.4523
FEATURE [TechDraw::DrawProjGroupItem] View039
  CoarseView = false
  Direction = (0.57735,-0.57735,0.57735)
  Focus = 100
  HardHidden = false
  IsoCount = 0
  IsoHidden = false
  IsoVisible = false
  LockPosition = true
  Perspective = false
  Rotation = 0
  RotationVector = (1,0,0)
  Scale = 0.071429
  ScaleType = 2
  ScrubCount = 1
  SeamHidden = false
  SeamVisible = false
  SmoothHidden = false
  SmoothVisible = true
  Type = 0
  X = 40.5957
  XDirection = (0.707107,0.707107,0)
  XSource = -> [rondelle_026]
  Y = 35.7098
FEATURE [TechDraw::DrawProjGroupItem] View040
  CoarseView = false
  Direction = (0.57735,-0.57735,0.57735)
  Focus = 100
  HardHidden = false
  IsoCount = 0
  IsoHidden = false
  IsoVisible = false
  LockPosition = true
  Perspective = false
  Rotation = 0
  RotationVector = (1,0,0)
  Scale = 0.071429
  ScaleType = 2
  ScrubCount = 1
  SeamHidden = false
  SeamVisible = false
  SmoothHidden = false
  SmoothVisible = true
  Type = 0
  X = 22.883
  XDirection = (0.707107,0.707107,0)
  XSource = -> [goupille_elastique_5_x_082]
  Y = 25.1863
FEATURE [TechDraw::DrawProjGroupItem] View041
  CoarseView = false
  Direction = (0.57735,-0.57735,0.57735)
  Focus = 100
  HardHidden = false
  IsoCount = 0
  IsoHidden = false
  IsoVisible = false
  LockPosition = true
  Perspective = false
  Rotation = 0
  RotationVector = (1,0,0)
  Scale = 0.071429
  ScaleType = 2
  ScrubCount = 1
  SeamHidden = false
  SeamVisible = false
  SmoothHidden = false
  SmoothVisible = true
  Type = 0
  X = 168.608
  XDirection = (0.707107,0.707107,0)
  XSource = -> [goupille_elastique_5_x_081]
  Y = 123.296
FEATURE [TechDraw::DrawProjGroupItem] View042
  CoarseView = false
  Direction = (0.57735,-0.57735,0.57735)
  Focus = 100
  HardHidden = false
  IsoCount = 0
  IsoHidden = false
  IsoVisible = false
  LockPosition = true
  Perspective = false
  Rotation = 0
  RotationVector = (1,0,0)
  Scale = 0.071429
  ScaleType = 2
  ScrubCount = 1
  SeamHidden = false
  SeamVisible = false
  SmoothHidden = false
  SmoothVisible = true
  Type = 0
  X = 155.627
  XDirection = (0.707107,0.707107,0)
  XSource = -> [rondelle_026]
  Y = 112.612
FEATURE [TechDraw::DrawProjGroupItem] View043
  CoarseView = false
  Direction = (0.57735,-0.57735,0.57735)
  Focus = 100
  HardHidden = false
  IsoCount = 0
  IsoHidden = false
  IsoVisible = false
  LockPosition = true
  Perspective = false
  Rotation = 0
  RotationVector = (1,0,0)
  Scale = 0.071429
  ScaleType = 2
  ScrubCount = 1
  SeamHidden = false
  SeamVisible = false
  SmoothHidden = false
  SmoothVisible = true
  Type = 0
  X = 138.686
  XDirection = (0.707107,0.707107,0)
  XSource = -> [Roue_increvable___389___axe25_L_82001]
  Y = 99.0624
FEATURE [TechDraw::DrawViewAnnotation] Annotation021
  Font = osifont
  LineSpace = 100
  LockPosition = false
  MaxWidth = -1
  Rotation = 0
  ScaleType = 2
  Text = Il ne vous reste plus qu'a installer les roues - rondelles - goupilles
  TextSize = 5
  TextStyle = 0
  X = 175.693
  Y = 146.836
FEATURE [TechDraw::DrawViewAnnotation] Annotation022
  Font = osifont
  LineSpace = 100
  LockPosition = false
  MaxWidth = -1
  Rotation = 0
  ScaleType = 2
  Text = Votre brouette est  | maintenant opérationel !
  TextSize = 5
  TextStyle = 0
  X = 241.061
  Y = 125.586
FEATURE [TechDraw::DrawViewAnnotation] Annotation023
  Font = osifont
  LineSpace = 100
  LockPosition = false
  MaxWidth = -1
  Rotation = 0
  ScaleType = 2
  Text = S'il vous plait faite | nous des retours :
  TextSize = 5
  TextStyle = 0
  X = 241.061
  Y = 80.0899
FEATURE [TechDraw::DrawViewAnnotation] Annotation024
  Font = osifont
  LineSpace = 100
  LockPosition = false
  MaxWidth = -1
  Rotation = 0
  ScaleType = 2
  Text = Brouette Balance
  TextSize = 5
  TextStyle = 0
  X = 55.7589
  Y = 197.741
FEATURE [TechDraw::DrawViewAnnotation] Annotation025
  Font = osifont
  LineSpace = 100
  LockPosition = false
  MaxWidth = -1
  Rotation = 0
  ScaleType = 2
  Text = 01/03/25
  TextSize = 5
  TextStyle = 0
  X = 45.099
  Y = 187.086
FEATURE [TechDraw::DrawViewAnnotation] Annotation026
  Font = osifont
  LineSpace = 100
  LockPosition = false
  MaxWidth = -1
  Rotation = 0
  ScaleType = 2
  Text = 2/16
  TextSize = 5
  TextStyle = 0
  X = 96.9599
  Y = 187.086
FEATURE [TechDraw::DrawViewAnnotation] Annotation027
  Font = osifont
  LineSpace = 100
  LockPosition = false
  MaxWidth = -1
  Rotation = 0
  ScaleType = 2
  Text = 1
  TextSize = 5
  TextStyle = 0
  X = 112.354
  Y = 177.627
FEATURE [TechDraw::DrawViewAnnotation] Annotation028
  Font = osifont
  LineSpace = 100
  LockPosition = false
  MaxWidth = -1
  Rotation = 0
  ScaleType = 2
  Text = Vue générale
  TextSize = 5
  TextStyle = 0
  X = 49.4331
  Y = 177.627
FEATURE [TechDraw::DrawViewAnnotation] Annotation029
  Font = osifont
  LineSpace = 100
  LockPosition = false
  MaxWidth = -1
  Rotation = 0
  ScaleType = 2
  Text = Brouette Balance
  TextSize = 5
  TextStyle = 0
  X = 55.7589
  Y = 197.741
FEATURE [TechDraw::DrawViewAnnotation] Annotation030
  Font = osifont
  LineSpace = 100
  LockPosition = false
  MaxWidth = -1
  Rotation = 0
  ScaleType = 2
  Text = 01/03/25
  TextSize = 5
  TextStyle = 0
  X = 45.099
  Y = 187.086
FEATURE [TechDraw::DrawViewAnnotation] Annotation031
  Font = osifont
  LineSpace = 100
  LockPosition = false
  MaxWidth = -1
  Rotation = 0
  ScaleType = 2
  Text = 3/16
  TextSize = 5
  TextStyle = 0
  X = 101.233
  Y = 187.086
FEATURE [TechDraw::DrawViewAnnotation] Annotation032
  Font = osifont
  LineSpace = 100
  LockPosition = false
  MaxWidth = -1
  Rotation = 0
  ScaleType = 2
  Text = 1
  TextSize = 5
  TextStyle = 0
  X = 112.354
  Y = 177.627
FEATURE [TechDraw::DrawViewAnnotation] Annotation033
  Font = osifont
  LineSpace = 100
  LockPosition = false
  MaxWidth = -1
  Rotation = 0
  ScaleType = 2
  Text = nom des pièces
  TextSize = 5
  TextStyle = 0
  X = 53.1199
  Y = 177.627
FEATURE [TechDraw::DrawViewBalloon] Balloon053  label="Infobulle053"
  BubbleShape = 3
  EndType = 0
  EndTypeScale = 1
  KinkLength = 5
  LockPosition = false
  OriginX = 5.80913
  OriginY = 10.1878
  Rotation = 0
  ScaleType = 2
  ShapeScale = 1
  SourceView = -> View006
  Text = BB - Butté de brouette
  TextWrapLen = -1
  X = 1145.13
  Y = 168.992
FEATURE [TechDraw::DrawViewBalloon] Balloon054  label="Infobulle054"
  BubbleShape = 3
  EndType = 0
  EndTypeScale = 1
  KinkLength = 5
  LockPosition = false
  OriginX = -472.877
  OriginY = 309.371
  Rotation = 0
  ScaleType = 2
  ShapeScale = 1
  SourceView = -> View005
  Text = A - Chassis
  TextWrapLen = -1
  X = 384.056
  Y = 907.447
FEATURE [TechDraw::DrawViewBalloon] Balloon055  label="Infobulle055"
  BubbleShape = 3
  EndType = 0
  EndTypeScale = 1
  KinkLength = 5
  LockPosition = false
  OriginX = -739.578
  OriginY = -404.447
  Rotation = 0
  ScaleType = 2
  ShapeScale = 1
  SourceView = -> View005
  Text = Roues
  TextWrapLen = -1
  X = -1310.28
  Y = -96.6043
FEATURE [TechDraw::DrawViewBalloon] Balloon056  label="Infobulle056"
  BubbleShape = 3
  EndType = 0
  EndTypeScale = 1
  KinkLength = 5
  LockPosition = false
  OriginX = -18.1194
  OriginY = 3.9531
  Rotation = 0
  ScaleType = 2
  ShapeScale = 1
  SourceView = -> View011
  Text = Rondelles et goupilles
  TextWrapLen = -1
  X = -824.146
  Y = 186.289
FEATURE [TechDraw::DrawPage] Page001  label="Feuille001"
  KeepUpdated = true
  NextBalloonIndex = 5
  ProjectionType = 0
  Template = -> Template001
  Views = -> [View003,View004,View005,View006,View010,View011,Annotation024,Annotation025,Annotation026,Annotation027,Annotation028,Balloon053,Balloon054,Balloon055,Balloon056]
FEATURE [TechDraw::DrawViewBalloon] Balloon057  label="Infobulle057"
  BubbleShape = 3
  EndType = 0
  EndTypeScale = 1
  KinkLength = 5
  LockPosition = false
  OriginX = -632.058
  OriginY = -75.7911
  Rotation = 0
  ScaleType = 2
  ShapeScale = 1
  SourceView = -> View007
  Text = A14
  TextWrapLen = -1
  X = -890.655
  Y = -195.759
FEATURE [TechDraw::DrawViewAnnotation] Annotation034
  Font = osifont
  LineSpace = 100
  LockPosition = false
  MaxWidth = -1
  Rotation = 0
  ScaleType = 2
  Text = Brouette Balance
  TextSize = 5
  TextStyle = 0
  X = 55.7589
  Y = 197.741
FEATURE [TechDraw::DrawViewAnnotation] Annotation035
  Font = osifont
  LineSpace = 100
  LockPosition = false
  MaxWidth = -1
  Rotation = 0
  ScaleType = 2
  Text = 01/03/25
  TextSize = 5
  TextStyle = 0
  X = 45.099
  Y = 187.086
FEATURE [TechDraw::DrawViewAnnotation] Annotation036
  Font = osifont
  LineSpace = 100
  LockPosition = false
  MaxWidth = -1
  Rotation = 0
  ScaleType = 2
  Text = 1/16
  TextSize = 5
  TextStyle = 0
  X = 102.162
  Y = 187.086
FEATURE [TechDraw::DrawViewAnnotation] Annotation037
  Font = osifont
  LineSpace = 100
  LockPosition = false
  MaxWidth = -1
  Rotation = 0
  ScaleType = 2
  Text = 1
  TextSize = 5
  TextStyle = 0
  X = 112.354
  Y = 177.627
FEATURE [TechDraw::DrawViewAnnotation] Annotation038
  Font = osifont
  LineSpace = 100
  LockPosition = false
  MaxWidth = -1
  Rotation = 0
  ScaleType = 2
  Text = Présentation
  TextSize = 5
  TextStyle = 0
  X = 49.4331
  Y = 177.627
FEATURE [TechDraw::DrawPage] Page  label="Feuille"
  KeepUpdated = true
  NextBalloonIndex = 1
  ProjectionType = 0
  Template = -> Template
  Views = -> [ProjGroup,DimExtent,DimExtent001,Dimension,Dimension001,DimExtent002,Dimension002,Annotation034,Annotation035,Annotation036,Annotation037,Annotation038]
FEATURE [TechDraw::DrawViewSpreadsheet] Sheet009
  CellEnd = g24
  CellStart = A1
  Font = osifont
  LineWidth = 0.35
  LockPosition = false
  Rotation = 0
  Scale = 0.9
  ScaleType = 2
  Source = -> BOM
  Symbol = <blob: 36565 chars omitted>
  TextSize = 12
  X = 239.551
  Y = 90.1923
FEATURE [TechDraw::DrawViewAnnotation] Annotation039
  Font = osifont
  LineSpace = 100
  LockPosition = false
  MaxWidth = -1
  Rotation = 0
  ScaleType = 2
  Text = Nomenclature complète
  TextSize = 5
  TextStyle = 0
  X = 220.085
  Y = 183.945
FEATURE [TechDraw::DrawViewAnnotation] Annotation040
  Font = osifont
  LineSpace = 100
  LockPosition = false
  MaxWidth = -1
  Rotation = 0
  ScaleType = 0
  Text = gueule de loup : détail à l'echelle 1 | (vous pouvez imprimer et scotcher | le détail en bout de barre)
  TextSize = 4
  TextStyle = 0
  X = 247.31
  Y = 166.439
FEATURE [TechDraw::DrawViewAnnotation] Annotation041
  Font = osifont
  LineSpace = 100
  LockPosition = false
  MaxWidth = -1
  Rotation = 0
  ScaleType = 2
  Text = Brouette Balance
  TextSize = 5
  TextStyle = 0
  X = 55.7589
  Y = 197.741
FEATURE [TechDraw::DrawViewAnnotation] Annotation042
  Font = osifont
  LineSpace = 100
  LockPosition = false
  MaxWidth = -1
  Rotation = 0
  ScaleType = 2
  Text = 01/03/25
  TextSize = 5
  TextStyle = 0
  X = 45.099
  Y = 187.086
FEATURE [TechDraw::DrawViewAnnotation] Annotation043
  Font = osifont
  LineSpace = 100
  LockPosition = false
  MaxWidth = -1
  Rotation = 0
  ScaleType = 2
  Text = 4/16
  TextSize = 5
  TextStyle = 0
  X = 101.233
  Y = 187.086
FEATURE [TechDraw::DrawViewAnnotation] Annotation044
  Font = osifont
  LineSpace = 100
  LockPosition = false
  MaxWidth = -1
  Rotation = 0
  ScaleType = 2
  Text = 1
  TextSize = 5
  TextStyle = 0
  X = 112.354
  Y = 177.627
FEATURE [TechDraw::DrawViewAnnotation] Annotation045
  Font = osifont
  LineSpace = 100
  LockPosition = false
  MaxWidth = -1
  Rotation = 0
  ScaleType = 2
  Text = Côtes utiles
  TextSize = 5
  TextStyle = 0
  X = 48.9158
  Y = 177.627
FEATURE [TechDraw::DrawProjGroupItem] ProjItem016  label="Dessous001"
  CoarseView = false
  Direction = (0,0,-1)
  Focus = 100
  HardHidden = false
  IsoCount = 0
  IsoHidden = false
  IsoVisible = false
  LockPosition = true
  Perspective = false
  Rotation = 0
  RotationVector = (1,0,0)
  ScaleType = 0
  ScrubCount = 1
  SeamHidden = false
  SeamVisible = false
  SmoothHidden = false
  SmoothVisible = true
  Type = 5
  X = 0
  XDirection = (1,0,0)
  XSource = <same value as first occurrence — deduplicated (x8 in doc)>
  Y = 77.9588
FEATURE [TechDraw::DrawViewDimension] Dimension049  label="Cote049"
  AngleOverride = false
  Arbitrary = false
  ArbitraryTolerances = false
  BoxCorners = (2) [(-87.1671,-22.9334,-1e-07),(87.1671,22.9334,1e-07)]
  EqualTolerance = true
  ExtensionAngle = 0
  FormatSpec = %.2w
  FormatSpecOverTolerance = %+.2w
  FormatSpecUnderTolerance = %+.2w
  Inverted = false
  LineAngle = 0
  LockPosition = false
  MeasureType = 1
  OverTolerance = 0
  References2D = -> [ProjItem016]
  Rotation = 0
  ScaleType = 0
  TheoreticalExact = false
  Type = 2
  UnderTolerance = 0
  X = -101.334
  Y = -20.4015
FEATURE [TechDraw::DrawViewDimension] Dimension050  label="Cote050"
  AngleOverride = false
  Arbitrary = false
  ArbitraryTolerances = false
  BoxCorners = (2) [(-87.1671,-22.9334,-1e-07),(87.1671,22.9334,1e-07)]
  EqualTolerance = true
  ExtensionAngle = 0
  FormatSpec = %.0w
  FormatSpecOverTolerance = %+.2w
  FormatSpecUnderTolerance = %+.2w
  Inverted = false
  LineAngle = 0
  LockPosition = false
  MeasureType = 1
  OverTolerance = 0
  References2D = -> [ProjItem016]
  Rotation = 0
  ScaleType = 0
  TheoreticalExact = false
  Type = 0
  UnderTolerance = 0
  X = -72.1023
  Y = 37.4541
FEATURE [TechDraw::DrawViewDimension] Dimension056  label="Cote056"
  AngleOverride = false
  Arbitrary = false
  ArbitraryTolerances = false
  BoxCorners = (2) [(-87.1671,-22.5668,-1e-07),(87.1671,22.5668,1e-07)]
  EqualTolerance = true
  ExtensionAngle = 0
  FormatSpec = %.2w
  FormatSpecOverTolerance = %+.2w
  FormatSpecUnderTolerance = %+.2w
  Inverted = false
  LineAngle = 0
  LockPosition = false
  MeasureType = 1
  OverTolerance = 0
  References2D = -> [ProjItem016]
  Rotation = 0
  ScaleType = 0
  TheoreticalExact = false
  Type = 0
  UnderTolerance = 0
  X = 58.1049
  Y = 2.43473
FEATURE [TechDraw::DrawProjGroupItem] ProjItem017  label="Gauche007"
  CoarseView = false
  Direction = (-1,-1e-16,0)
  Focus = 100
  HardHidden = false
  IsoCount = 0
  IsoHidden = false
  IsoVisible = false
  LockPosition = false
  Perspective = false
  Rotation = 0
  RotationVector = (1,0,0)
  ScaleType = 0
  ScrubCount = 1
  SeamHidden = false
  SeamVisible = false
  SmoothHidden = false
  SmoothVisible = true
  Type = 1
  X = 125.101
  XDirection = (1e-16,-1,0)
  XSource = <same value as first occurrence — deduplicated (x8 in doc)>
  Y = 0
FEATURE [TechDraw::DrawViewDimension] Dimension063  label="Cote063"
  AngleOverride = false
  Arbitrary = false
  ArbitraryTolerances = false
  BoxCorners = (2) [(-22.9001,-22.11,-1e-07),(22.9001,22.11,1e-07)]
  EqualTolerance = true
  ExtensionAngle = 0
  FormatSpec = %.0w
  FormatSpecOverTolerance = %+.2w
  FormatSpecUnderTolerance = %+.2w
  Inverted = false
  LineAngle = 0
  LockPosition = false
  MeasureType = 1
  OverTolerance = 0
  References2D = -> [ProjItem017]
  Rotation = 0
  ScaleType = 0
  TheoreticalExact = false
  Type = 0
  UnderTolerance = 0
  X = 13.2672
  Y = -24.4062
FEATURE [TechDraw::DrawViewDimension] Dimension064  label="Cote064"
  AngleOverride = false
  Arbitrary = false
  ArbitraryTolerances = false
  BoxCorners = (2) [(-22.9334,-22.11,-1e-07),(22.9334,22.11,1e-07)]
  EqualTolerance = true
  ExtensionAngle = 0
  FormatSpec = %.0w
  FormatSpecOverTolerance = %+.2w
  FormatSpecUnderTolerance = %+.2w
  Inverted = false
  LineAngle = 0
  LockPosition = false
  MeasureType = 1
  OverTolerance = 0
  References2D = -> [ProjItem017]
  Rotation = 0
  ScaleType = 0
  TheoreticalExact = false
  Type = 0
  UnderTolerance = 0
  X = -17.54
  Y = -31.4062
FEATURE [TechDraw::DrawSVGTemplate] Template018  label="Modèle018"
  Height = 210
  Orientation = 1
  Template = C:/Program Files/FreeCAD_0.19/data/Mod/TechDraw/Templates/A4_LandscapeTDteste.svg
  Width = 297
FEATURE [TechDraw::DrawProjGroupItem] View044  label="Front014"
  CoarseView = false
  Direction = (0,-1,0)
  Focus = 100
  HardHidden = false
  IsoCount = 0
  IsoHidden = false
  IsoVisible = false
  LockPosition = true
  Perspective = false
  Rotation = 0
  RotationVector = (1,0,0)
  Scale = 0.066667
  ScaleType = 2
  ScrubCount = 1
  SeamHidden = false
  SeamVisible = false
  SmoothHidden = false
  SmoothVisible = true
  Type = 0
  X = 0
  XDirection = (1,0,0)
  XSource = <same value as first occurrence — deduplicated (x8 in doc)>
  Y = 0
FEATURE [TechDraw::DrawViewDimension] Dimension060  label="Cote060"
  AngleOverride = false
  Arbitrary = false
  ArbitraryTolerances = false
  BoxCorners = (2) [(-87.1671,-22.11,-1e-07),(87.1671,22.1097,1e-07)]
  EqualTolerance = true
  ExtensionAngle = 0
  FormatSpec = %.0w
  FormatSpecOverTolerance = %+.2w
  FormatSpecUnderTolerance = %+.2w
  Inverted = false
  LineAngle = 0
  LockPosition = false
  MeasureType = 1
  OverTolerance = 0
  References2D = -> [View044]
  Rotation = 0
  ScaleType = 0
  TheoreticalExact = false
  Type = 1
  UnderTolerance = 0
  X = 67.271
  Y = -17.3286
FEATURE [TechDraw::DrawViewDimension] Dimension061  label="Cote061"
  AngleOverride = false
  Arbitrary = false
  ArbitraryTolerances = false
  BoxCorners = (2) [(-87.1671,-22.11,-1e-07),(87.1671,22.1097,1e-07)]
  EqualTolerance = true
  ExtensionAngle = 0
  FormatSpec = %.0w
  FormatSpecOverTolerance = %+.2w
  FormatSpecUnderTolerance = %+.2w
  Inverted = false
  LineAngle = 0
  LockPosition = false
  MeasureType = 1
  OverTolerance = 0
  References2D = -> [View044]
  Rotation = 0
  ScaleType = 0
  TheoreticalExact = false
  Type = 2
  UnderTolerance = 0
  X = 80.9001
  Y = 6.41069
FEATURE [TechDraw::DrawViewDimension] Dimension062  label="Cote062"
  AngleOverride = false
  Arbitrary = false
  ArbitraryTolerances = false
  BoxCorners = (2) [(-87.1671,-22.11,-1e-07),(87.1671,22.1097,1e-07)]
  EqualTolerance = true
  ExtensionAngle = 0
  FormatSpec = %.2w
  FormatSpecOverTolerance = %+.2w
  FormatSpecUnderTolerance = %+.2w
  Inverted = false
  LineAngle = 0
  LockPosition = false
  MeasureType = 1
  OverTolerance = 0
  References2D = -> [View044]
  Rotation = 0
  ScaleType = 0
  TheoreticalExact = false
  Type = 1
  UnderTolerance = 0
  X = -18.1668
  Y = 16.9283
FEATURE [TechDraw::DrawViewDimension] Dimension065  label="Cote065"
  AngleOverride = false
  Arbitrary = false
  ArbitraryTolerances = false
  BoxCorners = (2) [(-87.1671,-22.11,-1e-07),(87.1671,22.1097,1e-07)]
  EqualTolerance = true
  ExtensionAngle = 0
  FormatSpec = %.0w
  FormatSpecOverTolerance = %+.2w
  FormatSpecUnderTolerance = %+.2w
  Inverted = false
  LineAngle = 0
  LockPosition = false
  MeasureType = 1
  OverTolerance = 0
  References2D = -> [View044]
  Rotation = 0
  ScaleType = 0
  TheoreticalExact = false
  Type = 1
  UnderTolerance = 0
  X = 70.7694
  Y = -5.77901
FEATURE [TechDraw::DrawProjGroup] ProjGroup014
  Anchor = -> View044
  AutoDistribute = true
  LockPosition = false
  ProjectionType = 0
  Rotation = 0
  Scale = 0.066667
  ScaleType = 2
  Views = -> [View044,ProjItem016,ProjItem017]
  X = 119.416
  XSource = -> [A2001,A1001,A1004,A3001,A3002,A4001,A4002,A2003,A5001,A5002,A6001,A7003,A7004,A8002,A9,A9001,A12,A12001,A12002,A12003,A13001,A14001,A2004,A2005,A14002,A14003,A14004,A11,A11001,A10,A10006,A15,A14008,A15001,A15002,A16,A16001,A17,A17001,A18,A18001,A18002,A18003,A18004,A13,A18005]
  Y = 44.0069
  spacingX = 15
  spacingY = 15
FEATURE [TechDraw::DrawProjGroupItem] View045
  CoarseView = false
  Direction = (0,-1,0)
  Focus = 100
  HardHidden = false
  IsoCount = 0
  IsoHidden = false
  IsoVisible = false
  LockPosition = false
  Perspective = false
  Rotation = 0
  RotationVector = (1,0,0)
  Scale = 0.2
  ScaleType = 2
  ScrubCount = 1
  SeamHidden = false
  SeamVisible = false
  SmoothHidden = false
  SmoothVisible = true
  Source = -> [A8004]
  Type = 0
  X = 225.36
  XDirection = (1,0,0)
  Y = 112.75
FEATURE [TechDraw::DrawViewBalloon] Balloon068  label="Infobulle068"
  BubbleShape = 3
  EndType = 0
  EndTypeScale = 1
  KinkLength = 5
  LockPosition = false
  OriginX = 1.29779
  OriginY = -63.1508
  Rotation = 0
  ScaleType = 0
  ShapeScale = 1
  SourceView = -> View045
  Text = A9
  TextWrapLen = -1
  X = -85.4403
  Y = -172.26
FEATURE [TechDraw::DrawViewDetail] Detail003  label="Detail 001"
  AnchorPoint = (0,110,0)
  BaseView = -> View045
  CoarseView = false
  Direction = (0,-1,0)
  Focus = 100
  HardHidden = false
  IsoCount = 0
  IsoHidden = false
  IsoVisible = false
  LockPosition = false
  Perspective = false
  Radius = 20
  Rotation = 0
  ScaleType = 2
  ScrubCount = 1
  SeamHidden = false
  SeamVisible = false
  ShowHighlight = true
  ShowMatting = true
  SmoothHidden = false
  SmoothVisible = true
  Source = -> [A8004]
  X = 268.254
  XDirection = (1,0,0)
  Y = 118.389
FEATURE [TechDraw::DrawViewDimension] Dimension054  label="Cote054"
  AngleOverride = false
  Arbitrary = false
  ArbitraryTolerances = false
  BoxCorners = (2) [(-2.5,-21.5,-1e-07),(2.5,21.5,1e-07)]
  EqualTolerance = true
  ExtensionAngle = 0
  FormatSpec = ⌀%.2w
  FormatSpecOverTolerance = %+.2w
  FormatSpecUnderTolerance = %+.2w
  Inverted = false
  LineAngle = 0
  LockPosition = false
  MeasureType = 1
  OverTolerance = 0
  References2D = -> [View045]
  Rotation = 0
  ScaleType = 0
  TheoreticalExact = false
  Type = 5
  UnderTolerance = 0
  X = 11.3357
  Y = -3.66822
FEATURE [TechDraw::DrawLeaderLine] LeaderLine001  label="Ligne de repère001"
  AutoHorizontal = false
  EndSymbol = 0
  LeaderParent = -> Detail003
  LockPosition = true
  RotatesWithParent = false
  Rotation = 0
  Scalable = false
  ScaleType = 0
  StartSymbol = 7
  WayPoints = (2) [(0,0,0),(-8.65063,39.088,0)]
  X = 13.4421
  Y = 40.5001
FEATURE [TechDraw::DrawViewDimension] Dimension067  label="Cote067"
  AngleOverride = false
  Arbitrary = false
  ArbitraryTolerances = false
  BoxCorners = (2) [(-87.1671,-22.9334,-1e-07),(87.1671,22.9334,1e-07)]
  EqualTolerance = true
  ExtensionAngle = 0
  FormatSpec = %.2w
  FormatSpecOverTolerance = %+.2w
  FormatSpecUnderTolerance = %+.2w
  Inverted = false
  LineAngle = 0
  LockPosition = false
  MeasureType = 1
  OverTolerance = 0
  References2D = -> [ProjItem016]
  Rotation = 0
  ScaleType = 2
  TheoreticalExact = false
  Type = 1
  UnderTolerance = 0
  X = -42.2941
  Y = 33.6912
FEATURE [TechDraw::DrawViewDimension] Dimension068  label="Cote068"
  AngleOverride = false
  Arbitrary = false
  ArbitraryTolerances = false
  BoxCorners = (2) [(-87.1671,-22.9334,-1e-07),(87.1671,22.9334,1e-07)]
  EqualTolerance = true
  ExtensionAngle = 0
  FormatSpec = %.2w
  FormatSpecOverTolerance = %+.2w
  FormatSpecUnderTolerance = %+.2w
  Inverted = false
  LineAngle = 0
  LockPosition = false
  MeasureType = 1
  OverTolerance = 0
  References2D = -> [ProjItem016]
  Rotation = 0
  ScaleType = 2
  TheoreticalExact = false
  Type = 1
  UnderTolerance = 0
  X = 4.21488
  Y = 29.9871
FEATURE [TechDraw::DrawViewDimension] Dimension069  label="Cote069"
  AngleOverride = false
  Arbitrary = false
  ArbitraryTolerances = false
  BoxCorners = (2) [(-87.1671,-22.9334,-1e-07),(87.1671,22.9334,1e-07)]
  EqualTolerance = true
  ExtensionAngle = 0
  FormatSpec = %.2w
  FormatSpecOverTolerance = %+.2w
  FormatSpecUnderTolerance = %+.2w
  Inverted = false
  LineAngle = 0
  LockPosition = false
  MeasureType = 1
  OverTolerance = 0
  References2D = -> [ProjItem016]
  Rotation = 0
  ScaleType = 2
  TheoreticalExact = false
  Type = 2
  UnderTolerance = 0
  X = -92.8953
  Y = 5.14866
FEATURE [TechDraw::DrawViewBalloon] Balloon069  label="Infobulle069"
  BubbleShape = 3
  EndType = 0
  EndTypeScale = 1
  KinkLength = 2
  LockPosition = false
  OriginX = 320.009
  OriginY = -230.191
  Rotation = 0
  ScaleType = 2
  ShapeScale = 1
  SourceView = -> ProjItem003
  Text = A10
  TextWrapLen = -1
  X = 556.601
  Y = -332.191
FEATURE [TechDraw::DrawProjGroupItem] View046
  CoarseView = false
  Direction = (0.57735,-0.57735,0.57735)
  Focus = 100
  HardHidden = false
  IsoCount = 0
  IsoHidden = false
  IsoVisible = false
  LockPosition = false
  Perspective = false
  Rotation = 0
  RotationVector = (1,0,0)
  Scale = 0.04
  ScaleType = 2
  ScrubCount = 1
  SeamHidden = false
  SeamVisible = false
  SmoothHidden = false
  SmoothVisible = true
  Type = 0
  X = 244.516
  XDirection = (0.707107,0.707107,0)
  XSource = <same value as first occurrence — deduplicated (x8 in doc)>
  Y = 173.328
FEATURE [TechDraw::DrawPage] Page002  label="Feuille002"
  KeepUpdated = true
  NextBalloonIndex = 33
  ProjectionType = 0
  Template = -> Template002
  Views = -> [ProjGroup001,LeaderLine,Balloon,Balloon002,Balloon003,Balloon004,Balloon005,Balloon006,Balloon007,Balloon009,Balloon010,Balloon011,Balloon013,Balloon014,Balloon015,Balloon016,Balloon017,Balloon018,Balloon019,Balloon020,Annotation029,Annotation030,Annotation031,Annotation032,Annotation033,Balloon057,Balloon069,View046]
FEATURE [TechDraw::DrawViewDimension] Dimension070  label="Cote070"
  AngleOverride = false
  Arbitrary = false
  ArbitraryTolerances = false
  BoxCorners = (2) [(-12.5,2.5,0),(12.5,20.2,0)]
  EqualTolerance = true
  ExtensionAngle = 0
  FormatSpec = %.2w
  FormatSpecOverTolerance = %+.2w
  FormatSpecUnderTolerance = %+.2w
  Inverted = false
  LineAngle = 0
  LockPosition = false
  MeasureType = 1
  OverTolerance = 0
  References2D = -> [Detail003]
  Rotation = 0
  ScaleType = 2
  TheoreticalExact = false
  Type = 1
  UnderTolerance = 0
  X = 0
  Y = -25.9253
FEATURE [TechDraw::DrawPage] Page018  label="Feuille018"
  KeepUpdated = true
  NextBalloonIndex = 31
  ProjectionType = 0
  Template = -> Template018
  Views = -> [ProjGroup014,View045,Detail003,Dimension049,Dimension050,Dimension054,Dimension056,Dimension060,Dimension061,Dimension062,Dimension063,Dimension064,Dimension065,Annotation040,LeaderLine001,Balloon068,Annotation041,Annotation042,Annotation043,Annotation044,Annotation045,Dimension067,Dimension068,Dimension069,Dimension070]
FEATURE [TechDraw::DrawViewAnnotation] Annotation046
  Font = osifont
  LineSpace = 100
  LockPosition = false
  MaxWidth = -1
  Rotation = 0
  ScaleType = 2
  Text = Brouette Balance
  TextSize = 5
  TextStyle = 0
  X = 55.7589
  Y = 197.741
FEATURE [TechDraw::DrawViewAnnotation] Annotation047
  Font = osifont
  LineSpace = 100
  LockPosition = false
  MaxWidth = -1
  Rotation = 0
  ScaleType = 2
  Text = 01/03/25
  TextSize = 5
  TextStyle = 0
  X = 45.099
  Y = 187.086
FEATURE [TechDraw::DrawViewAnnotation] Annotation048
  Font = osifont
  LineSpace = 100
  LockPosition = false
  MaxWidth = -1
  Rotation = 0
  ScaleType = 2
  Text = 5/16
  TextSize = 5
  TextStyle = 0
  X = 101.233
  Y = 187.086
FEATURE [TechDraw::DrawViewAnnotation] Annotation049
  Font = osifont
  LineSpace = 100
  LockPosition = false
  MaxWidth = -1
  Rotation = 0
  ScaleType = 2
  Text = 1
  TextSize = 5
  TextStyle = 0
  X = 113.474
  Y = 177.627
FEATURE [TechDraw::DrawViewAnnotation] Annotation050
  Font = osifont
  LineSpace = 100
  LockPosition = false
  MaxWidth = -1
  Rotation = 0
  ScaleType = 2
  Text = B - Nomenclature
  TextSize = 5
  TextStyle = 0
  X = 58.7543
  Y = 177.627
FEATURE [TechDraw::DrawSVGTemplate] Template019  label="Modèle019"
  Height = 210
  Orientation = 1
  Template = C:/Program Files/FreeCAD_0.19/data/Mod/TechDraw/Templates/A4_LandscapeTDteste.svg
  Width = 297
FEATURE [TechDraw::DrawPage] Page003  label="Feuille003"
  KeepUpdated = true
  NextBalloonIndex = 6
  ProjectionType = 0
  Template = -> Template019
  Views = -> [ProjGroup002,Dimension003,Dimension004,Dimension005,Dimension006,Dimension007,Balloon022,Balloon023,Balloon024,Sheet009,Annotation039,Annotation046,Annotation047,Annotation048,Annotation049,Annotation050]
FEATURE [TechDraw::DrawViewAnnotation] Annotation052
  Font = osifont
  LineSpace = 100
  LockPosition = false
  MaxWidth = -1
  Rotation = 0
  ScaleType = 2
  Text = Brouette Balance
  TextSize = 5
  TextStyle = 0
  X = 55.7589
  Y = 197.741
FEATURE [TechDraw::DrawViewAnnotation] Annotation053
  Font = osifont
  LineSpace = 100
  LockPosition = false
  MaxWidth = -1
  Rotation = 0
  ScaleType = 2
  Text = 01/03/25
  TextSize = 5
  TextStyle = 0
  X = 45.099
  Y = 187.086
FEATURE [TechDraw::DrawViewAnnotation] Annotation054
  Font = osifont
  LineSpace = 100
  LockPosition = false
  MaxWidth = -1
  Rotation = 0
  ScaleType = 2
  Text = 6/16
  TextSize = 5
  TextStyle = 0
  X = 101.233
  Y = 187.086
FEATURE [TechDraw::DrawViewAnnotation] Annotation055
  Font = osifont
  LineSpace = 100
  LockPosition = false
  MaxWidth = -1
  Rotation = 0
  ScaleType = 2
  Text = 1
  TextSize = 5
  TextStyle = 0
  X = 113.474
  Y = 177.627
FEATURE [TechDraw::DrawViewAnnotation] Annotation056
  Font = osifont
  LineSpace = 100
  LockPosition = false
  MaxWidth = -1
  Rotation = 0
  ScaleType = 2
  Text = pas a pas etape 1
  TextSize = 5
  TextStyle = 0
  X = 58.7543
  Y = 177.627
FEATURE [TechDraw::DrawPage] Page007  label="Feuille007"
  KeepUpdated = true
  NextBalloonIndex = 34
  ProjectionType = 0
  Template = -> Template007
  Views = -> [ProjGroup003,Annotation,Balloon025,Balloon026,Balloon027,Balloon028,Dimension029,Dimension030,Dimension031,Dimension032,View029,Sheet,Annotation052,Annotation053,Annotation054,Annotation055,Annotation056]
FEATURE [TechDraw::DrawViewAnnotation] Annotation057
  Font = osifont
  LineSpace = 100
  LockPosition = false
  MaxWidth = -1
  Rotation = 0
  ScaleType = 2
  Text = Brouette Balance
  TextSize = 5
  TextStyle = 0
  X = 55.7589
  Y = 197.741
FEATURE [TechDraw::DrawViewAnnotation] Annotation058
  Font = osifont
  LineSpace = 100
  LockPosition = false
  MaxWidth = -1
  Rotation = 0
  ScaleType = 2
  Text = 01/03/25
  TextSize = 5
  TextStyle = 0
  X = 45.099
  Y = 187.086
FEATURE [TechDraw::DrawViewAnnotation] Annotation059
  Font = osifont
  LineSpace = 100
  LockPosition = false
  MaxWidth = -1
  Rotation = 0
  ScaleType = 2
  Text = 7/16
  TextSize = 5
  TextStyle = 0
  X = 101.233
  Y = 187.086
FEATURE [TechDraw::DrawViewAnnotation] Annotation060
  Font = osifont
  LineSpace = 100
  LockPosition = false
  MaxWidth = -1
  Rotation = 0
  ScaleType = 2
  Text = 1
  TextSize = 5
  TextStyle = 0
  X = 113.474
  Y = 177.627
FEATURE [TechDraw::DrawViewAnnotation] Annotation061
  Font = osifont
  LineSpace = 100
  LockPosition = false
  MaxWidth = -1
  Rotation = 0
  ScaleType = 2
  Text = pas a pas etape 2
  TextSize = 5
  TextStyle = 0
  X = 58.7543
  Y = 177.627
FEATURE [TechDraw::DrawPage] Page008  label="Feuille008"
  KeepUpdated = true
  NextBalloonIndex = 31
  ProjectionType = 0
  Template = -> Template008
  Views = -> [ProjGroup013,View031,Balloon029,Sheet001,Dimension033,Dimension034,Dimension035,Annotation007,Annotation057,Annotation058,Annotation059,Annotation060,Annotation061]
FEATURE [TechDraw::DrawViewAnnotation] Annotation062
  Font = osifont
  LineSpace = 100
  LockPosition = false
  MaxWidth = -1
  Rotation = 0
  ScaleType = 2
  Text = Brouette Balance
  TextSize = 5
  TextStyle = 0
  X = 55.7589
  Y = 197.741
FEATURE [TechDraw::DrawViewAnnotation] Annotation063
  Font = osifont
  LineSpace = 100
  LockPosition = false
  MaxWidth = -1
  Rotation = 0
  ScaleType = 2
  Text = 01/03/25
  TextSize = 5
  TextStyle = 0
  X = 45.099
  Y = 187.086
FEATURE [TechDraw::DrawViewAnnotation] Annotation064
  Font = osifont
  LineSpace = 100
  LockPosition = false
  MaxWidth = -1
  Rotation = 0
  ScaleType = 2
  Text = 8/16
  TextSize = 5
  TextStyle = 0
  X = 101.233
  Y = 187.086
FEATURE [TechDraw::DrawViewAnnotation] Annotation065
  Font = osifont
  LineSpace = 100
  LockPosition = false
  MaxWidth = -1
  Rotation = 0
  ScaleType = 2
  Text = 1
  TextSize = 5
  TextStyle = 0
  X = 112.278
  Y = 177.627
FEATURE [TechDraw::DrawViewAnnotation] Annotation066
  Font = osifont
  LineSpace = 100
  LockPosition = false
  MaxWidth = -1
  Rotation = 0
  ScaleType = 2
  Text = pas a pas etape 3
  TextSize = 5
  TextStyle = 0
  X = 58.7543
  Y = 177.627
FEATURE [TechDraw::DrawPage] Page009  label="Feuille009"
  KeepUpdated = true
  NextBalloonIndex = 37
  ProjectionType = 0
  Template = -> Template009
  Views = -> [ProjGroup007,View032,Dimension036,Dimension037,Balloon030,Balloon031,Balloon032,Balloon033,Balloon034,Balloon035,Sheet002,Annotation008,Annotation009,Annotation062,Annotation063,Annotation064,Annotation065,Annotation066]
FEATURE [TechDraw::DrawViewAnnotation] Annotation067
  Font = osifont
  LineSpace = 100
  LockPosition = false
  MaxWidth = -1
  Rotation = 0
  ScaleType = 2
  Text = Brouette Balance
  TextSize = 5
  TextStyle = 0
  X = 55.7589
  Y = 197.741
FEATURE [TechDraw::DrawViewAnnotation] Annotation068
  Font = osifont
  LineSpace = 100
  LockPosition = false
  MaxWidth = -1
  Rotation = 0
  ScaleType = 2
  Text = 01/03/25
  TextSize = 5
  TextStyle = 0
  X = 45.099
  Y = 187.086
FEATURE [TechDraw::DrawViewAnnotation] Annotation069
  Font = osifont
  LineSpace = 100
  LockPosition = false
  MaxWidth = -1
  Rotation = 0
  ScaleType = 2
  Text = 9/16
  TextSize = 5
  TextStyle = 0
  X = 101.233
  Y = 187.086
FEATURE [TechDraw::DrawViewAnnotation] Annotation070
  Font = osifont
  LineSpace = 100
  LockPosition = false
  MaxWidth = -1
  Rotation = 0
  ScaleType = 2
  Text = 1
  TextSize = 5
  TextStyle = 0
  X = 113.474
  Y = 177.627
FEATURE [TechDraw::DrawViewAnnotation] Annotation071
  Font = osifont
  LineSpace = 100
  LockPosition = false
  MaxWidth = -1
  Rotation = 0
  ScaleType = 2
  Text = pas a pas etape 4
  TextSize = 5
  TextStyle = 0
  X = 58.7543
  Y = 177.627
FEATURE [TechDraw::DrawPage] Page010  label="Feuille010"
  KeepUpdated = true
  NextBalloonIndex = 34
  ProjectionType = 0
  Template = -> Template010
  Views = -> [ProjGroup006,Balloon036,Balloon037,Balloon038,Balloon039,View033,Annotation010,Sheet003,Annotation067,Annotation068,Annotation069,Annotation070,Annotation071]
FEATURE [TechDraw::DrawViewAnnotation] Annotation072
  Font = osifont
  LineSpace = 100
  LockPosition = false
  MaxWidth = -1
  Rotation = 0
  ScaleType = 2
  Text = Brouette Balance
  TextSize = 5
  TextStyle = 0
  X = 54.7006
  Y = 197.741
FEATURE [TechDraw::DrawViewAnnotation] Annotation073
  Font = osifont
  LineSpace = 100
  LockPosition = false
  MaxWidth = -1
  Rotation = 0
  ScaleType = 2
  Text = 01/03/25
  TextSize = 5
  TextStyle = 0
  X = 45.099
  Y = 187.086
FEATURE [TechDraw::DrawViewAnnotation] Annotation074
  Font = osifont
  LineSpace = 100
  LockPosition = false
  MaxWidth = -1
  Rotation = 0
  ScaleType = 2
  Text = 12/16
  TextSize = 5
  TextStyle = 0
  X = 101.233
  Y = 187.086
FEATURE [TechDraw::DrawViewAnnotation] Annotation075
  Font = osifont
  LineSpace = 100
  LockPosition = false
  MaxWidth = -1
  Rotation = 0
  ScaleType = 2
  Text = 1
  TextSize = 5
  TextStyle = 0
  X = 112.772
  Y = 177.627
FEATURE [TechDraw::DrawViewAnnotation] Annotation076
  Font = osifont
  LineSpace = 100
  LockPosition = false
  MaxWidth = -1
  Rotation = 0
  ScaleType = 2
  Text = pas a pas etape 7
  TextSize = 5
  TextStyle = 0
  X = 58.7543
  Y = 177.627
FEATURE [TechDraw::DrawPage] Page013  label="Feuille013"
  KeepUpdated = true
  NextBalloonIndex = 2
  ProjectionType = 0
  Template = -> Template013
  Views = -> [ProjGroup009,Detail001,Balloon044,Dimension040,View034,Annotation015,Annotation016,Annotation073,Annotation076,Annotation072,Annotation074,Annotation075]
FEATURE [TechDraw::DrawViewAnnotation] Annotation077
  Font = osifont
  LineSpace = 100
  LockPosition = false
  MaxWidth = -1
  Rotation = 0
  ScaleType = 2
  Text = Brouette Balance
  TextSize = 5
  TextStyle = 0
  X = 55.7589
  Y = 197.741
FEATURE [TechDraw::DrawViewAnnotation] Annotation078
  Font = osifont
  LineSpace = 100
  LockPosition = false
  MaxWidth = -1
  Rotation = 0
  ScaleType = 2
  Text = 01/03/25
  TextSize = 5
  TextStyle = 0
  X = 45.099
  Y = 187.086
FEATURE [TechDraw::DrawViewAnnotation] Annotation079
  Font = osifont
  LineSpace = 100
  LockPosition = false
  MaxWidth = -1
  Rotation = 0
  ScaleType = 2
  Text = 10/16
  TextSize = 5
  TextStyle = 0
  X = 101.233
  Y = 187.086
FEATURE [TechDraw::DrawViewAnnotation] Annotation080
  Font = osifont
  LineSpace = 100
  LockPosition = false
  MaxWidth = -1
  Rotation = 0
  ScaleType = 2
  Text = 1
  TextSize = 5
  TextStyle = 0
  X = 113.474
  Y = 177.627
FEATURE [TechDraw::DrawViewAnnotation] Annotation081
  Font = osifont
  LineSpace = 100
  LockPosition = false
  MaxWidth = -1
  Rotation = 0
  ScaleType = 2
  Text = pas a pas etape 5
  TextSize = 5
  TextStyle = 0
  X = 58.7543
  Y = 177.627
FEATURE [TechDraw::DrawPage] Page011  label="Feuille011"
  KeepUpdated = true
  NextBalloonIndex = 31
  ProjectionType = 0
  Template = -> Template011
  Views = -> [View017,View018,View019,View020,View021,View022,Annotation011,Dimension038,Annotation012,Balloon040,Sheet004,Annotation077,Annotation078,Annotation079,Annotation080,Annotation081]
FEATURE [TechDraw::DrawViewAnnotation] Annotation082
  Font = osifont
  LineSpace = 100
  LockPosition = false
  MaxWidth = -1
  Rotation = 0
  ScaleType = 2
  Text = Brouette Balance
  TextSize = 5
  TextStyle = 0
  X = 54.7006
  Y = 197.741
FEATURE [TechDraw::DrawViewAnnotation] Annotation083
  Font = osifont
  LineSpace = 100
  LockPosition = false
  MaxWidth = -1
  Rotation = 0
  ScaleType = 2
  Text = 01/03/25
  TextSize = 5
  TextStyle = 0
  X = 45.099
  Y = 187.086
FEATURE [TechDraw::DrawViewAnnotation] Annotation084
  Font = osifont
  LineSpace = 100
  LockPosition = false
  MaxWidth = -1
  Rotation = 0
  ScaleType = 2
  Text = 11/16
  TextSize = 5
  TextStyle = 0
  X = 101.233
  Y = 187.086
FEATURE [TechDraw::DrawViewAnnotation] Annotation085
  Font = osifont
  LineSpace = 100
  LockPosition = false
  MaxWidth = -1
  Rotation = 0
  ScaleType = 2
  Text = 1
  TextSize = 5
  TextStyle = 0
  X = 113.474
  Y = 177.627
FEATURE [TechDraw::DrawViewAnnotation] Annotation086
  Font = osifont
  LineSpace = 100
  LockPosition = false
  MaxWidth = -1
  Rotation = 0
  ScaleType = 2
  Text = pas a pas etape 6
  TextSize = 5
  TextStyle = 0
  X = 58.7543
  Y = 177.627
FEATURE [TechDraw::DrawPage] Page012  label="Feuille012"
  KeepUpdated = true
  NextBalloonIndex = 33
  ProjectionType = 0
  Template = -> Template012
  Views = -> [ProjGroup008,View024,Sheet005,Balloon042,Detail002,Annotation013,Annotation014,Dimension039,Balloon043,Annotation082,Annotation083,Annotation084,Annotation085,Annotation086]
FEATURE [TechDraw::DrawViewAnnotation] Annotation087
  Font = osifont
  LineSpace = 100
  LockPosition = false
  MaxWidth = -1
  Rotation = 0
  ScaleType = 2
  Text = Brouette Balance
  TextSize = 5
  TextStyle = 0
  X = 55.7589
  Y = 197.741
FEATURE [TechDraw::DrawViewAnnotation] Annotation088
  Font = osifont
  LineSpace = 100
  LockPosition = false
  MaxWidth = -1
  Rotation = 0
  ScaleType = 2
  Text = 01/03/25
  TextSize = 5
  TextStyle = 0
  X = 45.099
  Y = 187.086
FEATURE [TechDraw::DrawViewAnnotation] Annotation089
  Font = osifont
  LineSpace = 100
  LockPosition = false
  MaxWidth = -1
  Rotation = 0
  ScaleType = 2
  Text = 13/16
  TextSize = 5
  TextStyle = 0
  X = 102.383
  Y = 187.086
FEATURE [TechDraw::DrawViewAnnotation] Annotation090
  Font = osifont
  LineSpace = 100
  LockPosition = false
  MaxWidth = -1
  Rotation = 0
  ScaleType = 2
  Text = 1
  TextSize = 5
  TextStyle = 0
  X = 113.474
  Y = 177.927
FEATURE [TechDraw::DrawViewAnnotation] Annotation091
  Font = osifont
  LineSpace = 100
  LockPosition = false
  MaxWidth = -1
  Rotation = 0
  ScaleType = 2
  Text = pas a pas etape 8
  TextSize = 5
  TextStyle = 0
  X = 58.7543
  Y = 177.927
FEATURE [TechDraw::DrawPage] Page014  label="Feuille014"
  KeepUpdated = true
  NextBalloonIndex = 9
  ProjectionType = 0
  Template = -> Template014
  Views = -> [ProjGroup010,Sheet006,View035,Balloon045,Balloon046,Balloon047,Balloon049,Balloon050,Annotation017,Dimension042,Dimension043,Annotation018,Annotation087,Annotation088,Annotation089,Annotation090,Annotation091]
FEATURE [TechDraw::DrawViewAnnotation] Annotation092
  Font = osifont
  LineSpace = 100
  LockPosition = false
  MaxWidth = -1
  Rotation = 0
  ScaleType = 2
  Text = Brouette Balance
  TextSize = 5
  TextStyle = 0
  X = 55.7589
  Y = 197.741
FEATURE [TechDraw::DrawViewAnnotation] Annotation093
  Font = osifont
  LineSpace = 100
  LockPosition = false
  MaxWidth = -1
  Rotation = 0
  ScaleType = 2
  Text = 01/03/25
  TextSize = 5
  TextStyle = 0
  X = 45.099
  Y = 187.086
FEATURE [TechDraw::DrawViewAnnotation] Annotation094
  Font = osifont
  LineSpace = 100
  LockPosition = false
  MaxWidth = -1
  Rotation = 0
  ScaleType = 2
  Text = 14/16
  TextSize = 5
  TextStyle = 0
  X = 101.233
  Y = 187.086
FEATURE [TechDraw::DrawViewAnnotation] Annotation095
  Font = osifont
  LineSpace = 100
  LockPosition = false
  MaxWidth = -1
  Rotation = 0
  ScaleType = 2
  Text = 1
  TextSize = 5
  TextStyle = 0
  X = 113.474
  Y = 177.627
FEATURE [TechDraw::DrawViewAnnotation] Annotation096
  Font = osifont
  LineSpace = 100
  LockPosition = false
  MaxWidth = -1
  Rotation = 0
  ScaleType = 2
  Text = pas a pas etape 9
  TextSize = 5
  TextStyle = 0
  X = 58.7543
  Y = 177.627
FEATURE [TechDraw::DrawPage] Page015  label="Feuille015"
  KeepUpdated = true
  NextBalloonIndex = 3
  ProjectionType = 0
  Template = -> Template015
  Views = -> [ProjGroup011,View036,Balloon051,Balloon052,Dimension044,Dimension045,Dimension046,Sheet007,Annotation019,Annotation092,Annotation093,Annotation094,Annotation095,Annotation096]
FEATURE [TechDraw::DrawViewAnnotation] Annotation097
  Font = osifont
  LineSpace = 100
  LockPosition = false
  MaxWidth = -1
  Rotation = 0
  ScaleType = 2
  Text = Brouette Balance
  TextSize = 5
  TextStyle = 0
  X = 55.7589
  Y = 197.741
FEATURE [TechDraw::DrawViewAnnotation] Annotation098
  Font = osifont
  LineSpace = 100
  LockPosition = false
  MaxWidth = -1
  Rotation = 0
  ScaleType = 2
  Text = 01/03/25
  TextSize = 5
  TextStyle = 0
  X = 45.099
  Y = 187.086
FEATURE [TechDraw::DrawViewAnnotation] Annotation099
  Font = osifont
  LineSpace = 100
  LockPosition = false
  MaxWidth = -1
  Rotation = 0
  ScaleType = 2
  Text = 15/16
  TextSize = 5
  TextStyle = 0
  X = 101.233
  Y = 187.086
FEATURE [TechDraw::DrawViewAnnotation] Annotation100
  Font = osifont
  LineSpace = 100
  LockPosition = false
  MaxWidth = -1
  Rotation = 0
  ScaleType = 2
  Text = 1
  TextSize = 5
  TextStyle = 0
  X = 116.129
  Y = 177.627
FEATURE [TechDraw::DrawViewAnnotation] Annotation101
  Font = osifont
  LineSpace = 100
  LockPosition = false
  MaxWidth = -1
  Rotation = 0
  ScaleType = 2
  Text = pas a pas etape 10
  TextSize = 5
  TextStyle = 0
  X = 58.7543
  Y = 177.627
FEATURE [TechDraw::DrawViewAnnotation] Annotation107
  Font = osifont
  LineSpace = 100
  LockPosition = false
  MaxWidth = -1
  Rotation = 0
  ScaleType = 2
  Text = Brouette Balance
  TextSize = 5
  TextStyle = 0
  X = 55.7589
  Y = 197.741
FEATURE [TechDraw::DrawViewAnnotation] Annotation108
  Font = osifont
  LineSpace = 100
  LockPosition = false
  MaxWidth = -1
  Rotation = 0
  ScaleType = 2
  Text = 01/03/25
  TextSize = 5
  TextStyle = 0
  X = 45.099
  Y = 187.086
FEATURE [TechDraw::DrawViewAnnotation] Annotation109
  Font = osifont
  LineSpace = 100
  LockPosition = false
  MaxWidth = -1
  Rotation = 0
  ScaleType = 2
  Text = 16/16
  TextSize = 5
  TextStyle = 0
  X = 101.022
  Y = 187.086
FEATURE [TechDraw::DrawViewAnnotation] Annotation110
  Font = osifont
  LineSpace = 100
  LockPosition = false
  MaxWidth = -1
  Rotation = 0
  ScaleType = 2
  Text = 1
  TextSize = 5
  TextStyle = 0
  X = 113.474
  Y = 177.627
FEATURE [TechDraw::DrawViewAnnotation] Annotation111
  Font = osifont
  LineSpace = 100
  LockPosition = false
  MaxWidth = -1
  Rotation = 0
  ScaleType = 2
  Text = pas a pas etape 11
  TextSize = 5
  TextStyle = 0
  X = 58.9158
  Y = 177.627
FEATURE [TechDraw::DrawPage] Page017  label="Feuille017"
  KeepUpdated = true
  NextBalloonIndex = 1
  ProjectionType = 0
  Template = -> Template017
  Views = -> [View037,View038,View039,View040,View041,View042,View043,Annotation021,Annotation022,Annotation023,Annotation107,Annotation108,Annotation109,Annotation110,Annotation111]
FEATURE [TechDraw::DrawViewBalloon] Balloon070  label="Infobulle070"
  BubbleShape = 3
  EndType = 0
  EndTypeScale = 1
  KinkLength = 0
  LockPosition = false
  OriginX = -1293.29
  OriginY = -122.24
  Rotation = 0
  ScaleType = 2
  ShapeScale = 1
  SourceView = -> View028
  Text = A16
  TextWrapLen = -1
  X = -1513.94
  Y = -116.946
FEATURE [TechDraw::DrawViewBalloon] Balloon071  label="Infobulle071"
  BubbleShape = 3
  EndType = 0
  EndTypeScale = 1
  KinkLength = 5
  LockPosition = false
  OriginX = -292.378
  OriginY = -121.178
  Rotation = 0
  ScaleType = 2
  ShapeScale = 1
  SourceView = -> ProjItem014
  Text = A16
  TextWrapLen = -1
  X = -554.613
  Y = -117.356
FEATURE [TechDraw::DrawPage] Page016  label="Feuille016"
  KeepUpdated = true
  NextBalloonIndex = 3
  ProjectionType = 0
  Template = -> Template016
  Views = -> [ProjGroup012,Sheet008,Annotation020,Annotation097,Annotation098,Annotation099,Annotation100,Annotation101,Balloon070,Balloon071]
